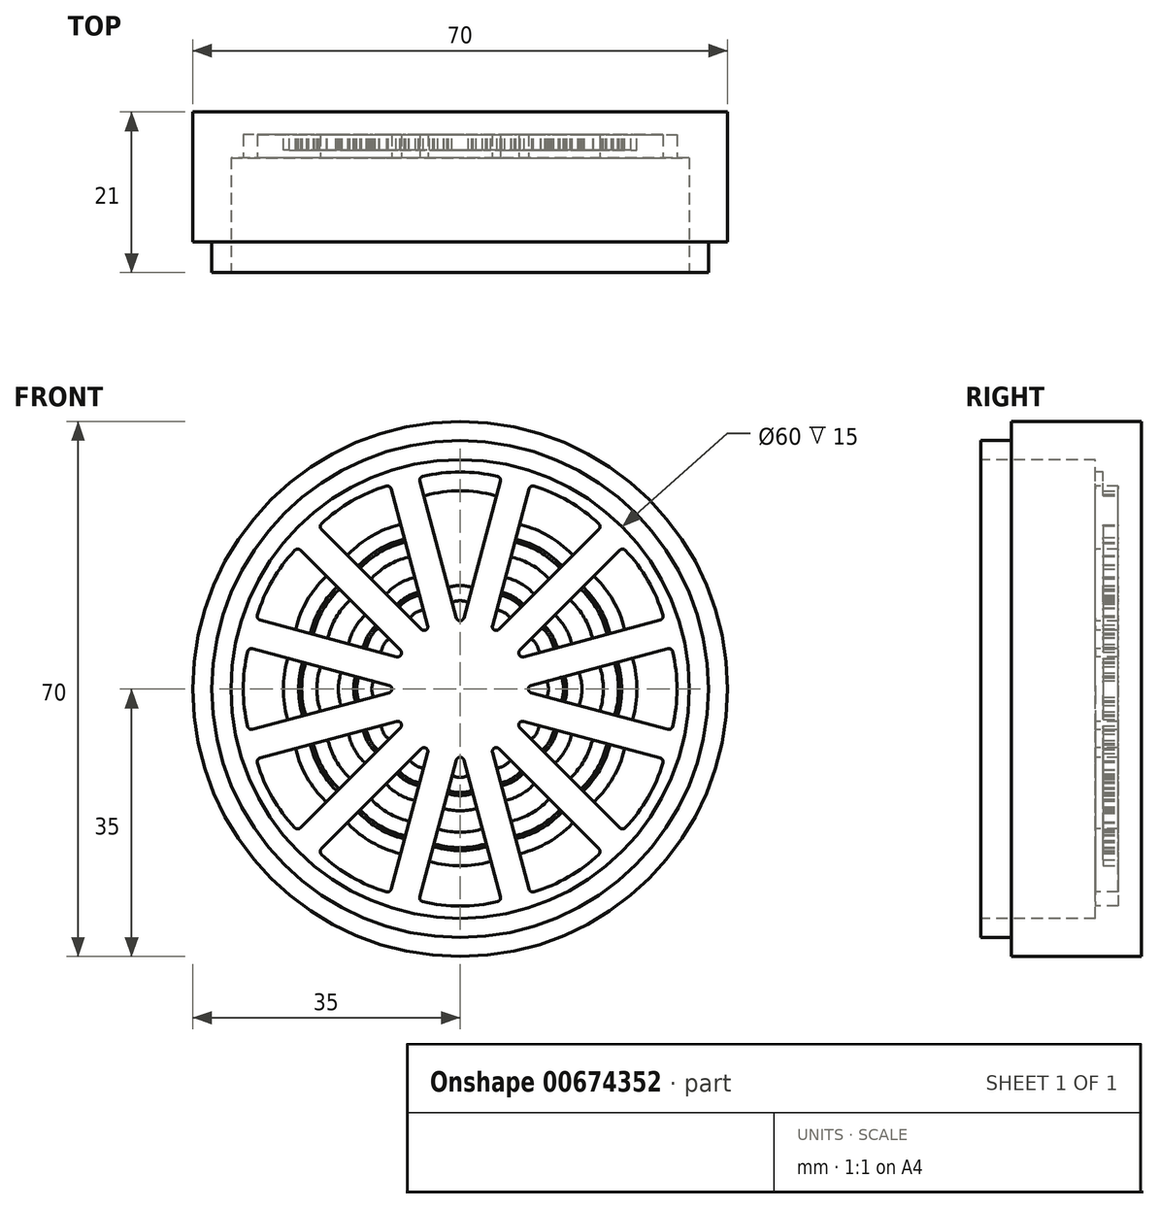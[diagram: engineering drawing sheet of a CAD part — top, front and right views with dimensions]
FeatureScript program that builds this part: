
annotation { "Feature Type Name" : "Feature", "Feature Type Description" : "" }
export const myFeature = defineFeature(function(context is Context, id is Id, definition is map)
    precondition{}
    {
        {
            var Q0;
            Q0=qCreatedBy(makeId("Front.planeOp"),FACE);
            var sketch = newSketch(context, id + "F0", { "sketchPlane" : qUnion([Q0])});
            skCircle(sketch, "E0", {"center": v(0, 0) * mm, "radius": 35 * mm});
            skSolve(sketch);
        }
        {
            var Q0;
            Q0=makeQuery(id+"F0.imprint","IMPRINT",FACE,{"disambiguationData":[TD([[makeQuery(id+"F0.imprint","IMPRINT",EDGE,{"derivedFrom":sQuery(id+"F0.wireOp",EDGE,"E0")}),1.0]])]});
            extrude(context, id + "F1", {"entities" : qUnion([Q0]), "depth" : 21 * mm, "offsetDistance" : 25 * mm});
        }
        {
            var Q0;
            Q0=makeQuery(id+"F1.opExtrude","CAP_FACE",FACE,{"disambiguationData":[OSD([sQuery(id+"F0.wireOp",EDGE,"E0")])],"isStart":false});
            var sketch = newSketch(context, id + "F2", { "sketchPlane" : qUnion([Q0])});
            skCircle(sketch, "E1", {"center": v(0, 0) * mm, "radius": 30 * mm});
            skSolve(sketch);
        }
        {
            var Q0;
            Q0=makeQuery(id+"F2.imprint","IMPRINT",FACE,{"disambiguationData":[TD([[makeQuery(id+"F2.imprint","IMPRINT",EDGE,{"derivedFrom":sQuery(id+"F2.wireOp",EDGE,"E1")}),1.0]])]});
            extrude(context, id + "F3", {"entities" : qUnion([Q0]), "operationType" : NewBodyOperationType.REMOVE, "oppositeDirection" : true, "depth" : 15 * mm, "offsetDistance" : 25 * mm});
        }
        {
            var Q0;
            Q0=makeQuery(id+"F1.opExtrude","CAP_FACE",FACE,{"disambiguationData":[OSD([sQuery(id+"F0.wireOp",EDGE,"E0")])],"isStart":false});
            var sketch = newSketch(context, id + "F4", { "sketchPlane" : qUnion([Q0])});
            skCircle(sketch, "E2", {"center": v(0, 0) * mm, "radius": 32.5 * mm});
            skSolve(sketch);
        }
        {
            var Q0;
            Q0=makeQuery(id+"F4.imprint","IMPRINT",FACE,{"disambiguationData":[TD([[makeQuery(id+"F4.imprint","IMPRINT",EDGE,{"derivedFrom":sQuery(id+"F4.wireOp",EDGE,"E2")}),-1.0]])]});
            extrude(context, id + "F5", {"entities" : qUnion([Q0]), "operationType" : NewBodyOperationType.REMOVE, "oppositeDirection" : true, "depth" : 4 * mm, "offsetDistance" : 25 * mm});
        }
        {
            var Q0;
            Q0=makeQuery(id+"F3.boolean.opBoolean","COPY",FACE,{"derivedFrom":makeQuery(id+"F3.opExtrude","CAP_FACE",FACE,{"disambiguationData":[OSD([sQuery(id+"F2.wireOp",EDGE,"E1")])],"isStart":false})});
            var sketch = newSketch(context, id + "F6", { "sketchPlane" : qUnion([Q0])});
            skLineSegment(sketch, "E3", {"start": v(0, 0) * mm, "end": v(-7.76, 28.98) * mm, "construction": true});
            skLineSegment(sketch, "E4", {"start": v(0, 0) * mm, "end": v(7.76, 28.98) * mm, "construction": true});
            skLineSegment(sketch, "E5", {"start": v(0, 0) * mm, "end": v(0, 30) * mm, "construction": true});
            skCircle(sketch, "E6", {"center": v(0, 0) * mm, "radius": 7.5 * mm, "construction": true});
            skLineSegment(sketch, "E7", {"start": v(-0.48, 9.3) * mm, "end": v(-5.27, 27.18) * mm});
            skLineSegment(sketch, "E8.MirrorCS", {"start": v(0.48, 9.3) * mm, "end": v(5.27, 27.18) * mm});
            skArc(sketch, "E9", {"start": v(-4.9, 27.8) * mm, "mid": v(0, 28.38) * mm, "end": v(4.9, 27.8) * mm});
            skPoint(sketch, "E10.visualSharp", {"position": v(-5.4, 27.67) * mm});
            skArc(sketch, "E10.filletArc", {"start": v(-4.9, 27.8) * mm, "mid": v(-5.22, 27.57) * mm, "end": v(-5.27, 27.18) * mm});
            skPoint(sketch, "E11.visualSharp", {"position": v(5.4, 27.67) * mm});
            skArc(sketch, "E11.filletArc", {"start": v(5.27, 27.18) * mm, "mid": v(5.22, 27.57) * mm, "end": v(4.9, 27.8) * mm});
            skArc(sketch, "E12.filletArc", {"start": v(-0.48, 9.3) * mm, "mid": v(0, 8.93) * mm, "end": v(0.48, 9.3) * mm});
            skPoint(sketch, "E13.1.0", {"position": v(-18.52, 21.26) * mm});
            skLineSegment(sketch, "E13.1.1", {"start": v(-5.07, 7.81) * mm, "end": v(-18.16, 20.9) * mm});
            skLineSegment(sketch, "E13.1.2", {"start": v(-4.23, 8.3) * mm, "end": v(-9.02, 26.18) * mm});
            skPoint(sketch, "E13.1.3", {"position": v(-9.15, 26.67) * mm});
            skArc(sketch, "E13.1.4", {"start": v(-18.15, 21.62) * mm, "mid": v(-14.2, 24.58) * mm, "end": v(-9.65, 26.53) * mm});
            skPoint(sketch, "E13.1.5", {"position": v(-3.75, 6.5) * mm});
            skArc(sketch, "E13.1.6", {"start": v(-5.07, 7.81) * mm, "mid": v(-4.47, 7.74) * mm, "end": v(-4.23, 8.3) * mm});
            skArc(sketch, "E13.1.7", {"start": v(-9.02, 26.18) * mm, "mid": v(-9.26, 26.48) * mm, "end": v(-9.65, 26.53) * mm});
            skArc(sketch, "E13.1.8", {"start": v(-18.15, 21.62) * mm, "mid": v(-18.3, 21.26) * mm, "end": v(-18.16, 20.9) * mm});
            skPoint(sketch, "E13.2.0", {"position": v(-26.67, 9.15) * mm});
            skLineSegment(sketch, "E13.2.1", {"start": v(-8.3, 4.23) * mm, "end": v(-26.18, 9.02) * mm});
            skLineSegment(sketch, "E13.2.2", {"start": v(-7.81, 5.07) * mm, "end": v(-20.9, 18.16) * mm});
            skPoint(sketch, "E13.2.3", {"position": v(-21.26, 18.52) * mm});
            skArc(sketch, "E13.2.4", {"start": v(-26.53, 9.65) * mm, "mid": v(-24.58, 14.2) * mm, "end": v(-21.62, 18.15) * mm});
            skPoint(sketch, "E13.2.5", {"position": v(-6.5, 3.75) * mm});
            skArc(sketch, "E13.2.6", {"start": v(-8.3, 4.23) * mm, "mid": v(-7.74, 4.47) * mm, "end": v(-7.81, 5.07) * mm});
            skArc(sketch, "E13.2.7", {"start": v(-20.9, 18.16) * mm, "mid": v(-21.26, 18.3) * mm, "end": v(-21.62, 18.15) * mm});
            skArc(sketch, "E13.2.8", {"start": v(-26.53, 9.65) * mm, "mid": v(-26.48, 9.26) * mm, "end": v(-26.18, 9.02) * mm});
            skPoint(sketch, "E13.3.0", {"position": v(-27.67, -5.4) * mm});
            skLineSegment(sketch, "E13.3.1", {"start": v(-9.3, -0.48) * mm, "end": v(-27.18, -5.27) * mm});
            skLineSegment(sketch, "E13.3.2", {"start": v(-9.3, 0.48) * mm, "end": v(-27.18, 5.27) * mm});
            skPoint(sketch, "E13.3.3", {"position": v(-27.67, 5.4) * mm});
            skArc(sketch, "E13.3.4", {"start": v(-27.8, -4.9) * mm, "mid": v(-28.38, 0) * mm, "end": v(-27.8, 4.9) * mm});
            skPoint(sketch, "E13.3.5", {"position": v(-7.5, 0) * mm});
            skArc(sketch, "E13.3.6", {"start": v(-9.3, -0.48) * mm, "mid": v(-8.93, 0) * mm, "end": v(-9.3, 0.48) * mm});
            skArc(sketch, "E13.3.7", {"start": v(-27.18, 5.27) * mm, "mid": v(-27.57, 5.22) * mm, "end": v(-27.8, 4.9) * mm});
            skArc(sketch, "E13.3.8", {"start": v(-27.8, -4.9) * mm, "mid": v(-27.57, -5.22) * mm, "end": v(-27.18, -5.27) * mm});
            skPoint(sketch, "E13.4.0", {"position": v(-21.26, -18.52) * mm});
            skLineSegment(sketch, "E13.4.1", {"start": v(-7.81, -5.07) * mm, "end": v(-20.9, -18.16) * mm});
            skLineSegment(sketch, "E13.4.2", {"start": v(-8.3, -4.23) * mm, "end": v(-26.18, -9.02) * mm});
            skPoint(sketch, "E13.4.3", {"position": v(-26.67, -9.15) * mm});
            skArc(sketch, "E13.4.4", {"start": v(-21.62, -18.15) * mm, "mid": v(-24.58, -14.2) * mm, "end": v(-26.53, -9.65) * mm});
            skPoint(sketch, "E13.4.5", {"position": v(-6.5, -3.75) * mm});
            skArc(sketch, "E13.4.6", {"start": v(-7.81, -5.07) * mm, "mid": v(-7.74, -4.47) * mm, "end": v(-8.3, -4.23) * mm});
            skArc(sketch, "E13.4.7", {"start": v(-26.18, -9.02) * mm, "mid": v(-26.48, -9.26) * mm, "end": v(-26.53, -9.65) * mm});
            skArc(sketch, "E13.4.8", {"start": v(-21.62, -18.15) * mm, "mid": v(-21.26, -18.3) * mm, "end": v(-20.9, -18.16) * mm});
            skPoint(sketch, "E13.5.0", {"position": v(-9.15, -26.67) * mm});
            skLineSegment(sketch, "E13.5.1", {"start": v(-4.23, -8.3) * mm, "end": v(-9.02, -26.18) * mm});
            skLineSegment(sketch, "E13.5.2", {"start": v(-5.07, -7.81) * mm, "end": v(-18.16, -20.9) * mm});
            skPoint(sketch, "E13.5.3", {"position": v(-18.52, -21.26) * mm});
            skArc(sketch, "E13.5.4", {"start": v(-9.65, -26.53) * mm, "mid": v(-14.2, -24.58) * mm, "end": v(-18.15, -21.62) * mm});
            skPoint(sketch, "E13.5.5", {"position": v(-3.75, -6.5) * mm});
            skArc(sketch, "E13.5.6", {"start": v(-4.23, -8.3) * mm, "mid": v(-4.47, -7.74) * mm, "end": v(-5.07, -7.81) * mm});
            skArc(sketch, "E13.5.7", {"start": v(-18.16, -20.9) * mm, "mid": v(-18.3, -21.26) * mm, "end": v(-18.15, -21.62) * mm});
            skArc(sketch, "E13.5.8", {"start": v(-9.65, -26.53) * mm, "mid": v(-9.26, -26.48) * mm, "end": v(-9.02, -26.18) * mm});
            skPoint(sketch, "E13.6.0", {"position": v(5.4, -27.67) * mm});
            skLineSegment(sketch, "E13.6.1", {"start": v(0.48, -9.3) * mm, "end": v(5.27, -27.18) * mm});
            skLineSegment(sketch, "E13.6.2", {"start": v(-0.48, -9.3) * mm, "end": v(-5.27, -27.18) * mm});
            skPoint(sketch, "E13.6.3", {"position": v(-5.4, -27.67) * mm});
            skArc(sketch, "E13.6.4", {"start": v(4.9, -27.8) * mm, "mid": v(0, -28.38) * mm, "end": v(-4.9, -27.8) * mm});
            skPoint(sketch, "E13.6.5", {"position": v(0, -7.5) * mm});
            skArc(sketch, "E13.6.6", {"start": v(0.48, -9.3) * mm, "mid": v(0, -8.93) * mm, "end": v(-0.48, -9.3) * mm});
            skArc(sketch, "E13.6.7", {"start": v(-5.27, -27.18) * mm, "mid": v(-5.22, -27.57) * mm, "end": v(-4.9, -27.8) * mm});
            skArc(sketch, "E13.6.8", {"start": v(4.9, -27.8) * mm, "mid": v(5.22, -27.57) * mm, "end": v(5.27, -27.18) * mm});
            skPoint(sketch, "E13.7.0", {"position": v(18.52, -21.26) * mm});
            skLineSegment(sketch, "E13.7.1", {"start": v(5.07, -7.81) * mm, "end": v(18.16, -20.9) * mm});
            skLineSegment(sketch, "E13.7.2", {"start": v(4.23, -8.3) * mm, "end": v(9.02, -26.18) * mm});
            skPoint(sketch, "E13.7.3", {"position": v(9.15, -26.67) * mm});
            skArc(sketch, "E13.7.4", {"start": v(18.15, -21.62) * mm, "mid": v(14.2, -24.58) * mm, "end": v(9.65, -26.53) * mm});
            skPoint(sketch, "E13.7.5", {"position": v(3.75, -6.5) * mm});
            skArc(sketch, "E13.7.6", {"start": v(5.07, -7.81) * mm, "mid": v(4.47, -7.74) * mm, "end": v(4.23, -8.3) * mm});
            skArc(sketch, "E13.7.7", {"start": v(9.02, -26.18) * mm, "mid": v(9.26, -26.48) * mm, "end": v(9.65, -26.53) * mm});
            skArc(sketch, "E13.7.8", {"start": v(18.15, -21.62) * mm, "mid": v(18.3, -21.26) * mm, "end": v(18.16, -20.9) * mm});
            skPoint(sketch, "E13.8.0", {"position": v(26.67, -9.15) * mm});
            skLineSegment(sketch, "E13.8.1", {"start": v(8.3, -4.23) * mm, "end": v(26.18, -9.02) * mm});
            skLineSegment(sketch, "E13.8.2", {"start": v(7.81, -5.07) * mm, "end": v(20.9, -18.16) * mm});
            skPoint(sketch, "E13.8.3", {"position": v(21.26, -18.52) * mm});
            skArc(sketch, "E13.8.4", {"start": v(26.53, -9.65) * mm, "mid": v(24.58, -14.2) * mm, "end": v(21.62, -18.15) * mm});
            skPoint(sketch, "E13.8.5", {"position": v(6.5, -3.75) * mm});
            skArc(sketch, "E13.8.6", {"start": v(8.3, -4.23) * mm, "mid": v(7.74, -4.47) * mm, "end": v(7.81, -5.07) * mm});
            skArc(sketch, "E13.8.7", {"start": v(20.9, -18.16) * mm, "mid": v(21.26, -18.3) * mm, "end": v(21.62, -18.15) * mm});
            skArc(sketch, "E13.8.8", {"start": v(26.53, -9.65) * mm, "mid": v(26.48, -9.26) * mm, "end": v(26.18, -9.02) * mm});
            skPoint(sketch, "E13.9.0", {"position": v(27.67, 5.4) * mm});
            skLineSegment(sketch, "E13.9.1", {"start": v(9.3, 0.48) * mm, "end": v(27.18, 5.27) * mm});
            skLineSegment(sketch, "E13.9.2", {"start": v(9.3, -0.48) * mm, "end": v(27.18, -5.27) * mm});
            skPoint(sketch, "E13.9.3", {"position": v(27.67, -5.4) * mm});
            skArc(sketch, "E13.9.4", {"start": v(27.8, 4.9) * mm, "mid": v(28.38, 0) * mm, "end": v(27.8, -4.9) * mm});
            skPoint(sketch, "E13.9.5", {"position": v(7.5, 0) * mm});
            skArc(sketch, "E13.9.6", {"start": v(9.3, 0.48) * mm, "mid": v(8.93, 0) * mm, "end": v(9.3, -0.48) * mm});
            skArc(sketch, "E13.9.7", {"start": v(27.18, -5.27) * mm, "mid": v(27.57, -5.22) * mm, "end": v(27.8, -4.9) * mm});
            skArc(sketch, "E13.9.8", {"start": v(27.8, 4.9) * mm, "mid": v(27.57, 5.22) * mm, "end": v(27.18, 5.27) * mm});
            skPoint(sketch, "E13.10.0", {"position": v(21.26, 18.52) * mm});
            skLineSegment(sketch, "E13.10.1", {"start": v(7.81, 5.07) * mm, "end": v(20.9, 18.16) * mm});
            skLineSegment(sketch, "E13.10.2", {"start": v(8.3, 4.23) * mm, "end": v(26.18, 9.02) * mm});
            skPoint(sketch, "E13.10.3", {"position": v(26.67, 9.15) * mm});
            skArc(sketch, "E13.10.4", {"start": v(21.62, 18.15) * mm, "mid": v(24.58, 14.2) * mm, "end": v(26.53, 9.65) * mm});
            skPoint(sketch, "E13.10.5", {"position": v(6.5, 3.75) * mm});
            skArc(sketch, "E13.10.6", {"start": v(7.81, 5.07) * mm, "mid": v(7.74, 4.47) * mm, "end": v(8.3, 4.23) * mm});
            skArc(sketch, "E13.10.7", {"start": v(26.18, 9.02) * mm, "mid": v(26.48, 9.26) * mm, "end": v(26.53, 9.65) * mm});
            skArc(sketch, "E13.10.8", {"start": v(21.62, 18.15) * mm, "mid": v(21.26, 18.3) * mm, "end": v(20.9, 18.16) * mm});
            skPoint(sketch, "E13.11.0", {"position": v(9.15, 26.67) * mm});
            skLineSegment(sketch, "E13.11.1", {"start": v(4.23, 8.3) * mm, "end": v(9.02, 26.18) * mm});
            skLineSegment(sketch, "E13.11.2", {"start": v(5.07, 7.81) * mm, "end": v(18.16, 20.9) * mm});
            skPoint(sketch, "E13.11.3", {"position": v(18.52, 21.26) * mm});
            skArc(sketch, "E13.11.4", {"start": v(9.65, 26.53) * mm, "mid": v(14.2, 24.58) * mm, "end": v(18.15, 21.62) * mm});
            skPoint(sketch, "E13.11.5", {"position": v(3.75, 6.5) * mm});
            skArc(sketch, "E13.11.6", {"start": v(4.23, 8.3) * mm, "mid": v(4.47, 7.74) * mm, "end": v(5.07, 7.81) * mm});
            skArc(sketch, "E13.11.7", {"start": v(18.16, 20.9) * mm, "mid": v(18.3, 21.26) * mm, "end": v(18.15, 21.62) * mm});
            skArc(sketch, "E13.11.8", {"start": v(9.65, 26.53) * mm, "mid": v(9.26, 26.48) * mm, "end": v(9.02, 26.18) * mm});
            skSolve(sketch);
        }
        {
            var Q0;
            Q0=makeQuery(id+"F6.imprint","IMPRINT",FACE,{"disambiguationData":[TD([[makeQuery(id+"F6.imprint","IMPRINT",EDGE,{"derivedFrom":sQuery(id+"F6.wireOp",EDGE,"E13.1.1")}),-1.0]])]});
            var Q1;
            Q1=makeQuery(id+"F6.imprint","IMPRINT",FACE,{"disambiguationData":[TD([[makeQuery(id+"F6.imprint","IMPRINT",EDGE,{"derivedFrom":sQuery(id+"F6.wireOp",EDGE,"E7")}),-1.0]])]});
            var Q2;
            Q2=makeQuery(id+"F6.imprint","IMPRINT",FACE,{"disambiguationData":[TD([[makeQuery(id+"F6.imprint","IMPRINT",EDGE,{"derivedFrom":sQuery(id+"F6.wireOp",EDGE,"E13.11.1")}),-1.0]])]});
            var Q3;
            Q3=makeQuery(id+"F6.imprint","IMPRINT",FACE,{"disambiguationData":[TD([[makeQuery(id+"F6.imprint","IMPRINT",EDGE,{"derivedFrom":sQuery(id+"F6.wireOp",EDGE,"E13.10.1")}),-1.0]])]});
            var Q4;
            Q4=makeQuery(id+"F6.imprint","IMPRINT",FACE,{"disambiguationData":[TD([[makeQuery(id+"F6.imprint","IMPRINT",EDGE,{"derivedFrom":sQuery(id+"F6.wireOp",EDGE,"E13.9.1")}),-1.0]])]});
            var Q5;
            Q5=makeQuery(id+"F6.imprint","IMPRINT",FACE,{"disambiguationData":[TD([[makeQuery(id+"F6.imprint","IMPRINT",EDGE,{"derivedFrom":sQuery(id+"F6.wireOp",EDGE,"E13.8.1")}),-1.0]])]});
            var Q6;
            Q6=makeQuery(id+"F6.imprint","IMPRINT",FACE,{"disambiguationData":[TD([[makeQuery(id+"F6.imprint","IMPRINT",EDGE,{"derivedFrom":sQuery(id+"F6.wireOp",EDGE,"E13.7.1")}),-1.0]])]});
            var Q7;
            Q7=makeQuery(id+"F6.imprint","IMPRINT",FACE,{"disambiguationData":[TD([[makeQuery(id+"F6.imprint","IMPRINT",EDGE,{"derivedFrom":sQuery(id+"F6.wireOp",EDGE,"E13.6.1")}),-1.0]])]});
            var Q8;
            Q8=makeQuery(id+"F6.imprint","IMPRINT",FACE,{"disambiguationData":[TD([[makeQuery(id+"F6.imprint","IMPRINT",EDGE,{"derivedFrom":sQuery(id+"F6.wireOp",EDGE,"E13.5.1")}),-1.0]])]});
            var Q9;
            Q9=makeQuery(id+"F6.imprint","IMPRINT",FACE,{"disambiguationData":[TD([[makeQuery(id+"F6.imprint","IMPRINT",EDGE,{"derivedFrom":sQuery(id+"F6.wireOp",EDGE,"E13.4.1")}),-1.0]])]});
            var Q10;
            Q10=makeQuery(id+"F6.imprint","IMPRINT",FACE,{"disambiguationData":[TD([[makeQuery(id+"F6.imprint","IMPRINT",EDGE,{"derivedFrom":sQuery(id+"F6.wireOp",EDGE,"E13.3.1")}),-1.0]])]});
            var Q11;
            Q11=makeQuery(id+"F6.imprint","IMPRINT",FACE,{"disambiguationData":[TD([[makeQuery(id+"F6.imprint","IMPRINT",EDGE,{"derivedFrom":sQuery(id+"F6.wireOp",EDGE,"E13.2.1")}),-1.0]])]});
            extrude(context, id + "F7", {"entities" : qUnion([Q0, Q1, Q2, Q3, Q4, Q5, Q6, Q7, Q8, Q9, Q10, Q11]), "operationType" : NewBodyOperationType.REMOVE, "oppositeDirection" : true, "depth" : 3 * mm, "offsetDistance" : 25 * mm});
        }
        {
            var Q0;
            Q0=makeQuery(id+"F7.boolean.opBoolean","COPY",FACE,{"derivedFrom":makeQuery(id+"F7.opExtrude","CAP_FACE",FACE,{"disambiguationData":[OSD([sQuery(id+"F6.wireOp",EDGE,"E7"),sQuery(id+"F6.wireOp",EDGE,"E8.MirrorCS"),sQuery(id+"F6.wireOp",EDGE,"E9"),sQuery(id+"F6.wireOp",EDGE,"E10.filletArc"),sQuery(id+"F6.wireOp",EDGE,"E11.filletArc"),sQuery(id+"F6.wireOp",EDGE,"E12.filletArc")])],"isStart":false})});
            var sketch = newSketch(context, id + "F8", { "sketchPlane" : qUnion([Q0])});
            skLineSegment(sketch, "E14", {"start": v(-5.27, 27.18) * mm, "end": v(-0.48, 9.3) * mm});
            skLineSegment(sketch, "E15", {"start": v(5.27, 27.18) * mm, "end": v(0.48, 9.3) * mm});
            skLineSegment(sketch, "E16", {"start": v(-5.27, 27.18) * mm, "end": v(-4.8, 25.45) * mm, "construction": true});
            skLineSegment(sketch, "E17", {"start": v(-4.76, 25.25) * mm, "end": v(-4.65, 24.86) * mm, "construction": true});
            skLineSegment(sketch, "E18", {"start": v(-4.6, 24.67) * mm, "end": v(-4.19, 23.13) * mm});
            skLineSegment(sketch, "E19", {"start": v(-4.14, 22.93) * mm, "end": v(-4.03, 22.55) * mm});
            skLineSegment(sketch, "E20", {"start": v(-3.98, 22.36) * mm, "end": v(-3.57, 20.81) * mm});
            skLineSegment(sketch, "E21", {"start": v(-3.51, 20.61) * mm, "end": v(-3.41, 20.23) * mm});
            skLineSegment(sketch, "E22", {"start": v(-3.36, 20.04) * mm, "end": v(-2.95, 18.5) * mm});
            skLineSegment(sketch, "E23", {"start": v(-2.9, 18.3) * mm, "end": v(-2.79, 17.9) * mm});
            skLineSegment(sketch, "E24", {"start": v(-2.74, 17.72) * mm, "end": v(-2.33, 16.18) * mm});
            skLineSegment(sketch, "E25", {"start": v(-2.27, 15.98) * mm, "end": v(-2.17, 15.6) * mm});
            skLineSegment(sketch, "E26", {"start": v(-2.12, 15.4) * mm, "end": v(-1.7, 13.86) * mm});
            skLineSegment(sketch, "E27", {"start": v(-1.65, 13.66) * mm, "end": v(-1.55, 13.27) * mm});
            skLineSegment(sketch, "E28", {"start": v(-1.55, 13.27) * mm, "end": v(-1.03, 11.34) * mm});
            skLineSegment(sketch, "E29", {"start": v(-1.03, 11.34) * mm, "end": v(-0.93, 10.96) * mm});
            skLineSegment(sketch, "E30", {"start": v(0, 28.38) * mm, "end": v(0, 8.93) * mm, "construction": true});
            skLineSegment(sketch, "E31.MirrorCS", {"start": v(2.27, 15.98) * mm, "end": v(2.17, 15.6) * mm});
            skLineSegment(sketch, "E32.MirrorCS", {"start": v(1.03, 11.34) * mm, "end": v(0.93, 10.96) * mm});
            skLineSegment(sketch, "E33.MirrorCS", {"start": v(4.76, 25.25) * mm, "end": v(4.65, 24.86) * mm, "construction": true});
            skLineSegment(sketch, "E34.MirrorCS", {"start": v(3.51, 20.61) * mm, "end": v(3.41, 20.23) * mm});
            skLineSegment(sketch, "E35.MirrorCS", {"start": v(4.14, 22.93) * mm, "end": v(4.03, 22.55) * mm});
            skLineSegment(sketch, "E36.MirrorCS", {"start": v(2.9, 18.3) * mm, "end": v(2.79, 17.9) * mm});
            skLineSegment(sketch, "E37.MirrorCS", {"start": v(1.65, 13.66) * mm, "end": v(1.55, 13.27) * mm});
            skLineSegment(sketch, "E38.MirrorCS", {"start": v(1.5, 13.1) * mm, "end": v(1.09, 11.56) * mm});
            skLineSegment(sketch, "E39.MirrorCS", {"start": v(5.27, 27.18) * mm, "end": v(4.8, 25.45) * mm, "construction": true});
            skLineSegment(sketch, "E40.MirrorCS", {"start": v(3.98, 22.36) * mm, "end": v(3.57, 20.81) * mm});
            skLineSegment(sketch, "E41.MirrorCS", {"start": v(3.36, 20.04) * mm, "end": v(2.95, 18.5) * mm});
            skLineSegment(sketch, "E42.MirrorCS", {"start": v(4.6, 24.67) * mm, "end": v(4.19, 23.13) * mm});
            skLineSegment(sketch, "E43.MirrorCS", {"start": v(2.12, 15.4) * mm, "end": v(1.7, 13.86) * mm});
            skLineSegment(sketch, "E44.MirrorCS", {"start": v(2.74, 17.72) * mm, "end": v(2.33, 16.18) * mm});
            skArc(sketch, "E45", {"start": v(-4.56, 25.3) * mm, "mid": v(0, 25.93) * mm, "end": v(4.56, 25.3) * mm});
            skArc(sketch, "E46", {"start": v(-4.46, 24.92) * mm, "mid": v(0, 25.53) * mm, "end": v(4.46, 24.92) * mm});
            skArc(sketch, "E47", {"start": v(-3.94, 22.99) * mm, "mid": v(0, 23.53) * mm, "end": v(3.94, 22.99) * mm});
            skArc(sketch, "E48", {"start": v(-3.84, 22.6) * mm, "mid": v(0, 23.13) * mm, "end": v(3.84, 22.6) * mm});
            skArc(sketch, "E49", {"start": v(-3.32, 20.67) * mm, "mid": v(0, 21.13) * mm, "end": v(3.32, 20.67) * mm});
            skArc(sketch, "E50", {"start": v(-3.22, 20.28) * mm, "mid": v(0, 20.73) * mm, "end": v(3.22, 20.28) * mm});
            skArc(sketch, "E51", {"start": v(-2.7, 18.35) * mm, "mid": v(0, 18.73) * mm, "end": v(2.7, 18.35) * mm});
            skArc(sketch, "E52", {"start": v(-2.6, 17.97) * mm, "mid": v(0, 18.33) * mm, "end": v(2.6, 17.97) * mm});
            skArc(sketch, "E53", {"start": v(-2.08, 16.04) * mm, "mid": v(0, 16.34) * mm, "end": v(2.08, 16.04) * mm});
            skArc(sketch, "E54", {"start": v(-1.98, 15.65) * mm, "mid": v(0, 15.94) * mm, "end": v(1.98, 15.65) * mm});
            skArc(sketch, "E55", {"start": v(-1.45, 13.72) * mm, "mid": v(0, 13.94) * mm, "end": v(1.45, 13.72) * mm});
            skArc(sketch, "E56", {"start": v(-1.36, 13.33) * mm, "mid": v(0, 13.54) * mm, "end": v(1.36, 13.33) * mm});
            skArc(sketch, "E57", {"start": v(-0.83, 11.42) * mm, "mid": v(0, 11.55) * mm, "end": v(0.83, 11.42) * mm});
            skArc(sketch, "E58", {"start": v(-0.75, 11.03) * mm, "mid": v(0, 11.16) * mm, "end": v(0.75, 11.03) * mm});
            skPoint(sketch, "E59.visualSharp", {"position": v(-4.76, 25.25) * mm});
            skArc(sketch, "E59.filletArc", {"start": v(-4.8, 25.45) * mm, "mid": v(-4.71, 25.33) * mm, "end": v(-4.56, 25.3) * mm});
            skPoint(sketch, "E60.visualSharp", {"position": v(-4.65, 24.86) * mm});
            skArc(sketch, "E60.filletArc", {"start": v(-4.46, 24.92) * mm, "mid": v(-4.58, 24.83) * mm, "end": v(-4.6, 24.67) * mm});
            skPoint(sketch, "E61.visualSharp", {"position": v(-4.14, 22.93) * mm});
            skArc(sketch, "E61.filletArc", {"start": v(-4.19, 23.13) * mm, "mid": v(-4.1, 23) * mm, "end": v(-3.94, 22.99) * mm});
            skPoint(sketch, "E62.visualSharp", {"position": v(-4.03, 22.55) * mm});
            skArc(sketch, "E62.filletArc", {"start": v(-3.84, 22.6) * mm, "mid": v(-3.96, 22.5) * mm, "end": v(-3.98, 22.36) * mm});
            skPoint(sketch, "E63.visualSharp", {"position": v(-3.51, 20.61) * mm});
            skArc(sketch, "E63.filletArc", {"start": v(-3.57, 20.81) * mm, "mid": v(-3.47, 20.69) * mm, "end": v(-3.32, 20.67) * mm});
            skPoint(sketch, "E64.visualSharp", {"position": v(-3.41, 20.23) * mm});
            skArc(sketch, "E64.filletArc", {"start": v(-3.22, 20.28) * mm, "mid": v(-3.34, 20.19) * mm, "end": v(-3.36, 20.04) * mm});
            skPoint(sketch, "E65.visualSharp", {"position": v(-2.9, 18.3) * mm});
            skArc(sketch, "E65.filletArc", {"start": v(-2.95, 18.5) * mm, "mid": v(-2.85, 18.37) * mm, "end": v(-2.7, 18.35) * mm});
            skPoint(sketch, "E66.visualSharp", {"position": v(-2.79, 17.9) * mm});
            skArc(sketch, "E66.filletArc", {"start": v(-2.6, 17.97) * mm, "mid": v(-2.72, 17.87) * mm, "end": v(-2.74, 17.72) * mm});
            skPoint(sketch, "E67.visualSharp", {"position": v(-2.27, 15.98) * mm});
            skArc(sketch, "E67.filletArc", {"start": v(-2.33, 16.18) * mm, "mid": v(-2.23, 16.06) * mm, "end": v(-2.08, 16.04) * mm});
            skPoint(sketch, "E68.visualSharp", {"position": v(-2.17, 15.6) * mm});
            skArc(sketch, "E68.filletArc", {"start": v(-1.98, 15.65) * mm, "mid": v(-2.1, 15.56) * mm, "end": v(-2.12, 15.4) * mm});
            skPoint(sketch, "E69.visualSharp", {"position": v(-1.65, 13.66) * mm});
            skArc(sketch, "E69.filletArc", {"start": v(-1.7, 13.86) * mm, "mid": v(-1.6, 13.74) * mm, "end": v(-1.45, 13.72) * mm});
            skLineSegment(sketch, "E70", {"start": v(-1.5, 13.1) * mm, "end": v(-1.09, 11.56) * mm});
            skLineSegment(sketch, "E71", {"start": v(-0.88, 10.79) * mm, "end": v(-0.48, 9.3) * mm});
            skLineSegment(sketch, "E72.MirrorCS", {"start": v(1.55, 13.27) * mm, "end": v(1.03, 11.34) * mm});
            skLineSegment(sketch, "E73.MirrorCS", {"start": v(0.88, 10.79) * mm, "end": v(0.48, 9.3) * mm});
            skPoint(sketch, "E74.visualSharp", {"position": v(-1.55, 13.27) * mm});
            skArc(sketch, "E74.filletArc", {"start": v(-1.36, 13.33) * mm, "mid": v(-1.48, 13.24) * mm, "end": v(-1.5, 13.1) * mm});
            skPoint(sketch, "E75.visualSharp", {"position": v(-1.03, 11.34) * mm});
            skArc(sketch, "E75.filletArc", {"start": v(-1.09, 11.56) * mm, "mid": v(-0.99, 11.43) * mm, "end": v(-0.83, 11.42) * mm});
            skPoint(sketch, "E76.visualSharp", {"position": v(-0.93, 10.96) * mm});
            skArc(sketch, "E76.filletArc", {"start": v(-0.75, 11.03) * mm, "mid": v(-0.86, 10.93) * mm, "end": v(-0.88, 10.79) * mm});
            skPoint(sketch, "E77.visualSharp", {"position": v(0.93, 10.96) * mm});
            skArc(sketch, "E77.filletArc", {"start": v(0.88, 10.79) * mm, "mid": v(0.86, 10.93) * mm, "end": v(0.75, 11.03) * mm});
            skPoint(sketch, "E78.visualSharp", {"position": v(1.03, 11.34) * mm});
            skArc(sketch, "E78.filletArc", {"start": v(0.83, 11.42) * mm, "mid": v(0.99, 11.43) * mm, "end": v(1.09, 11.56) * mm});
            skPoint(sketch, "E79.visualSharp", {"position": v(1.55, 13.27) * mm});
            skArc(sketch, "E79.filletArc", {"start": v(1.5, 13.1) * mm, "mid": v(1.48, 13.24) * mm, "end": v(1.36, 13.33) * mm});
            skPoint(sketch, "E80.visualSharp", {"position": v(1.65, 13.66) * mm});
            skArc(sketch, "E80.filletArc", {"start": v(1.45, 13.72) * mm, "mid": v(1.6, 13.74) * mm, "end": v(1.7, 13.86) * mm});
            skPoint(sketch, "E81.visualSharp", {"position": v(2.17, 15.6) * mm});
            skArc(sketch, "E81.filletArc", {"start": v(2.12, 15.4) * mm, "mid": v(2.1, 15.56) * mm, "end": v(1.98, 15.65) * mm});
            skPoint(sketch, "E82.visualSharp", {"position": v(2.27, 15.98) * mm});
            skArc(sketch, "E82.filletArc", {"start": v(2.08, 16.04) * mm, "mid": v(2.23, 16.06) * mm, "end": v(2.33, 16.18) * mm});
            skPoint(sketch, "E83.visualSharp", {"position": v(2.79, 17.9) * mm});
            skArc(sketch, "E83.filletArc", {"start": v(2.74, 17.72) * mm, "mid": v(2.72, 17.87) * mm, "end": v(2.6, 17.97) * mm});
            skPoint(sketch, "E84.visualSharp", {"position": v(2.9, 18.3) * mm});
            skArc(sketch, "E84.filletArc", {"start": v(2.7, 18.35) * mm, "mid": v(2.85, 18.37) * mm, "end": v(2.95, 18.5) * mm});
            skPoint(sketch, "E85.visualSharp", {"position": v(3.41, 20.23) * mm});
            skArc(sketch, "E85.filletArc", {"start": v(3.36, 20.04) * mm, "mid": v(3.34, 20.19) * mm, "end": v(3.22, 20.28) * mm});
            skPoint(sketch, "E86.visualSharp", {"position": v(3.51, 20.61) * mm});
            skArc(sketch, "E86.filletArc", {"start": v(3.32, 20.67) * mm, "mid": v(3.47, 20.69) * mm, "end": v(3.57, 20.81) * mm});
            skPoint(sketch, "E87.visualSharp", {"position": v(4.03, 22.55) * mm});
            skArc(sketch, "E87.filletArc", {"start": v(3.98, 22.36) * mm, "mid": v(3.96, 22.5) * mm, "end": v(3.84, 22.6) * mm});
            skPoint(sketch, "E88.visualSharp", {"position": v(4.14, 22.93) * mm});
            skArc(sketch, "E88.filletArc", {"start": v(3.94, 22.99) * mm, "mid": v(4.1, 23) * mm, "end": v(4.19, 23.13) * mm});
            skPoint(sketch, "E89.visualSharp", {"position": v(4.65, 24.86) * mm});
            skArc(sketch, "E89.filletArc", {"start": v(4.6, 24.67) * mm, "mid": v(4.58, 24.83) * mm, "end": v(4.46, 24.92) * mm});
            skPoint(sketch, "E90.visualSharp", {"position": v(4.76, 25.25) * mm});
            skArc(sketch, "E90.filletArc", {"start": v(4.56, 25.3) * mm, "mid": v(4.71, 25.33) * mm, "end": v(4.8, 25.45) * mm});
            skLineSegment(sketch, "E91.1.0", {"start": v(-6.15, 8.9) * mm, "end": v(-5.07, 7.81) * mm});
            skArc(sketch, "E91.1.1", {"start": v(-7.85, 10.87) * mm, "mid": v(-6.77, 11.73) * mm, "end": v(-5.49, 12.23) * mm});
            skLineSegment(sketch, "E91.1.2", {"start": v(-7.73, 21.35) * mm, "end": v(-7.32, 19.8) * mm});
            skLineSegment(sketch, "E91.1.3", {"start": v(-8.35, 23.67) * mm, "end": v(-7.94, 22.12) * mm});
            skArc(sketch, "E91.1.4", {"start": v(-13.21, 16.24) * mm, "mid": v(-10.57, 18.3) * mm, "end": v(-7.46, 19.56) * mm});
            skLineSegment(sketch, "E91.1.5", {"start": v(-4.63, 9.78) * mm, "end": v(-4.23, 8.3) * mm});
            skArc(sketch, "E91.1.6", {"start": v(-14.63, 17.65) * mm, "mid": v(-11.57, 20.03) * mm, "end": v(-7.97, 21.5) * mm});
            skArc(sketch, "E91.1.7", {"start": v(-8.12, 11.16) * mm, "mid": v(-6.97, 12.07) * mm, "end": v(-5.6, 12.61) * mm});
            skLineSegment(sketch, "E91.1.8", {"start": v(-9.02, 26.18) * mm, "end": v(-8.56, 24.44) * mm, "construction": true});
            skLineSegment(sketch, "E91.1.9", {"start": v(-9.54, 12.28) * mm, "end": v(-8.4, 11.15) * mm});
            skLineSegment(sketch, "E91.1.10", {"start": v(-11.23, 13.98) * mm, "end": v(-10.1, 12.85) * mm});
            skLineSegment(sketch, "E91.1.11", {"start": v(-6.49, 16.72) * mm, "end": v(-6.08, 15.17) * mm});
            skArc(sketch, "E91.1.12", {"start": v(-11.51, 14.55) * mm, "mid": v(-9.37, 16.22) * mm, "end": v(-6.84, 17.24) * mm});
            skLineSegment(sketch, "E91.1.13", {"start": v(-7.1, 19.03) * mm, "end": v(-6.7, 17.5) * mm});
            skArc(sketch, "E91.1.14", {"start": v(-12.93, 15.96) * mm, "mid": v(-10.37, 17.95) * mm, "end": v(-7.35, 19.18) * mm});
            skLineSegment(sketch, "E91.1.15", {"start": v(-5.87, 14.4) * mm, "end": v(-5.46, 12.86) * mm});
            skLineSegment(sketch, "E91.1.16", {"start": v(-12.93, 15.67) * mm, "end": v(-11.8, 14.54) * mm});
            skLineSegment(sketch, "E91.1.17", {"start": v(-14.63, 17.37) * mm, "end": v(-13.5, 16.24) * mm});
            skLineSegment(sketch, "E91.1.18", {"start": v(-16.32, 19.07) * mm, "end": v(-15.2, 17.94) * mm});
            skArc(sketch, "E91.1.19", {"start": v(-16.6, 19.63) * mm, "mid": v(-12.97, 22.46) * mm, "end": v(-8.7, 24.2) * mm});
            skLineSegment(sketch, "E91.1.20", {"start": v(-14.2, 24.58) * mm, "end": v(-4.47, 7.74) * mm, "construction": true});
            skArc(sketch, "E91.1.21", {"start": v(-9.54, 12.56) * mm, "mid": v(-7.97, 13.8) * mm, "end": v(-6.1, 14.54) * mm});
            skLineSegment(sketch, "E91.1.22", {"start": v(-7.84, 10.59) * mm, "end": v(-6.72, 9.46) * mm});
            skLineSegment(sketch, "E91.1.23", {"start": v(-18.16, 20.9) * mm, "end": v(-16.89, 19.63) * mm, "construction": true});
            skArc(sketch, "E91.1.24", {"start": v(-11.24, 14.26) * mm, "mid": v(-9.17, 15.88) * mm, "end": v(-6.73, 16.86) * mm});
            skArc(sketch, "E91.1.25", {"start": v(-16.32, 19.35) * mm, "mid": v(-12.77, 22.1) * mm, "end": v(-8.6, 23.81) * mm});
            skArc(sketch, "E91.1.26", {"start": v(-14.9, 17.94) * mm, "mid": v(-11.77, 20.38) * mm, "end": v(-8.08, 21.88) * mm});
            skArc(sketch, "E91.1.27", {"start": v(-9.82, 12.85) * mm, "mid": v(-8.17, 14.15) * mm, "end": v(-6.22, 14.93) * mm});
            skLineSegment(sketch, "E91.1.28", {"start": v(-5.25, 12.09) * mm, "end": v(-4.84, 10.55) * mm});
            skArc(sketch, "E91.1.29", {"start": v(-6.17, 9.17) * mm, "mid": v(-5.58, 9.66) * mm, "end": v(-4.86, 9.93) * mm});
            skPoint(sketch, "E91.1.30", {"position": v(-8.5, 24.25) * mm});
            skPoint(sketch, "E91.1.31", {"position": v(-11.37, 14.12) * mm});
            skPoint(sketch, "E91.1.32", {"position": v(-14.76, 17.5) * mm});
            skPoint(sketch, "E91.1.33", {"position": v(-7.98, 10.72) * mm});
            skPoint(sketch, "E91.1.34", {"position": v(-6.02, 14.97) * mm});
            skPoint(sketch, "E91.1.35", {"position": v(-4.68, 9.95) * mm});
            skPoint(sketch, "E91.1.36", {"position": v(-6.54, 16.9) * mm});
            skPoint(sketch, "E91.1.37", {"position": v(-6.56, 9.3) * mm});
            skPoint(sketch, "E91.1.38", {"position": v(-13.35, 16.1) * mm});
            skPoint(sketch, "E91.1.39", {"position": v(-7.16, 19.22) * mm});
            skPoint(sketch, "E91.1.40", {"position": v(-4.78, 10.34) * mm});
            skPoint(sketch, "E91.1.41", {"position": v(-11.65, 14.4) * mm});
            skArc(sketch, "E91.1.42", {"start": v(-6.43, 9.47) * mm, "mid": v(-5.78, 10) * mm, "end": v(-4.99, 10.3) * mm});
            skPoint(sketch, "E91.1.43", {"position": v(-7.26, 19.6) * mm});
            skLineSegment(sketch, "E91.1.44", {"start": v(-5.3, 12.27) * mm, "end": v(-4.78, 10.34) * mm});
            skPoint(sketch, "E91.1.45", {"position": v(-5.3, 12.27) * mm});
            skPoint(sketch, "E91.1.46", {"position": v(-9.96, 12.7) * mm});
            skPoint(sketch, "E91.1.47", {"position": v(-16.74, 19.49) * mm});
            skPoint(sketch, "E91.1.48", {"position": v(-7.78, 21.54) * mm});
            skLineSegment(sketch, "E91.1.49", {"start": v(-9.02, 26.18) * mm, "end": v(-4.23, 8.3) * mm});
            skPoint(sketch, "E91.1.50", {"position": v(-5.4, 12.66) * mm});
            skPoint(sketch, "E91.1.51", {"position": v(-16.46, 19.2) * mm});
            skPoint(sketch, "E91.1.52", {"position": v(-9.67, 12.42) * mm});
            skLineSegment(sketch, "E91.1.53", {"start": v(-18.16, 20.9) * mm, "end": v(-5.07, 7.81) * mm});
            skPoint(sketch, "E91.1.54", {"position": v(-7.89, 21.93) * mm});
            skPoint(sketch, "E91.1.55", {"position": v(-8.4, 23.86) * mm});
            skPoint(sketch, "E91.1.56", {"position": v(-15.05, 17.8) * mm});
            skPoint(sketch, "E91.1.57", {"position": v(-8.26, 11) * mm});
            skPoint(sketch, "E91.1.58", {"position": v(-5.92, 14.59) * mm});
            skPoint(sketch, "E91.1.59", {"position": v(-13.07, 15.81) * mm});
            skPoint(sketch, "E91.1.60", {"position": v(-6.64, 17.3) * mm});
            skPoint(sketch, "E91.1.61", {"position": v(-6.28, 9.02) * mm});
            skLineSegment(sketch, "E91.1.62", {"start": v(-9.02, 26.18) * mm, "end": v(-4.23, 8.3) * mm});
            skLineSegment(sketch, "E91.1.63", {"start": v(-7.98, 10.72) * mm, "end": v(-6.56, 9.3) * mm});
            skArc(sketch, "E91.1.64", {"start": v(-7.46, 19.56) * mm, "mid": v(-7.34, 19.65) * mm, "end": v(-7.32, 19.8) * mm});
            skArc(sketch, "E91.1.65", {"start": v(-11.8, 14.54) * mm, "mid": v(-11.66, 14.49) * mm, "end": v(-11.51, 14.55) * mm});
            skArc(sketch, "E91.1.66", {"start": v(-16.89, 19.63) * mm, "mid": v(-16.75, 19.57) * mm, "end": v(-16.6, 19.63) * mm});
            skArc(sketch, "E91.1.67", {"start": v(-11.24, 14.26) * mm, "mid": v(-11.3, 14.12) * mm, "end": v(-11.23, 13.98) * mm});
            skLineSegment(sketch, "E91.1.68", {"start": v(-8.5, 24.25) * mm, "end": v(-8.4, 23.86) * mm, "construction": true});
            skLineSegment(sketch, "E91.1.69", {"start": v(-9.96, 12.7) * mm, "end": v(-9.67, 12.42) * mm});
            skArc(sketch, "E91.1.70", {"start": v(-8.35, 23.67) * mm, "mid": v(-8.44, 23.8) * mm, "end": v(-8.6, 23.81) * mm});
            skArc(sketch, "E91.1.71", {"start": v(-8.7, 24.2) * mm, "mid": v(-8.58, 24.29) * mm, "end": v(-8.56, 24.44) * mm});
            skLineSegment(sketch, "E91.1.72", {"start": v(-11.65, 14.4) * mm, "end": v(-11.37, 14.12) * mm});
            skLineSegment(sketch, "E91.1.73", {"start": v(-6.64, 17.3) * mm, "end": v(-6.54, 16.9) * mm});
            skArc(sketch, "E91.1.74", {"start": v(-10.1, 12.85) * mm, "mid": v(-9.96, 12.79) * mm, "end": v(-9.82, 12.85) * mm});
            skArc(sketch, "E91.1.75", {"start": v(-15.2, 17.94) * mm, "mid": v(-15.05, 17.88) * mm, "end": v(-14.9, 17.94) * mm});
            skArc(sketch, "E91.1.76", {"start": v(-6.84, 17.24) * mm, "mid": v(-6.72, 17.34) * mm, "end": v(-6.7, 17.5) * mm});
            skArc(sketch, "E91.1.77", {"start": v(-9.54, 12.56) * mm, "mid": v(-9.6, 12.42) * mm, "end": v(-9.54, 12.28) * mm});
            skArc(sketch, "E91.1.78", {"start": v(-13.5, 16.24) * mm, "mid": v(-13.35, 16.18) * mm, "end": v(-13.21, 16.24) * mm});
            skArc(sketch, "E91.1.79", {"start": v(-6.49, 16.72) * mm, "mid": v(-6.58, 16.84) * mm, "end": v(-6.73, 16.86) * mm});
            skArc(sketch, "E91.1.80", {"start": v(-8.4, 11.15) * mm, "mid": v(-8.26, 11.1) * mm, "end": v(-8.12, 11.16) * mm});
            skLineSegment(sketch, "E91.1.81", {"start": v(-4.78, 10.34) * mm, "end": v(-4.68, 9.95) * mm});
            skArc(sketch, "E91.1.82", {"start": v(-8.08, 21.88) * mm, "mid": v(-7.96, 21.97) * mm, "end": v(-7.94, 22.12) * mm});
            skArc(sketch, "E91.1.83", {"start": v(-5.25, 12.09) * mm, "mid": v(-5.34, 12.2) * mm, "end": v(-5.49, 12.23) * mm});
            skLineSegment(sketch, "E91.1.84", {"start": v(-7.26, 19.6) * mm, "end": v(-7.16, 19.22) * mm});
            skArc(sketch, "E91.1.85", {"start": v(-7.1, 19.03) * mm, "mid": v(-7.2, 19.16) * mm, "end": v(-7.35, 19.18) * mm});
            skArc(sketch, "E91.1.86", {"start": v(-5.6, 12.61) * mm, "mid": v(-5.48, 12.7) * mm, "end": v(-5.46, 12.86) * mm});
            skArc(sketch, "E91.1.87", {"start": v(-7.73, 21.35) * mm, "mid": v(-7.82, 21.47) * mm, "end": v(-7.97, 21.5) * mm});
            skArc(sketch, "E91.1.88", {"start": v(-12.93, 15.96) * mm, "mid": v(-12.99, 15.81) * mm, "end": v(-12.93, 15.67) * mm});
            skArc(sketch, "E91.1.89", {"start": v(-4.99, 10.3) * mm, "mid": v(-4.86, 10.4) * mm, "end": v(-4.84, 10.55) * mm});
            skLineSegment(sketch, "E91.1.90", {"start": v(-7.89, 21.93) * mm, "end": v(-7.78, 21.54) * mm});
            skLineSegment(sketch, "E91.1.91", {"start": v(-13.35, 16.1) * mm, "end": v(-13.07, 15.81) * mm});
            skArc(sketch, "E91.1.92", {"start": v(-5.87, 14.4) * mm, "mid": v(-5.96, 14.52) * mm, "end": v(-6.1, 14.54) * mm});
            skArc(sketch, "E91.1.93", {"start": v(-7.85, 10.87) * mm, "mid": v(-7.9, 10.73) * mm, "end": v(-7.84, 10.59) * mm});
            skArc(sketch, "E91.1.94", {"start": v(-16.32, 19.35) * mm, "mid": v(-16.38, 19.2) * mm, "end": v(-16.32, 19.07) * mm});
            skLineSegment(sketch, "E91.1.95", {"start": v(-15.05, 17.8) * mm, "end": v(-14.76, 17.5) * mm});
            skLineSegment(sketch, "E91.1.96", {"start": v(-16.74, 19.49) * mm, "end": v(-16.46, 19.2) * mm, "construction": true});
            skArc(sketch, "E91.1.97", {"start": v(-6.22, 14.93) * mm, "mid": v(-6.1, 15.02) * mm, "end": v(-6.08, 15.17) * mm});
            skLineSegment(sketch, "E91.1.98", {"start": v(-5.4, 12.66) * mm, "end": v(-5.3, 12.27) * mm});
            skLineSegment(sketch, "E91.1.99", {"start": v(-8.26, 11) * mm, "end": v(-7.98, 10.72) * mm});
            skLineSegment(sketch, "E91.1.100", {"start": v(-6.02, 14.97) * mm, "end": v(-5.92, 14.59) * mm});
            skArc(sketch, "E91.1.101", {"start": v(-14.63, 17.65) * mm, "mid": v(-14.68, 17.51) * mm, "end": v(-14.63, 17.37) * mm});
            skArc(sketch, "E91.1.102", {"start": v(-4.63, 9.78) * mm, "mid": v(-4.72, 9.9) * mm, "end": v(-4.86, 9.93) * mm});
            skLineSegment(sketch, "E91.1.103", {"start": v(-6.56, 9.3) * mm, "end": v(-6.28, 9.02) * mm});
            skArc(sketch, "E91.1.104", {"start": v(-6.72, 9.46) * mm, "mid": v(-6.57, 9.4) * mm, "end": v(-6.43, 9.47) * mm});
            skArc(sketch, "E91.1.105", {"start": v(-6.17, 9.17) * mm, "mid": v(-6.21, 9.03) * mm, "end": v(-6.15, 8.9) * mm});
            skLineSegment(sketch, "E91.1.106", {"start": v(-4.78, 10.34) * mm, "end": v(-4.68, 9.95) * mm});
            skLineSegment(sketch, "E91.1.107", {"start": v(-6.56, 9.3) * mm, "end": v(-6.28, 9.02) * mm});
            skLineSegment(sketch, "E91.2.0", {"start": v(-9.78, 4.63) * mm, "end": v(-8.3, 4.23) * mm});
            skArc(sketch, "E91.2.1", {"start": v(-12.23, 5.49) * mm, "mid": v(-11.73, 6.77) * mm, "end": v(-10.87, 7.85) * mm});
            skLineSegment(sketch, "E91.2.2", {"start": v(-17.37, 14.63) * mm, "end": v(-16.24, 13.5) * mm});
            skLineSegment(sketch, "E91.2.3", {"start": v(-19.07, 16.32) * mm, "end": v(-17.94, 15.2) * mm});
            skArc(sketch, "E91.2.4", {"start": v(-19.56, 7.46) * mm, "mid": v(-18.3, 10.57) * mm, "end": v(-16.24, 13.21) * mm});
            skLineSegment(sketch, "E91.2.5", {"start": v(-8.9, 6.15) * mm, "end": v(-7.81, 5.07) * mm});
            skArc(sketch, "E91.2.6", {"start": v(-21.5, 7.97) * mm, "mid": v(-20.03, 11.57) * mm, "end": v(-17.65, 14.63) * mm});
            skArc(sketch, "E91.2.7", {"start": v(-12.61, 5.6) * mm, "mid": v(-12.07, 6.97) * mm, "end": v(-11.16, 8.12) * mm});
            skLineSegment(sketch, "E91.2.8", {"start": v(-20.9, 18.16) * mm, "end": v(-19.63, 16.89) * mm, "construction": true});
            skLineSegment(sketch, "E91.2.9", {"start": v(-14.4, 5.87) * mm, "end": v(-12.86, 5.46) * mm});
            skLineSegment(sketch, "E91.2.10", {"start": v(-16.72, 6.49) * mm, "end": v(-15.17, 6.08) * mm});
            skLineSegment(sketch, "E91.2.11", {"start": v(-13.98, 11.23) * mm, "end": v(-12.85, 10.1) * mm});
            skArc(sketch, "E91.2.12", {"start": v(-17.24, 6.84) * mm, "mid": v(-16.22, 9.37) * mm, "end": v(-14.55, 11.51) * mm});
            skLineSegment(sketch, "E91.2.13", {"start": v(-15.67, 12.93) * mm, "end": v(-14.54, 11.8) * mm});
            skArc(sketch, "E91.2.14", {"start": v(-19.18, 7.35) * mm, "mid": v(-17.95, 10.37) * mm, "end": v(-15.96, 12.93) * mm});
            skLineSegment(sketch, "E91.2.15", {"start": v(-12.28, 9.54) * mm, "end": v(-11.15, 8.4) * mm});
            skLineSegment(sketch, "E91.2.16", {"start": v(-19.03, 7.1) * mm, "end": v(-17.5, 6.7) * mm});
            skLineSegment(sketch, "E91.2.17", {"start": v(-21.35, 7.73) * mm, "end": v(-19.8, 7.32) * mm});
            skLineSegment(sketch, "E91.2.18", {"start": v(-23.67, 8.35) * mm, "end": v(-22.12, 7.94) * mm});
            skArc(sketch, "E91.2.19", {"start": v(-24.2, 8.7) * mm, "mid": v(-22.46, 12.97) * mm, "end": v(-19.63, 16.6) * mm});
            skLineSegment(sketch, "E91.2.20", {"start": v(-24.58, 14.2) * mm, "end": v(-7.74, 4.47) * mm, "construction": true});
            skArc(sketch, "E91.2.21", {"start": v(-14.54, 6.1) * mm, "mid": v(-13.8, 7.97) * mm, "end": v(-12.56, 9.54) * mm});
            skLineSegment(sketch, "E91.2.22", {"start": v(-12.09, 5.25) * mm, "end": v(-10.55, 4.84) * mm});
            skLineSegment(sketch, "E91.2.23", {"start": v(-26.18, 9.02) * mm, "end": v(-24.44, 8.56) * mm, "construction": true});
            skArc(sketch, "E91.2.24", {"start": v(-16.86, 6.73) * mm, "mid": v(-15.88, 9.17) * mm, "end": v(-14.26, 11.24) * mm});
            skArc(sketch, "E91.2.25", {"start": v(-23.81, 8.6) * mm, "mid": v(-22.1, 12.77) * mm, "end": v(-19.35, 16.32) * mm});
            skArc(sketch, "E91.2.26", {"start": v(-21.88, 8.08) * mm, "mid": v(-20.38, 11.77) * mm, "end": v(-17.94, 14.9) * mm});
            skArc(sketch, "E91.2.27", {"start": v(-14.93, 6.22) * mm, "mid": v(-14.15, 8.17) * mm, "end": v(-12.85, 9.82) * mm});
            skLineSegment(sketch, "E91.2.28", {"start": v(-10.59, 7.84) * mm, "end": v(-9.46, 6.72) * mm});
            skArc(sketch, "E91.2.29", {"start": v(-9.93, 4.86) * mm, "mid": v(-9.66, 5.58) * mm, "end": v(-9.17, 6.17) * mm});
            skPoint(sketch, "E91.2.30", {"position": v(-19.49, 16.74) * mm});
            skPoint(sketch, "E91.2.31", {"position": v(-16.9, 6.54) * mm});
            skPoint(sketch, "E91.2.32", {"position": v(-21.54, 7.78) * mm});
            skPoint(sketch, "E91.2.33", {"position": v(-12.27, 5.3) * mm});
            skPoint(sketch, "E91.2.34", {"position": v(-12.7, 9.96) * mm});
            skPoint(sketch, "E91.2.35", {"position": v(-9.02, 6.28) * mm});
            skPoint(sketch, "E91.2.36", {"position": v(-14.12, 11.37) * mm});
            skPoint(sketch, "E91.2.37", {"position": v(-10.34, 4.78) * mm});
            skPoint(sketch, "E91.2.38", {"position": v(-19.6, 7.26) * mm});
            skPoint(sketch, "E91.2.39", {"position": v(-15.81, 13.07) * mm});
            skPoint(sketch, "E91.2.40", {"position": v(-9.3, 6.56) * mm});
            skPoint(sketch, "E91.2.41", {"position": v(-17.3, 6.64) * mm});
            skArc(sketch, "E91.2.42", {"start": v(-10.3, 4.99) * mm, "mid": v(-10, 5.78) * mm, "end": v(-9.47, 6.43) * mm});
            skPoint(sketch, "E91.2.43", {"position": v(-16.1, 13.35) * mm});
            skLineSegment(sketch, "E91.2.44", {"start": v(-10.72, 7.98) * mm, "end": v(-9.3, 6.56) * mm});
            skPoint(sketch, "E91.2.45", {"position": v(-10.72, 7.98) * mm});
            skPoint(sketch, "E91.2.46", {"position": v(-14.97, 6.02) * mm});
            skPoint(sketch, "E91.2.47", {"position": v(-24.25, 8.5) * mm});
            skPoint(sketch, "E91.2.48", {"position": v(-17.5, 14.76) * mm});
            skLineSegment(sketch, "E91.2.49", {"start": v(-20.9, 18.16) * mm, "end": v(-7.81, 5.07) * mm});
            skPoint(sketch, "E91.2.50", {"position": v(-11, 8.26) * mm});
            skPoint(sketch, "E91.2.51", {"position": v(-23.86, 8.4) * mm});
            skPoint(sketch, "E91.2.52", {"position": v(-14.59, 5.92) * mm});
            skLineSegment(sketch, "E91.2.53", {"start": v(-26.18, 9.02) * mm, "end": v(-8.3, 4.23) * mm});
            skPoint(sketch, "E91.2.54", {"position": v(-17.8, 15.05) * mm});
            skPoint(sketch, "E91.2.55", {"position": v(-19.2, 16.46) * mm});
            skPoint(sketch, "E91.2.56", {"position": v(-21.93, 7.89) * mm});
            skPoint(sketch, "E91.2.57", {"position": v(-12.66, 5.4) * mm});
            skPoint(sketch, "E91.2.58", {"position": v(-12.42, 9.67) * mm});
            skPoint(sketch, "E91.2.59", {"position": v(-19.22, 7.16) * mm});
            skPoint(sketch, "E91.2.60", {"position": v(-14.4, 11.65) * mm});
            skPoint(sketch, "E91.2.61", {"position": v(-9.95, 4.68) * mm});
            skLineSegment(sketch, "E91.2.62", {"start": v(-20.9, 18.16) * mm, "end": v(-7.81, 5.07) * mm});
            skLineSegment(sketch, "E91.2.63", {"start": v(-12.27, 5.3) * mm, "end": v(-10.34, 4.78) * mm});
            skArc(sketch, "E91.2.64", {"start": v(-16.24, 13.21) * mm, "mid": v(-16.18, 13.35) * mm, "end": v(-16.24, 13.5) * mm});
            skArc(sketch, "E91.2.65", {"start": v(-17.5, 6.7) * mm, "mid": v(-17.34, 6.72) * mm, "end": v(-17.24, 6.84) * mm});
            skArc(sketch, "E91.2.66", {"start": v(-24.44, 8.56) * mm, "mid": v(-24.29, 8.58) * mm, "end": v(-24.2, 8.7) * mm});
            skArc(sketch, "E91.2.67", {"start": v(-16.86, 6.73) * mm, "mid": v(-16.84, 6.58) * mm, "end": v(-16.72, 6.49) * mm});
            skLineSegment(sketch, "E91.2.68", {"start": v(-19.49, 16.74) * mm, "end": v(-19.2, 16.46) * mm, "construction": true});
            skLineSegment(sketch, "E91.2.69", {"start": v(-14.97, 6.02) * mm, "end": v(-14.59, 5.92) * mm});
            skArc(sketch, "E91.2.70", {"start": v(-19.07, 16.32) * mm, "mid": v(-19.2, 16.38) * mm, "end": v(-19.35, 16.32) * mm});
            skArc(sketch, "E91.2.71", {"start": v(-19.63, 16.6) * mm, "mid": v(-19.57, 16.75) * mm, "end": v(-19.63, 16.89) * mm});
            skLineSegment(sketch, "E91.2.72", {"start": v(-17.3, 6.64) * mm, "end": v(-16.9, 6.54) * mm});
            skLineSegment(sketch, "E91.2.73", {"start": v(-14.4, 11.65) * mm, "end": v(-14.12, 11.37) * mm});
            skArc(sketch, "E91.2.74", {"start": v(-15.17, 6.08) * mm, "mid": v(-15.02, 6.1) * mm, "end": v(-14.93, 6.22) * mm});
            skArc(sketch, "E91.2.75", {"start": v(-22.12, 7.94) * mm, "mid": v(-21.97, 7.96) * mm, "end": v(-21.88, 8.08) * mm});
            skArc(sketch, "E91.2.76", {"start": v(-14.55, 11.51) * mm, "mid": v(-14.49, 11.66) * mm, "end": v(-14.54, 11.8) * mm});
            skArc(sketch, "E91.2.77", {"start": v(-14.54, 6.1) * mm, "mid": v(-14.52, 5.96) * mm, "end": v(-14.4, 5.87) * mm});
            skArc(sketch, "E91.2.78", {"start": v(-19.8, 7.32) * mm, "mid": v(-19.65, 7.34) * mm, "end": v(-19.56, 7.46) * mm});
            skArc(sketch, "E91.2.79", {"start": v(-13.98, 11.23) * mm, "mid": v(-14.12, 11.3) * mm, "end": v(-14.26, 11.24) * mm});
            skArc(sketch, "E91.2.80", {"start": v(-12.86, 5.46) * mm, "mid": v(-12.7, 5.48) * mm, "end": v(-12.61, 5.6) * mm});
            skLineSegment(sketch, "E91.2.81", {"start": v(-9.3, 6.56) * mm, "end": v(-9.02, 6.28) * mm});
            skArc(sketch, "E91.2.82", {"start": v(-17.94, 14.9) * mm, "mid": v(-17.88, 15.05) * mm, "end": v(-17.94, 15.2) * mm});
            skArc(sketch, "E91.2.83", {"start": v(-10.59, 7.84) * mm, "mid": v(-10.73, 7.9) * mm, "end": v(-10.87, 7.85) * mm});
            skLineSegment(sketch, "E91.2.84", {"start": v(-16.1, 13.35) * mm, "end": v(-15.81, 13.07) * mm});
            skArc(sketch, "E91.2.85", {"start": v(-15.67, 12.93) * mm, "mid": v(-15.81, 12.99) * mm, "end": v(-15.96, 12.93) * mm});
            skArc(sketch, "E91.2.86", {"start": v(-11.16, 8.12) * mm, "mid": v(-11.1, 8.26) * mm, "end": v(-11.15, 8.4) * mm});
            skArc(sketch, "E91.2.87", {"start": v(-17.37, 14.63) * mm, "mid": v(-17.51, 14.68) * mm, "end": v(-17.65, 14.63) * mm});
            skArc(sketch, "E91.2.88", {"start": v(-19.18, 7.35) * mm, "mid": v(-19.16, 7.2) * mm, "end": v(-19.03, 7.1) * mm});
            skArc(sketch, "E91.2.89", {"start": v(-9.47, 6.43) * mm, "mid": v(-9.4, 6.57) * mm, "end": v(-9.46, 6.72) * mm});
            skLineSegment(sketch, "E91.2.90", {"start": v(-17.8, 15.05) * mm, "end": v(-17.5, 14.76) * mm});
            skLineSegment(sketch, "E91.2.91", {"start": v(-19.6, 7.26) * mm, "end": v(-19.22, 7.16) * mm});
            skArc(sketch, "E91.2.92", {"start": v(-12.28, 9.54) * mm, "mid": v(-12.42, 9.6) * mm, "end": v(-12.56, 9.54) * mm});
            skArc(sketch, "E91.2.93", {"start": v(-12.23, 5.49) * mm, "mid": v(-12.2, 5.34) * mm, "end": v(-12.09, 5.25) * mm});
            skArc(sketch, "E91.2.94", {"start": v(-23.81, 8.6) * mm, "mid": v(-23.8, 8.44) * mm, "end": v(-23.67, 8.35) * mm});
            skLineSegment(sketch, "E91.2.95", {"start": v(-21.93, 7.89) * mm, "end": v(-21.54, 7.78) * mm});
            skLineSegment(sketch, "E91.2.96", {"start": v(-24.25, 8.5) * mm, "end": v(-23.86, 8.4) * mm, "construction": true});
            skArc(sketch, "E91.2.97", {"start": v(-12.85, 9.82) * mm, "mid": v(-12.79, 9.96) * mm, "end": v(-12.85, 10.1) * mm});
            skLineSegment(sketch, "E91.2.98", {"start": v(-11, 8.26) * mm, "end": v(-10.72, 7.98) * mm});
            skLineSegment(sketch, "E91.2.99", {"start": v(-12.66, 5.4) * mm, "end": v(-12.27, 5.3) * mm});
            skLineSegment(sketch, "E91.2.100", {"start": v(-12.7, 9.96) * mm, "end": v(-12.42, 9.67) * mm});
            skArc(sketch, "E91.2.101", {"start": v(-21.5, 7.97) * mm, "mid": v(-21.47, 7.82) * mm, "end": v(-21.35, 7.73) * mm});
            skArc(sketch, "E91.2.102", {"start": v(-8.9, 6.15) * mm, "mid": v(-9.03, 6.21) * mm, "end": v(-9.17, 6.17) * mm});
            skLineSegment(sketch, "E91.2.103", {"start": v(-10.34, 4.78) * mm, "end": v(-9.95, 4.68) * mm});
            skArc(sketch, "E91.2.104", {"start": v(-10.55, 4.84) * mm, "mid": v(-10.4, 4.86) * mm, "end": v(-10.3, 4.99) * mm});
            skArc(sketch, "E91.2.105", {"start": v(-9.93, 4.86) * mm, "mid": v(-9.9, 4.72) * mm, "end": v(-9.78, 4.63) * mm});
            skLineSegment(sketch, "E91.2.106", {"start": v(-9.3, 6.56) * mm, "end": v(-9.02, 6.28) * mm});
            skLineSegment(sketch, "E91.2.107", {"start": v(-10.34, 4.78) * mm, "end": v(-9.95, 4.68) * mm});
            skLineSegment(sketch, "E91.3.0", {"start": v(-10.79, -0.88) * mm, "end": v(-9.3, -0.48) * mm});
            skArc(sketch, "E91.3.1", {"start": v(-13.33, -1.36) * mm, "mid": v(-13.54, 0) * mm, "end": v(-13.33, 1.36) * mm});
            skLineSegment(sketch, "E91.3.2", {"start": v(-22.36, 3.98) * mm, "end": v(-20.81, 3.57) * mm});
            skLineSegment(sketch, "E91.3.3", {"start": v(-24.67, 4.6) * mm, "end": v(-23.13, 4.19) * mm});
            skArc(sketch, "E91.3.4", {"start": v(-20.67, -3.32) * mm, "mid": v(-21.13, 0) * mm, "end": v(-20.67, 3.32) * mm});
            skLineSegment(sketch, "E91.3.5", {"start": v(-10.79, 0.88) * mm, "end": v(-9.3, 0.48) * mm});
            skArc(sketch, "E91.3.6", {"start": v(-22.6, -3.84) * mm, "mid": v(-23.13, 0) * mm, "end": v(-22.6, 3.84) * mm});
            skArc(sketch, "E91.3.7", {"start": v(-13.72, -1.45) * mm, "mid": v(-13.94, 0) * mm, "end": v(-13.72, 1.45) * mm});
            skLineSegment(sketch, "E91.3.8", {"start": v(-27.18, 5.27) * mm, "end": v(-25.45, 4.8) * mm, "construction": true});
            skLineSegment(sketch, "E91.3.9", {"start": v(-15.4, -2.12) * mm, "end": v(-13.86, -1.7) * mm});
            skLineSegment(sketch, "E91.3.10", {"start": v(-17.72, -2.74) * mm, "end": v(-16.18, -2.33) * mm});
            skLineSegment(sketch, "E91.3.11", {"start": v(-17.72, 2.74) * mm, "end": v(-16.18, 2.33) * mm});
            skArc(sketch, "E91.3.12", {"start": v(-18.35, -2.7) * mm, "mid": v(-18.73, 0) * mm, "end": v(-18.35, 2.7) * mm});
            skLineSegment(sketch, "E91.3.13", {"start": v(-20.04, 3.36) * mm, "end": v(-18.5, 2.95) * mm});
            skArc(sketch, "E91.3.14", {"start": v(-20.28, -3.22) * mm, "mid": v(-20.73, 0) * mm, "end": v(-20.28, 3.22) * mm});
            skLineSegment(sketch, "E91.3.15", {"start": v(-15.4, 2.12) * mm, "end": v(-13.86, 1.7) * mm});
            skLineSegment(sketch, "E91.3.16", {"start": v(-20.04, -3.36) * mm, "end": v(-18.5, -2.95) * mm});
            skLineSegment(sketch, "E91.3.17", {"start": v(-22.36, -3.98) * mm, "end": v(-20.81, -3.57) * mm});
            skLineSegment(sketch, "E91.3.18", {"start": v(-24.67, -4.6) * mm, "end": v(-23.13, -4.19) * mm});
            skArc(sketch, "E91.3.19", {"start": v(-25.3, -4.56) * mm, "mid": v(-25.93, 0) * mm, "end": v(-25.3, 4.56) * mm});
            skLineSegment(sketch, "E91.3.20", {"start": v(-28.38, 0) * mm, "end": v(-8.93, 0) * mm, "construction": true});
            skArc(sketch, "E91.3.21", {"start": v(-15.65, -1.98) * mm, "mid": v(-15.94, 0) * mm, "end": v(-15.65, 1.98) * mm});
            skLineSegment(sketch, "E91.3.22", {"start": v(-13.1, -1.5) * mm, "end": v(-11.56, -1.09) * mm});
            skLineSegment(sketch, "E91.3.23", {"start": v(-27.18, -5.27) * mm, "end": v(-25.45, -4.8) * mm, "construction": true});
            skArc(sketch, "E91.3.24", {"start": v(-17.97, -2.6) * mm, "mid": v(-18.33, 0) * mm, "end": v(-17.97, 2.6) * mm});
            skArc(sketch, "E91.3.25", {"start": v(-24.92, -4.46) * mm, "mid": v(-25.53, 0) * mm, "end": v(-24.92, 4.46) * mm});
            skArc(sketch, "E91.3.26", {"start": v(-22.99, -3.94) * mm, "mid": v(-23.53, 0) * mm, "end": v(-22.99, 3.94) * mm});
            skArc(sketch, "E91.3.27", {"start": v(-16.04, -2.08) * mm, "mid": v(-16.34, 0) * mm, "end": v(-16.04, 2.08) * mm});
            skLineSegment(sketch, "E91.3.28", {"start": v(-13.1, 1.5) * mm, "end": v(-11.56, 1.09) * mm});
            skArc(sketch, "E91.3.29", {"start": v(-11.03, -0.75) * mm, "mid": v(-11.16, 0) * mm, "end": v(-11.03, 0.75) * mm});
            skPoint(sketch, "E91.3.30", {"position": v(-25.25, 4.76) * mm});
            skPoint(sketch, "E91.3.31", {"position": v(-17.9, -2.79) * mm});
            skPoint(sketch, "E91.3.32", {"position": v(-22.55, -4.03) * mm});
            skPoint(sketch, "E91.3.33", {"position": v(-13.27, -1.55) * mm});
            skPoint(sketch, "E91.3.34", {"position": v(-15.98, 2.27) * mm});
            skPoint(sketch, "E91.3.35", {"position": v(-10.96, 0.93) * mm});
            skPoint(sketch, "E91.3.36", {"position": v(-17.9, 2.79) * mm});
            skPoint(sketch, "E91.3.37", {"position": v(-11.34, -1.03) * mm});
            skPoint(sketch, "E91.3.38", {"position": v(-20.61, -3.51) * mm});
            skPoint(sketch, "E91.3.39", {"position": v(-20.23, 3.41) * mm});
            skPoint(sketch, "E91.3.40", {"position": v(-11.34, 1.03) * mm});
            skPoint(sketch, "E91.3.41", {"position": v(-18.3, -2.9) * mm});
            skArc(sketch, "E91.3.42", {"start": v(-11.42, -0.83) * mm, "mid": v(-11.55, 0) * mm, "end": v(-11.42, 0.83) * mm});
            skPoint(sketch, "E91.3.43", {"position": v(-20.61, 3.51) * mm});
            skLineSegment(sketch, "E91.3.44", {"start": v(-13.27, 1.55) * mm, "end": v(-11.34, 1.03) * mm});
            skPoint(sketch, "E91.3.45", {"position": v(-13.27, 1.55) * mm});
            skPoint(sketch, "E91.3.46", {"position": v(-15.98, -2.27) * mm});
            skPoint(sketch, "E91.3.47", {"position": v(-25.25, -4.76) * mm});
            skPoint(sketch, "E91.3.48", {"position": v(-22.55, 4.03) * mm});
            skLineSegment(sketch, "E91.3.49", {"start": v(-27.18, 5.27) * mm, "end": v(-9.3, 0.48) * mm});
            skPoint(sketch, "E91.3.50", {"position": v(-13.66, 1.65) * mm});
            skPoint(sketch, "E91.3.51", {"position": v(-24.86, -4.65) * mm});
            skPoint(sketch, "E91.3.52", {"position": v(-15.6, -2.17) * mm});
            skLineSegment(sketch, "E91.3.53", {"start": v(-27.18, -5.27) * mm, "end": v(-9.3, -0.48) * mm});
            skPoint(sketch, "E91.3.54", {"position": v(-22.93, 4.14) * mm});
            skPoint(sketch, "E91.3.55", {"position": v(-24.86, 4.65) * mm});
            skPoint(sketch, "E91.3.56", {"position": v(-22.93, -4.14) * mm});
            skPoint(sketch, "E91.3.57", {"position": v(-13.66, -1.65) * mm});
            skPoint(sketch, "E91.3.58", {"position": v(-15.6, 2.17) * mm});
            skPoint(sketch, "E91.3.59", {"position": v(-20.23, -3.41) * mm});
            skPoint(sketch, "E91.3.60", {"position": v(-18.3, 2.9) * mm});
            skPoint(sketch, "E91.3.61", {"position": v(-10.96, -0.93) * mm});
            skLineSegment(sketch, "E91.3.62", {"start": v(-27.18, 5.27) * mm, "end": v(-9.3, 0.48) * mm});
            skLineSegment(sketch, "E91.3.63", {"start": v(-13.27, -1.55) * mm, "end": v(-11.34, -1.03) * mm});
            skArc(sketch, "E91.3.64", {"start": v(-20.67, 3.32) * mm, "mid": v(-20.69, 3.47) * mm, "end": v(-20.81, 3.57) * mm});
            skArc(sketch, "E91.3.65", {"start": v(-18.5, -2.95) * mm, "mid": v(-18.37, -2.85) * mm, "end": v(-18.35, -2.7) * mm});
            skArc(sketch, "E91.3.66", {"start": v(-25.45, -4.8) * mm, "mid": v(-25.33, -4.71) * mm, "end": v(-25.3, -4.56) * mm});
            skArc(sketch, "E91.3.67", {"start": v(-17.97, -2.6) * mm, "mid": v(-17.87, -2.72) * mm, "end": v(-17.72, -2.74) * mm});
            skLineSegment(sketch, "E91.3.68", {"start": v(-25.25, 4.76) * mm, "end": v(-24.86, 4.65) * mm, "construction": true});
            skLineSegment(sketch, "E91.3.69", {"start": v(-15.98, -2.27) * mm, "end": v(-15.6, -2.17) * mm});
            skArc(sketch, "E91.3.70", {"start": v(-24.67, 4.6) * mm, "mid": v(-24.83, 4.58) * mm, "end": v(-24.92, 4.46) * mm});
            skArc(sketch, "E91.3.71", {"start": v(-25.3, 4.56) * mm, "mid": v(-25.33, 4.71) * mm, "end": v(-25.45, 4.8) * mm});
            skLineSegment(sketch, "E91.3.72", {"start": v(-18.3, -2.9) * mm, "end": v(-17.9, -2.79) * mm});
            skLineSegment(sketch, "E91.3.73", {"start": v(-18.3, 2.9) * mm, "end": v(-17.9, 2.79) * mm});
            skArc(sketch, "E91.3.74", {"start": v(-16.18, -2.33) * mm, "mid": v(-16.06, -2.23) * mm, "end": v(-16.04, -2.08) * mm});
            skArc(sketch, "E91.3.75", {"start": v(-23.13, -4.19) * mm, "mid": v(-23, -4.1) * mm, "end": v(-22.99, -3.94) * mm});
            skArc(sketch, "E91.3.76", {"start": v(-18.35, 2.7) * mm, "mid": v(-18.37, 2.85) * mm, "end": v(-18.5, 2.95) * mm});
            skArc(sketch, "E91.3.77", {"start": v(-15.65, -1.98) * mm, "mid": v(-15.56, -2.1) * mm, "end": v(-15.4, -2.12) * mm});
            skArc(sketch, "E91.3.78", {"start": v(-20.81, -3.57) * mm, "mid": v(-20.69, -3.47) * mm, "end": v(-20.67, -3.32) * mm});
            skArc(sketch, "E91.3.79", {"start": v(-17.72, 2.74) * mm, "mid": v(-17.87, 2.72) * mm, "end": v(-17.97, 2.6) * mm});
            skArc(sketch, "E91.3.80", {"start": v(-13.86, -1.7) * mm, "mid": v(-13.74, -1.6) * mm, "end": v(-13.72, -1.45) * mm});
            skLineSegment(sketch, "E91.3.81", {"start": v(-11.34, 1.03) * mm, "end": v(-10.96, 0.93) * mm});
            skArc(sketch, "E91.3.82", {"start": v(-22.99, 3.94) * mm, "mid": v(-23, 4.1) * mm, "end": v(-23.13, 4.19) * mm});
            skArc(sketch, "E91.3.83", {"start": v(-13.1, 1.5) * mm, "mid": v(-13.24, 1.48) * mm, "end": v(-13.33, 1.36) * mm});
            skLineSegment(sketch, "E91.3.84", {"start": v(-20.61, 3.51) * mm, "end": v(-20.23, 3.41) * mm});
            skArc(sketch, "E91.3.85", {"start": v(-20.04, 3.36) * mm, "mid": v(-20.19, 3.34) * mm, "end": v(-20.28, 3.22) * mm});
            skArc(sketch, "E91.3.86", {"start": v(-13.72, 1.45) * mm, "mid": v(-13.74, 1.6) * mm, "end": v(-13.86, 1.7) * mm});
            skArc(sketch, "E91.3.87", {"start": v(-22.36, 3.98) * mm, "mid": v(-22.5, 3.96) * mm, "end": v(-22.6, 3.84) * mm});
            skArc(sketch, "E91.3.88", {"start": v(-20.28, -3.22) * mm, "mid": v(-20.19, -3.34) * mm, "end": v(-20.04, -3.36) * mm});
            skArc(sketch, "E91.3.89", {"start": v(-11.42, 0.83) * mm, "mid": v(-11.43, 0.99) * mm, "end": v(-11.56, 1.09) * mm});
            skLineSegment(sketch, "E91.3.90", {"start": v(-22.93, 4.14) * mm, "end": v(-22.55, 4.03) * mm});
            skLineSegment(sketch, "E91.3.91", {"start": v(-20.61, -3.51) * mm, "end": v(-20.23, -3.41) * mm});
            skArc(sketch, "E91.3.92", {"start": v(-15.4, 2.12) * mm, "mid": v(-15.56, 2.1) * mm, "end": v(-15.65, 1.98) * mm});
            skArc(sketch, "E91.3.93", {"start": v(-13.33, -1.36) * mm, "mid": v(-13.24, -1.48) * mm, "end": v(-13.1, -1.5) * mm});
            skArc(sketch, "E91.3.94", {"start": v(-24.92, -4.46) * mm, "mid": v(-24.83, -4.58) * mm, "end": v(-24.67, -4.6) * mm});
            skLineSegment(sketch, "E91.3.95", {"start": v(-22.93, -4.14) * mm, "end": v(-22.55, -4.03) * mm});
            skLineSegment(sketch, "E91.3.96", {"start": v(-25.25, -4.76) * mm, "end": v(-24.86, -4.65) * mm, "construction": true});
            skArc(sketch, "E91.3.97", {"start": v(-16.04, 2.08) * mm, "mid": v(-16.06, 2.23) * mm, "end": v(-16.18, 2.33) * mm});
            skLineSegment(sketch, "E91.3.98", {"start": v(-13.66, 1.65) * mm, "end": v(-13.27, 1.55) * mm});
            skLineSegment(sketch, "E91.3.99", {"start": v(-13.66, -1.65) * mm, "end": v(-13.27, -1.55) * mm});
            skLineSegment(sketch, "E91.3.100", {"start": v(-15.98, 2.27) * mm, "end": v(-15.6, 2.17) * mm});
            skArc(sketch, "E91.3.101", {"start": v(-22.6, -3.84) * mm, "mid": v(-22.5, -3.96) * mm, "end": v(-22.36, -3.98) * mm});
            skArc(sketch, "E91.3.102", {"start": v(-10.79, 0.88) * mm, "mid": v(-10.93, 0.86) * mm, "end": v(-11.03, 0.75) * mm});
            skLineSegment(sketch, "E91.3.103", {"start": v(-11.34, -1.03) * mm, "end": v(-10.96, -0.93) * mm});
            skArc(sketch, "E91.3.104", {"start": v(-11.56, -1.09) * mm, "mid": v(-11.43, -0.99) * mm, "end": v(-11.42, -0.83) * mm});
            skArc(sketch, "E91.3.105", {"start": v(-11.03, -0.75) * mm, "mid": v(-10.93, -0.86) * mm, "end": v(-10.79, -0.88) * mm});
            skLineSegment(sketch, "E91.3.106", {"start": v(-11.34, 1.03) * mm, "end": v(-10.96, 0.93) * mm});
            skLineSegment(sketch, "E91.3.107", {"start": v(-11.34, -1.03) * mm, "end": v(-10.96, -0.93) * mm});
            skLineSegment(sketch, "E91.4.0", {"start": v(-8.9, -6.15) * mm, "end": v(-7.81, -5.07) * mm});
            skArc(sketch, "E91.4.1", {"start": v(-10.87, -7.85) * mm, "mid": v(-11.73, -6.77) * mm, "end": v(-12.23, -5.49) * mm});
            skLineSegment(sketch, "E91.4.2", {"start": v(-21.35, -7.73) * mm, "end": v(-19.8, -7.32) * mm});
            skLineSegment(sketch, "E91.4.3", {"start": v(-23.67, -8.35) * mm, "end": v(-22.12, -7.94) * mm});
            skArc(sketch, "E91.4.4", {"start": v(-16.24, -13.21) * mm, "mid": v(-18.3, -10.57) * mm, "end": v(-19.56, -7.46) * mm});
            skLineSegment(sketch, "E91.4.5", {"start": v(-9.78, -4.63) * mm, "end": v(-8.3, -4.23) * mm});
            skArc(sketch, "E91.4.6", {"start": v(-17.65, -14.63) * mm, "mid": v(-20.03, -11.57) * mm, "end": v(-21.5, -7.97) * mm});
            skArc(sketch, "E91.4.7", {"start": v(-11.16, -8.12) * mm, "mid": v(-12.07, -6.97) * mm, "end": v(-12.61, -5.6) * mm});
            skLineSegment(sketch, "E91.4.8", {"start": v(-26.18, -9.02) * mm, "end": v(-24.44, -8.56) * mm, "construction": true});
            skLineSegment(sketch, "E91.4.9", {"start": v(-12.28, -9.54) * mm, "end": v(-11.15, -8.4) * mm});
            skLineSegment(sketch, "E91.4.10", {"start": v(-13.98, -11.23) * mm, "end": v(-12.85, -10.1) * mm});
            skLineSegment(sketch, "E91.4.11", {"start": v(-16.72, -6.49) * mm, "end": v(-15.17, -6.08) * mm});
            skArc(sketch, "E91.4.12", {"start": v(-14.55, -11.51) * mm, "mid": v(-16.22, -9.37) * mm, "end": v(-17.24, -6.84) * mm});
            skLineSegment(sketch, "E91.4.13", {"start": v(-19.03, -7.1) * mm, "end": v(-17.5, -6.7) * mm});
            skArc(sketch, "E91.4.14", {"start": v(-15.96, -12.93) * mm, "mid": v(-17.95, -10.37) * mm, "end": v(-19.18, -7.35) * mm});
            skLineSegment(sketch, "E91.4.15", {"start": v(-14.4, -5.87) * mm, "end": v(-12.86, -5.46) * mm});
            skLineSegment(sketch, "E91.4.16", {"start": v(-15.67, -12.93) * mm, "end": v(-14.54, -11.8) * mm});
            skLineSegment(sketch, "E91.4.17", {"start": v(-17.37, -14.63) * mm, "end": v(-16.24, -13.5) * mm});
            skLineSegment(sketch, "E91.4.18", {"start": v(-19.07, -16.32) * mm, "end": v(-17.94, -15.2) * mm});
            skArc(sketch, "E91.4.19", {"start": v(-19.63, -16.6) * mm, "mid": v(-22.46, -12.97) * mm, "end": v(-24.2, -8.7) * mm});
            skLineSegment(sketch, "E91.4.20", {"start": v(-24.58, -14.2) * mm, "end": v(-7.74, -4.47) * mm, "construction": true});
            skArc(sketch, "E91.4.21", {"start": v(-12.56, -9.54) * mm, "mid": v(-13.8, -7.97) * mm, "end": v(-14.54, -6.1) * mm});
            skLineSegment(sketch, "E91.4.22", {"start": v(-10.59, -7.84) * mm, "end": v(-9.46, -6.72) * mm});
            skLineSegment(sketch, "E91.4.23", {"start": v(-20.9, -18.16) * mm, "end": v(-19.63, -16.89) * mm, "construction": true});
            skArc(sketch, "E91.4.24", {"start": v(-14.26, -11.24) * mm, "mid": v(-15.88, -9.17) * mm, "end": v(-16.86, -6.73) * mm});
            skArc(sketch, "E91.4.25", {"start": v(-19.35, -16.32) * mm, "mid": v(-22.1, -12.77) * mm, "end": v(-23.81, -8.6) * mm});
            skArc(sketch, "E91.4.26", {"start": v(-17.94, -14.9) * mm, "mid": v(-20.38, -11.77) * mm, "end": v(-21.88, -8.08) * mm});
            skArc(sketch, "E91.4.27", {"start": v(-12.85, -9.82) * mm, "mid": v(-14.15, -8.17) * mm, "end": v(-14.93, -6.22) * mm});
            skLineSegment(sketch, "E91.4.28", {"start": v(-12.09, -5.25) * mm, "end": v(-10.55, -4.84) * mm});
            skArc(sketch, "E91.4.29", {"start": v(-9.17, -6.17) * mm, "mid": v(-9.66, -5.58) * mm, "end": v(-9.93, -4.86) * mm});
            skPoint(sketch, "E91.4.30", {"position": v(-24.25, -8.5) * mm});
            skPoint(sketch, "E91.4.31", {"position": v(-14.12, -11.37) * mm});
            skPoint(sketch, "E91.4.32", {"position": v(-17.5, -14.76) * mm});
            skPoint(sketch, "E91.4.33", {"position": v(-10.72, -7.98) * mm});
            skPoint(sketch, "E91.4.34", {"position": v(-14.97, -6.02) * mm});
            skPoint(sketch, "E91.4.35", {"position": v(-9.95, -4.68) * mm});
            skPoint(sketch, "E91.4.36", {"position": v(-16.9, -6.54) * mm});
            skPoint(sketch, "E91.4.37", {"position": v(-9.3, -6.56) * mm});
            skPoint(sketch, "E91.4.38", {"position": v(-16.1, -13.35) * mm});
            skPoint(sketch, "E91.4.39", {"position": v(-19.22, -7.16) * mm});
            skPoint(sketch, "E91.4.40", {"position": v(-10.34, -4.78) * mm});
            skPoint(sketch, "E91.4.41", {"position": v(-14.4, -11.65) * mm});
            skArc(sketch, "E91.4.42", {"start": v(-9.47, -6.43) * mm, "mid": v(-10, -5.78) * mm, "end": v(-10.3, -4.99) * mm});
            skPoint(sketch, "E91.4.43", {"position": v(-19.6, -7.26) * mm});
            skLineSegment(sketch, "E91.4.44", {"start": v(-12.27, -5.3) * mm, "end": v(-10.34, -4.78) * mm});
            skPoint(sketch, "E91.4.45", {"position": v(-12.27, -5.3) * mm});
            skPoint(sketch, "E91.4.46", {"position": v(-12.7, -9.96) * mm});
            skPoint(sketch, "E91.4.47", {"position": v(-19.49, -16.74) * mm});
            skPoint(sketch, "E91.4.48", {"position": v(-21.54, -7.78) * mm});
            skLineSegment(sketch, "E91.4.49", {"start": v(-26.18, -9.02) * mm, "end": v(-8.3, -4.23) * mm});
            skPoint(sketch, "E91.4.50", {"position": v(-12.66, -5.4) * mm});
            skPoint(sketch, "E91.4.51", {"position": v(-19.2, -16.46) * mm});
            skPoint(sketch, "E91.4.52", {"position": v(-12.42, -9.67) * mm});
            skLineSegment(sketch, "E91.4.53", {"start": v(-20.9, -18.16) * mm, "end": v(-7.81, -5.07) * mm});
            skPoint(sketch, "E91.4.54", {"position": v(-21.93, -7.89) * mm});
            skPoint(sketch, "E91.4.55", {"position": v(-23.86, -8.4) * mm});
            skPoint(sketch, "E91.4.56", {"position": v(-17.8, -15.05) * mm});
            skPoint(sketch, "E91.4.57", {"position": v(-11, -8.26) * mm});
            skPoint(sketch, "E91.4.58", {"position": v(-14.59, -5.92) * mm});
            skPoint(sketch, "E91.4.59", {"position": v(-15.81, -13.07) * mm});
            skPoint(sketch, "E91.4.60", {"position": v(-17.3, -6.64) * mm});
            skPoint(sketch, "E91.4.61", {"position": v(-9.02, -6.28) * mm});
            skLineSegment(sketch, "E91.4.62", {"start": v(-26.18, -9.02) * mm, "end": v(-8.3, -4.23) * mm});
            skLineSegment(sketch, "E91.4.63", {"start": v(-10.72, -7.98) * mm, "end": v(-9.3, -6.56) * mm});
            skArc(sketch, "E91.4.64", {"start": v(-19.56, -7.46) * mm, "mid": v(-19.65, -7.34) * mm, "end": v(-19.8, -7.32) * mm});
            skArc(sketch, "E91.4.65", {"start": v(-14.54, -11.8) * mm, "mid": v(-14.49, -11.66) * mm, "end": v(-14.55, -11.51) * mm});
            skArc(sketch, "E91.4.66", {"start": v(-19.63, -16.89) * mm, "mid": v(-19.57, -16.75) * mm, "end": v(-19.63, -16.6) * mm});
            skArc(sketch, "E91.4.67", {"start": v(-14.26, -11.24) * mm, "mid": v(-14.12, -11.3) * mm, "end": v(-13.98, -11.23) * mm});
            skLineSegment(sketch, "E91.4.68", {"start": v(-24.25, -8.5) * mm, "end": v(-23.86, -8.4) * mm, "construction": true});
            skLineSegment(sketch, "E91.4.69", {"start": v(-12.7, -9.96) * mm, "end": v(-12.42, -9.67) * mm});
            skArc(sketch, "E91.4.70", {"start": v(-23.67, -8.35) * mm, "mid": v(-23.8, -8.44) * mm, "end": v(-23.81, -8.6) * mm});
            skArc(sketch, "E91.4.71", {"start": v(-24.2, -8.7) * mm, "mid": v(-24.29, -8.58) * mm, "end": v(-24.44, -8.56) * mm});
            skLineSegment(sketch, "E91.4.72", {"start": v(-14.4, -11.65) * mm, "end": v(-14.12, -11.37) * mm});
            skLineSegment(sketch, "E91.4.73", {"start": v(-17.3, -6.64) * mm, "end": v(-16.9, -6.54) * mm});
            skArc(sketch, "E91.4.74", {"start": v(-12.85, -10.1) * mm, "mid": v(-12.79, -9.96) * mm, "end": v(-12.85, -9.82) * mm});
            skArc(sketch, "E91.4.75", {"start": v(-17.94, -15.2) * mm, "mid": v(-17.88, -15.05) * mm, "end": v(-17.94, -14.9) * mm});
            skArc(sketch, "E91.4.76", {"start": v(-17.24, -6.84) * mm, "mid": v(-17.34, -6.72) * mm, "end": v(-17.5, -6.7) * mm});
            skArc(sketch, "E91.4.77", {"start": v(-12.56, -9.54) * mm, "mid": v(-12.42, -9.6) * mm, "end": v(-12.28, -9.54) * mm});
            skArc(sketch, "E91.4.78", {"start": v(-16.24, -13.5) * mm, "mid": v(-16.18, -13.35) * mm, "end": v(-16.24, -13.21) * mm});
            skArc(sketch, "E91.4.79", {"start": v(-16.72, -6.49) * mm, "mid": v(-16.84, -6.58) * mm, "end": v(-16.86, -6.73) * mm});
            skArc(sketch, "E91.4.80", {"start": v(-11.15, -8.4) * mm, "mid": v(-11.1, -8.26) * mm, "end": v(-11.16, -8.12) * mm});
            skLineSegment(sketch, "E91.4.81", {"start": v(-10.34, -4.78) * mm, "end": v(-9.95, -4.68) * mm});
            skArc(sketch, "E91.4.82", {"start": v(-21.88, -8.08) * mm, "mid": v(-21.97, -7.96) * mm, "end": v(-22.12, -7.94) * mm});
            skArc(sketch, "E91.4.83", {"start": v(-12.09, -5.25) * mm, "mid": v(-12.2, -5.34) * mm, "end": v(-12.23, -5.49) * mm});
            skLineSegment(sketch, "E91.4.84", {"start": v(-19.6, -7.26) * mm, "end": v(-19.22, -7.16) * mm});
            skArc(sketch, "E91.4.85", {"start": v(-19.03, -7.1) * mm, "mid": v(-19.16, -7.2) * mm, "end": v(-19.18, -7.35) * mm});
            skArc(sketch, "E91.4.86", {"start": v(-12.61, -5.6) * mm, "mid": v(-12.7, -5.48) * mm, "end": v(-12.86, -5.46) * mm});
            skArc(sketch, "E91.4.87", {"start": v(-21.35, -7.73) * mm, "mid": v(-21.47, -7.82) * mm, "end": v(-21.5, -7.97) * mm});
            skArc(sketch, "E91.4.88", {"start": v(-15.96, -12.93) * mm, "mid": v(-15.81, -12.99) * mm, "end": v(-15.67, -12.93) * mm});
            skArc(sketch, "E91.4.89", {"start": v(-10.3, -4.99) * mm, "mid": v(-10.4, -4.86) * mm, "end": v(-10.55, -4.84) * mm});
            skLineSegment(sketch, "E91.4.90", {"start": v(-21.93, -7.89) * mm, "end": v(-21.54, -7.78) * mm});
            skLineSegment(sketch, "E91.4.91", {"start": v(-16.1, -13.35) * mm, "end": v(-15.81, -13.07) * mm});
            skArc(sketch, "E91.4.92", {"start": v(-14.4, -5.87) * mm, "mid": v(-14.52, -5.96) * mm, "end": v(-14.54, -6.1) * mm});
            skArc(sketch, "E91.4.93", {"start": v(-10.87, -7.85) * mm, "mid": v(-10.73, -7.9) * mm, "end": v(-10.59, -7.84) * mm});
            skArc(sketch, "E91.4.94", {"start": v(-19.35, -16.32) * mm, "mid": v(-19.2, -16.38) * mm, "end": v(-19.07, -16.32) * mm});
            skLineSegment(sketch, "E91.4.95", {"start": v(-17.8, -15.05) * mm, "end": v(-17.5, -14.76) * mm});
            skLineSegment(sketch, "E91.4.96", {"start": v(-19.49, -16.74) * mm, "end": v(-19.2, -16.46) * mm, "construction": true});
            skArc(sketch, "E91.4.97", {"start": v(-14.93, -6.22) * mm, "mid": v(-15.02, -6.1) * mm, "end": v(-15.17, -6.08) * mm});
            skLineSegment(sketch, "E91.4.98", {"start": v(-12.66, -5.4) * mm, "end": v(-12.27, -5.3) * mm});
            skLineSegment(sketch, "E91.4.99", {"start": v(-11, -8.26) * mm, "end": v(-10.72, -7.98) * mm});
            skLineSegment(sketch, "E91.4.100", {"start": v(-14.97, -6.02) * mm, "end": v(-14.59, -5.92) * mm});
            skArc(sketch, "E91.4.101", {"start": v(-17.65, -14.63) * mm, "mid": v(-17.51, -14.68) * mm, "end": v(-17.37, -14.63) * mm});
            skArc(sketch, "E91.4.102", {"start": v(-9.78, -4.63) * mm, "mid": v(-9.9, -4.72) * mm, "end": v(-9.93, -4.86) * mm});
            skLineSegment(sketch, "E91.4.103", {"start": v(-9.3, -6.56) * mm, "end": v(-9.02, -6.28) * mm});
            skArc(sketch, "E91.4.104", {"start": v(-9.46, -6.72) * mm, "mid": v(-9.4, -6.57) * mm, "end": v(-9.47, -6.43) * mm});
            skArc(sketch, "E91.4.105", {"start": v(-9.17, -6.17) * mm, "mid": v(-9.03, -6.21) * mm, "end": v(-8.9, -6.15) * mm});
            skLineSegment(sketch, "E91.4.106", {"start": v(-10.34, -4.78) * mm, "end": v(-9.95, -4.68) * mm});
            skLineSegment(sketch, "E91.4.107", {"start": v(-9.3, -6.56) * mm, "end": v(-9.02, -6.28) * mm});
            skLineSegment(sketch, "E91.5.0", {"start": v(-4.63, -9.78) * mm, "end": v(-4.23, -8.3) * mm});
            skArc(sketch, "E91.5.1", {"start": v(-5.49, -12.23) * mm, "mid": v(-6.77, -11.73) * mm, "end": v(-7.85, -10.87) * mm});
            skLineSegment(sketch, "E91.5.2", {"start": v(-14.63, -17.37) * mm, "end": v(-13.5, -16.24) * mm});
            skLineSegment(sketch, "E91.5.3", {"start": v(-16.32, -19.07) * mm, "end": v(-15.2, -17.94) * mm});
            skArc(sketch, "E91.5.4", {"start": v(-7.46, -19.56) * mm, "mid": v(-10.57, -18.3) * mm, "end": v(-13.21, -16.24) * mm});
            skLineSegment(sketch, "E91.5.5", {"start": v(-6.15, -8.9) * mm, "end": v(-5.07, -7.81) * mm});
            skArc(sketch, "E91.5.6", {"start": v(-7.97, -21.5) * mm, "mid": v(-11.57, -20.03) * mm, "end": v(-14.63, -17.65) * mm});
            skArc(sketch, "E91.5.7", {"start": v(-5.6, -12.61) * mm, "mid": v(-6.97, -12.07) * mm, "end": v(-8.12, -11.16) * mm});
            skLineSegment(sketch, "E91.5.8", {"start": v(-18.16, -20.9) * mm, "end": v(-16.89, -19.63) * mm, "construction": true});
            skLineSegment(sketch, "E91.5.9", {"start": v(-5.87, -14.4) * mm, "end": v(-5.46, -12.86) * mm});
            skLineSegment(sketch, "E91.5.10", {"start": v(-6.49, -16.72) * mm, "end": v(-6.08, -15.17) * mm});
            skLineSegment(sketch, "E91.5.11", {"start": v(-11.23, -13.98) * mm, "end": v(-10.1, -12.85) * mm});
            skArc(sketch, "E91.5.12", {"start": v(-6.84, -17.24) * mm, "mid": v(-9.37, -16.22) * mm, "end": v(-11.51, -14.55) * mm});
            skLineSegment(sketch, "E91.5.13", {"start": v(-12.93, -15.67) * mm, "end": v(-11.8, -14.54) * mm});
            skArc(sketch, "E91.5.14", {"start": v(-7.35, -19.18) * mm, "mid": v(-10.37, -17.95) * mm, "end": v(-12.93, -15.96) * mm});
            skLineSegment(sketch, "E91.5.15", {"start": v(-9.54, -12.28) * mm, "end": v(-8.4, -11.15) * mm});
            skLineSegment(sketch, "E91.5.16", {"start": v(-7.1, -19.03) * mm, "end": v(-6.7, -17.5) * mm});
            skLineSegment(sketch, "E91.5.17", {"start": v(-7.73, -21.35) * mm, "end": v(-7.32, -19.8) * mm});
            skLineSegment(sketch, "E91.5.18", {"start": v(-8.35, -23.67) * mm, "end": v(-7.94, -22.12) * mm});
            skArc(sketch, "E91.5.19", {"start": v(-8.7, -24.2) * mm, "mid": v(-12.97, -22.46) * mm, "end": v(-16.6, -19.63) * mm});
            skLineSegment(sketch, "E91.5.20", {"start": v(-14.2, -24.58) * mm, "end": v(-4.47, -7.74) * mm, "construction": true});
            skArc(sketch, "E91.5.21", {"start": v(-6.1, -14.54) * mm, "mid": v(-7.97, -13.8) * mm, "end": v(-9.54, -12.56) * mm});
            skLineSegment(sketch, "E91.5.22", {"start": v(-5.25, -12.09) * mm, "end": v(-4.84, -10.55) * mm});
            skLineSegment(sketch, "E91.5.23", {"start": v(-9.02, -26.18) * mm, "end": v(-8.56, -24.44) * mm, "construction": true});
            skArc(sketch, "E91.5.24", {"start": v(-6.73, -16.86) * mm, "mid": v(-9.17, -15.88) * mm, "end": v(-11.24, -14.26) * mm});
            skArc(sketch, "E91.5.25", {"start": v(-8.6, -23.81) * mm, "mid": v(-12.77, -22.1) * mm, "end": v(-16.32, -19.35) * mm});
            skArc(sketch, "E91.5.26", {"start": v(-8.08, -21.88) * mm, "mid": v(-11.77, -20.38) * mm, "end": v(-14.9, -17.94) * mm});
            skArc(sketch, "E91.5.27", {"start": v(-6.22, -14.93) * mm, "mid": v(-8.17, -14.15) * mm, "end": v(-9.82, -12.85) * mm});
            skLineSegment(sketch, "E91.5.28", {"start": v(-7.84, -10.59) * mm, "end": v(-6.72, -9.46) * mm});
            skArc(sketch, "E91.5.29", {"start": v(-4.86, -9.93) * mm, "mid": v(-5.58, -9.66) * mm, "end": v(-6.17, -9.17) * mm});
            skPoint(sketch, "E91.5.30", {"position": v(-16.74, -19.49) * mm});
            skPoint(sketch, "E91.5.31", {"position": v(-6.54, -16.9) * mm});
            skPoint(sketch, "E91.5.32", {"position": v(-7.78, -21.54) * mm});
            skPoint(sketch, "E91.5.33", {"position": v(-5.3, -12.27) * mm});
            skPoint(sketch, "E91.5.34", {"position": v(-9.96, -12.7) * mm});
            skPoint(sketch, "E91.5.35", {"position": v(-6.28, -9.02) * mm});
            skPoint(sketch, "E91.5.36", {"position": v(-11.37, -14.12) * mm});
            skPoint(sketch, "E91.5.37", {"position": v(-4.78, -10.34) * mm});
            skPoint(sketch, "E91.5.38", {"position": v(-7.26, -19.6) * mm});
            skPoint(sketch, "E91.5.39", {"position": v(-13.07, -15.81) * mm});
            skPoint(sketch, "E91.5.40", {"position": v(-6.56, -9.3) * mm});
            skPoint(sketch, "E91.5.41", {"position": v(-6.64, -17.3) * mm});
            skArc(sketch, "E91.5.42", {"start": v(-4.99, -10.3) * mm, "mid": v(-5.78, -10) * mm, "end": v(-6.43, -9.47) * mm});
            skPoint(sketch, "E91.5.43", {"position": v(-13.35, -16.1) * mm});
            skLineSegment(sketch, "E91.5.44", {"start": v(-7.98, -10.72) * mm, "end": v(-6.56, -9.3) * mm});
            skPoint(sketch, "E91.5.45", {"position": v(-7.98, -10.72) * mm});
            skPoint(sketch, "E91.5.46", {"position": v(-6.02, -14.97) * mm});
            skPoint(sketch, "E91.5.47", {"position": v(-8.5, -24.25) * mm});
            skPoint(sketch, "E91.5.48", {"position": v(-14.76, -17.5) * mm});
            skLineSegment(sketch, "E91.5.49", {"start": v(-18.16, -20.9) * mm, "end": v(-5.07, -7.81) * mm});
            skPoint(sketch, "E91.5.50", {"position": v(-8.26, -11) * mm});
            skPoint(sketch, "E91.5.51", {"position": v(-8.4, -23.86) * mm});
            skPoint(sketch, "E91.5.52", {"position": v(-5.92, -14.59) * mm});
            skLineSegment(sketch, "E91.5.53", {"start": v(-9.02, -26.18) * mm, "end": v(-4.23, -8.3) * mm});
            skPoint(sketch, "E91.5.54", {"position": v(-15.05, -17.8) * mm});
            skPoint(sketch, "E91.5.55", {"position": v(-16.46, -19.2) * mm});
            skPoint(sketch, "E91.5.56", {"position": v(-7.89, -21.93) * mm});
            skPoint(sketch, "E91.5.57", {"position": v(-5.4, -12.66) * mm});
            skPoint(sketch, "E91.5.58", {"position": v(-9.67, -12.42) * mm});
            skPoint(sketch, "E91.5.59", {"position": v(-7.16, -19.22) * mm});
            skPoint(sketch, "E91.5.60", {"position": v(-11.65, -14.4) * mm});
            skPoint(sketch, "E91.5.61", {"position": v(-4.68, -9.95) * mm});
            skLineSegment(sketch, "E91.5.62", {"start": v(-18.16, -20.9) * mm, "end": v(-5.07, -7.81) * mm});
            skLineSegment(sketch, "E91.5.63", {"start": v(-5.3, -12.27) * mm, "end": v(-4.78, -10.34) * mm});
            skArc(sketch, "E91.5.64", {"start": v(-13.21, -16.24) * mm, "mid": v(-13.35, -16.18) * mm, "end": v(-13.5, -16.24) * mm});
            skArc(sketch, "E91.5.65", {"start": v(-6.7, -17.5) * mm, "mid": v(-6.72, -17.34) * mm, "end": v(-6.84, -17.24) * mm});
            skArc(sketch, "E91.5.66", {"start": v(-8.56, -24.44) * mm, "mid": v(-8.58, -24.29) * mm, "end": v(-8.7, -24.2) * mm});
            skArc(sketch, "E91.5.67", {"start": v(-6.73, -16.86) * mm, "mid": v(-6.58, -16.84) * mm, "end": v(-6.49, -16.72) * mm});
            skLineSegment(sketch, "E91.5.68", {"start": v(-16.74, -19.49) * mm, "end": v(-16.46, -19.2) * mm, "construction": true});
            skLineSegment(sketch, "E91.5.69", {"start": v(-6.02, -14.97) * mm, "end": v(-5.92, -14.59) * mm});
            skArc(sketch, "E91.5.70", {"start": v(-16.32, -19.07) * mm, "mid": v(-16.38, -19.2) * mm, "end": v(-16.32, -19.35) * mm});
            skArc(sketch, "E91.5.71", {"start": v(-16.6, -19.63) * mm, "mid": v(-16.75, -19.57) * mm, "end": v(-16.89, -19.63) * mm});
            skLineSegment(sketch, "E91.5.72", {"start": v(-6.64, -17.3) * mm, "end": v(-6.54, -16.9) * mm});
            skLineSegment(sketch, "E91.5.73", {"start": v(-11.65, -14.4) * mm, "end": v(-11.37, -14.12) * mm});
            skArc(sketch, "E91.5.74", {"start": v(-6.08, -15.17) * mm, "mid": v(-6.1, -15.02) * mm, "end": v(-6.22, -14.93) * mm});
            skArc(sketch, "E91.5.75", {"start": v(-7.94, -22.12) * mm, "mid": v(-7.96, -21.97) * mm, "end": v(-8.08, -21.88) * mm});
            skArc(sketch, "E91.5.76", {"start": v(-11.51, -14.55) * mm, "mid": v(-11.66, -14.49) * mm, "end": v(-11.8, -14.54) * mm});
            skArc(sketch, "E91.5.77", {"start": v(-6.1, -14.54) * mm, "mid": v(-5.96, -14.52) * mm, "end": v(-5.87, -14.4) * mm});
            skArc(sketch, "E91.5.78", {"start": v(-7.32, -19.8) * mm, "mid": v(-7.34, -19.65) * mm, "end": v(-7.46, -19.56) * mm});
            skArc(sketch, "E91.5.79", {"start": v(-11.23, -13.98) * mm, "mid": v(-11.3, -14.12) * mm, "end": v(-11.24, -14.26) * mm});
            skArc(sketch, "E91.5.80", {"start": v(-5.46, -12.86) * mm, "mid": v(-5.48, -12.7) * mm, "end": v(-5.6, -12.61) * mm});
            skLineSegment(sketch, "E91.5.81", {"start": v(-6.56, -9.3) * mm, "end": v(-6.28, -9.02) * mm});
            skArc(sketch, "E91.5.82", {"start": v(-14.9, -17.94) * mm, "mid": v(-15.05, -17.88) * mm, "end": v(-15.2, -17.94) * mm});
            skArc(sketch, "E91.5.83", {"start": v(-7.84, -10.59) * mm, "mid": v(-7.9, -10.73) * mm, "end": v(-7.85, -10.87) * mm});
            skLineSegment(sketch, "E91.5.84", {"start": v(-13.35, -16.1) * mm, "end": v(-13.07, -15.81) * mm});
            skArc(sketch, "E91.5.85", {"start": v(-12.93, -15.67) * mm, "mid": v(-12.99, -15.81) * mm, "end": v(-12.93, -15.96) * mm});
            skArc(sketch, "E91.5.86", {"start": v(-8.12, -11.16) * mm, "mid": v(-8.26, -11.1) * mm, "end": v(-8.4, -11.15) * mm});
            skArc(sketch, "E91.5.87", {"start": v(-14.63, -17.37) * mm, "mid": v(-14.68, -17.51) * mm, "end": v(-14.63, -17.65) * mm});
            skArc(sketch, "E91.5.88", {"start": v(-7.35, -19.18) * mm, "mid": v(-7.2, -19.16) * mm, "end": v(-7.1, -19.03) * mm});
            skArc(sketch, "E91.5.89", {"start": v(-6.43, -9.47) * mm, "mid": v(-6.57, -9.4) * mm, "end": v(-6.72, -9.46) * mm});
            skLineSegment(sketch, "E91.5.90", {"start": v(-15.05, -17.8) * mm, "end": v(-14.76, -17.5) * mm});
            skLineSegment(sketch, "E91.5.91", {"start": v(-7.26, -19.6) * mm, "end": v(-7.16, -19.22) * mm});
            skArc(sketch, "E91.5.92", {"start": v(-9.54, -12.28) * mm, "mid": v(-9.6, -12.42) * mm, "end": v(-9.54, -12.56) * mm});
            skArc(sketch, "E91.5.93", {"start": v(-5.49, -12.23) * mm, "mid": v(-5.34, -12.2) * mm, "end": v(-5.25, -12.09) * mm});
            skArc(sketch, "E91.5.94", {"start": v(-8.6, -23.81) * mm, "mid": v(-8.44, -23.8) * mm, "end": v(-8.35, -23.67) * mm});
            skLineSegment(sketch, "E91.5.95", {"start": v(-7.89, -21.93) * mm, "end": v(-7.78, -21.54) * mm});
            skLineSegment(sketch, "E91.5.96", {"start": v(-8.5, -24.25) * mm, "end": v(-8.4, -23.86) * mm, "construction": true});
            skArc(sketch, "E91.5.97", {"start": v(-9.82, -12.85) * mm, "mid": v(-9.96, -12.79) * mm, "end": v(-10.1, -12.85) * mm});
            skLineSegment(sketch, "E91.5.98", {"start": v(-8.26, -11) * mm, "end": v(-7.98, -10.72) * mm});
            skLineSegment(sketch, "E91.5.99", {"start": v(-5.4, -12.66) * mm, "end": v(-5.3, -12.27) * mm});
            skLineSegment(sketch, "E91.5.100", {"start": v(-9.96, -12.7) * mm, "end": v(-9.67, -12.42) * mm});
            skArc(sketch, "E91.5.101", {"start": v(-7.97, -21.5) * mm, "mid": v(-7.82, -21.47) * mm, "end": v(-7.73, -21.35) * mm});
            skArc(sketch, "E91.5.102", {"start": v(-6.15, -8.9) * mm, "mid": v(-6.21, -9.03) * mm, "end": v(-6.17, -9.17) * mm});
            skLineSegment(sketch, "E91.5.103", {"start": v(-4.78, -10.34) * mm, "end": v(-4.68, -9.95) * mm});
            skArc(sketch, "E91.5.104", {"start": v(-4.84, -10.55) * mm, "mid": v(-4.86, -10.4) * mm, "end": v(-4.99, -10.3) * mm});
            skArc(sketch, "E91.5.105", {"start": v(-4.86, -9.93) * mm, "mid": v(-4.72, -9.9) * mm, "end": v(-4.63, -9.78) * mm});
            skLineSegment(sketch, "E91.5.106", {"start": v(-6.56, -9.3) * mm, "end": v(-6.28, -9.02) * mm});
            skLineSegment(sketch, "E91.5.107", {"start": v(-4.78, -10.34) * mm, "end": v(-4.68, -9.95) * mm});
            skLineSegment(sketch, "E91.6.0", {"start": v(0.88, -10.79) * mm, "end": v(0.48, -9.3) * mm});
            skArc(sketch, "E91.6.1", {"start": v(1.36, -13.33) * mm, "mid": v(0, -13.54) * mm, "end": v(-1.36, -13.33) * mm});
            skLineSegment(sketch, "E91.6.2", {"start": v(-3.98, -22.36) * mm, "end": v(-3.57, -20.81) * mm});
            skLineSegment(sketch, "E91.6.3", {"start": v(-4.6, -24.67) * mm, "end": v(-4.19, -23.13) * mm});
            skArc(sketch, "E91.6.4", {"start": v(3.32, -20.67) * mm, "mid": v(0, -21.13) * mm, "end": v(-3.32, -20.67) * mm});
            skLineSegment(sketch, "E91.6.5", {"start": v(-0.88, -10.79) * mm, "end": v(-0.48, -9.3) * mm});
            skArc(sketch, "E91.6.6", {"start": v(3.84, -22.6) * mm, "mid": v(0, -23.13) * mm, "end": v(-3.84, -22.6) * mm});
            skArc(sketch, "E91.6.7", {"start": v(1.45, -13.72) * mm, "mid": v(0, -13.94) * mm, "end": v(-1.45, -13.72) * mm});
            skLineSegment(sketch, "E91.6.8", {"start": v(-5.27, -27.18) * mm, "end": v(-4.8, -25.45) * mm, "construction": true});
            skLineSegment(sketch, "E91.6.9", {"start": v(2.12, -15.4) * mm, "end": v(1.7, -13.86) * mm});
            skLineSegment(sketch, "E91.6.10", {"start": v(2.74, -17.72) * mm, "end": v(2.33, -16.18) * mm});
            skLineSegment(sketch, "E91.6.11", {"start": v(-2.74, -17.72) * mm, "end": v(-2.33, -16.18) * mm});
            skArc(sketch, "E91.6.12", {"start": v(2.7, -18.35) * mm, "mid": v(0, -18.73) * mm, "end": v(-2.7, -18.35) * mm});
            skLineSegment(sketch, "E91.6.13", {"start": v(-3.36, -20.04) * mm, "end": v(-2.95, -18.5) * mm});
            skArc(sketch, "E91.6.14", {"start": v(3.22, -20.28) * mm, "mid": v(0, -20.73) * mm, "end": v(-3.22, -20.28) * mm});
            skLineSegment(sketch, "E91.6.15", {"start": v(-2.12, -15.4) * mm, "end": v(-1.7, -13.86) * mm});
            skLineSegment(sketch, "E91.6.16", {"start": v(3.36, -20.04) * mm, "end": v(2.95, -18.5) * mm});
            skLineSegment(sketch, "E91.6.17", {"start": v(3.98, -22.36) * mm, "end": v(3.57, -20.81) * mm});
            skLineSegment(sketch, "E91.6.18", {"start": v(4.6, -24.67) * mm, "end": v(4.19, -23.13) * mm});
            skArc(sketch, "E91.6.19", {"start": v(4.56, -25.3) * mm, "mid": v(0, -25.93) * mm, "end": v(-4.56, -25.3) * mm});
            skLineSegment(sketch, "E91.6.20", {"start": v(0, -28.38) * mm, "end": v(0, -8.93) * mm, "construction": true});
            skArc(sketch, "E91.6.21", {"start": v(1.98, -15.65) * mm, "mid": v(0, -15.94) * mm, "end": v(-1.98, -15.65) * mm});
            skLineSegment(sketch, "E91.6.22", {"start": v(1.5, -13.1) * mm, "end": v(1.09, -11.56) * mm});
            skLineSegment(sketch, "E91.6.23", {"start": v(5.27, -27.18) * mm, "end": v(4.8, -25.45) * mm, "construction": true});
            skArc(sketch, "E91.6.24", {"start": v(2.6, -17.97) * mm, "mid": v(0, -18.33) * mm, "end": v(-2.6, -17.97) * mm});
            skArc(sketch, "E91.6.25", {"start": v(4.46, -24.92) * mm, "mid": v(0, -25.53) * mm, "end": v(-4.46, -24.92) * mm});
            skArc(sketch, "E91.6.26", {"start": v(3.94, -22.99) * mm, "mid": v(0, -23.53) * mm, "end": v(-3.94, -22.99) * mm});
            skArc(sketch, "E91.6.27", {"start": v(2.08, -16.04) * mm, "mid": v(0, -16.34) * mm, "end": v(-2.08, -16.04) * mm});
            skLineSegment(sketch, "E91.6.28", {"start": v(-1.5, -13.1) * mm, "end": v(-1.09, -11.56) * mm});
            skArc(sketch, "E91.6.29", {"start": v(0.75, -11.03) * mm, "mid": v(0, -11.16) * mm, "end": v(-0.75, -11.03) * mm});
            skPoint(sketch, "E91.6.30", {"position": v(-4.76, -25.25) * mm});
            skPoint(sketch, "E91.6.31", {"position": v(2.79, -17.9) * mm});
            skPoint(sketch, "E91.6.32", {"position": v(4.03, -22.55) * mm});
            skPoint(sketch, "E91.6.33", {"position": v(1.55, -13.27) * mm});
            skPoint(sketch, "E91.6.34", {"position": v(-2.27, -15.98) * mm});
            skPoint(sketch, "E91.6.35", {"position": v(-0.93, -10.96) * mm});
            skPoint(sketch, "E91.6.36", {"position": v(-2.79, -17.9) * mm});
            skPoint(sketch, "E91.6.37", {"position": v(1.03, -11.34) * mm});
            skPoint(sketch, "E91.6.38", {"position": v(3.51, -20.61) * mm});
            skPoint(sketch, "E91.6.39", {"position": v(-3.41, -20.23) * mm});
            skPoint(sketch, "E91.6.40", {"position": v(-1.03, -11.34) * mm});
            skPoint(sketch, "E91.6.41", {"position": v(2.9, -18.3) * mm});
            skArc(sketch, "E91.6.42", {"start": v(0.83, -11.42) * mm, "mid": v(0, -11.55) * mm, "end": v(-0.83, -11.42) * mm});
            skPoint(sketch, "E91.6.43", {"position": v(-3.51, -20.61) * mm});
            skLineSegment(sketch, "E91.6.44", {"start": v(-1.55, -13.27) * mm, "end": v(-1.03, -11.34) * mm});
            skPoint(sketch, "E91.6.45", {"position": v(-1.55, -13.27) * mm});
            skPoint(sketch, "E91.6.46", {"position": v(2.27, -15.98) * mm});
            skPoint(sketch, "E91.6.47", {"position": v(4.76, -25.25) * mm});
            skPoint(sketch, "E91.6.48", {"position": v(-4.03, -22.55) * mm});
            skLineSegment(sketch, "E91.6.49", {"start": v(-5.27, -27.18) * mm, "end": v(-0.48, -9.3) * mm});
            skPoint(sketch, "E91.6.50", {"position": v(-1.65, -13.66) * mm});
            skPoint(sketch, "E91.6.51", {"position": v(4.65, -24.86) * mm});
            skPoint(sketch, "E91.6.52", {"position": v(2.17, -15.6) * mm});
            skLineSegment(sketch, "E91.6.53", {"start": v(5.27, -27.18) * mm, "end": v(0.48, -9.3) * mm});
            skPoint(sketch, "E91.6.54", {"position": v(-4.14, -22.93) * mm});
            skPoint(sketch, "E91.6.55", {"position": v(-4.65, -24.86) * mm});
            skPoint(sketch, "E91.6.56", {"position": v(4.14, -22.93) * mm});
            skPoint(sketch, "E91.6.57", {"position": v(1.65, -13.66) * mm});
            skPoint(sketch, "E91.6.58", {"position": v(-2.17, -15.6) * mm});
            skPoint(sketch, "E91.6.59", {"position": v(3.41, -20.23) * mm});
            skPoint(sketch, "E91.6.60", {"position": v(-2.9, -18.3) * mm});
            skPoint(sketch, "E91.6.61", {"position": v(0.93, -10.96) * mm});
            skLineSegment(sketch, "E91.6.62", {"start": v(-5.27, -27.18) * mm, "end": v(-0.48, -9.3) * mm});
            skLineSegment(sketch, "E91.6.63", {"start": v(1.55, -13.27) * mm, "end": v(1.03, -11.34) * mm});
            skArc(sketch, "E91.6.64", {"start": v(-3.32, -20.67) * mm, "mid": v(-3.47, -20.69) * mm, "end": v(-3.57, -20.81) * mm});
            skArc(sketch, "E91.6.65", {"start": v(2.95, -18.5) * mm, "mid": v(2.85, -18.37) * mm, "end": v(2.7, -18.35) * mm});
            skArc(sketch, "E91.6.66", {"start": v(4.8, -25.45) * mm, "mid": v(4.71, -25.33) * mm, "end": v(4.56, -25.3) * mm});
            skArc(sketch, "E91.6.67", {"start": v(2.6, -17.97) * mm, "mid": v(2.72, -17.87) * mm, "end": v(2.74, -17.72) * mm});
            skLineSegment(sketch, "E91.6.68", {"start": v(-4.76, -25.25) * mm, "end": v(-4.65, -24.86) * mm, "construction": true});
            skLineSegment(sketch, "E91.6.69", {"start": v(2.27, -15.98) * mm, "end": v(2.17, -15.6) * mm});
            skArc(sketch, "E91.6.70", {"start": v(-4.6, -24.67) * mm, "mid": v(-4.58, -24.83) * mm, "end": v(-4.46, -24.92) * mm});
            skArc(sketch, "E91.6.71", {"start": v(-4.56, -25.3) * mm, "mid": v(-4.71, -25.33) * mm, "end": v(-4.8, -25.45) * mm});
            skLineSegment(sketch, "E91.6.72", {"start": v(2.9, -18.3) * mm, "end": v(2.79, -17.9) * mm});
            skLineSegment(sketch, "E91.6.73", {"start": v(-2.9, -18.3) * mm, "end": v(-2.79, -17.9) * mm});
            skArc(sketch, "E91.6.74", {"start": v(2.33, -16.18) * mm, "mid": v(2.23, -16.06) * mm, "end": v(2.08, -16.04) * mm});
            skArc(sketch, "E91.6.75", {"start": v(4.19, -23.13) * mm, "mid": v(4.1, -23) * mm, "end": v(3.94, -22.99) * mm});
            skArc(sketch, "E91.6.76", {"start": v(-2.7, -18.35) * mm, "mid": v(-2.85, -18.37) * mm, "end": v(-2.95, -18.5) * mm});
            skArc(sketch, "E91.6.77", {"start": v(1.98, -15.65) * mm, "mid": v(2.1, -15.56) * mm, "end": v(2.12, -15.4) * mm});
            skArc(sketch, "E91.6.78", {"start": v(3.57, -20.81) * mm, "mid": v(3.47, -20.69) * mm, "end": v(3.32, -20.67) * mm});
            skArc(sketch, "E91.6.79", {"start": v(-2.74, -17.72) * mm, "mid": v(-2.72, -17.87) * mm, "end": v(-2.6, -17.97) * mm});
            skArc(sketch, "E91.6.80", {"start": v(1.7, -13.86) * mm, "mid": v(1.6, -13.74) * mm, "end": v(1.45, -13.72) * mm});
            skLineSegment(sketch, "E91.6.81", {"start": v(-1.03, -11.34) * mm, "end": v(-0.93, -10.96) * mm});
            skArc(sketch, "E91.6.82", {"start": v(-3.94, -22.99) * mm, "mid": v(-4.1, -23) * mm, "end": v(-4.19, -23.13) * mm});
            skArc(sketch, "E91.6.83", {"start": v(-1.5, -13.1) * mm, "mid": v(-1.48, -13.24) * mm, "end": v(-1.36, -13.33) * mm});
            skLineSegment(sketch, "E91.6.84", {"start": v(-3.51, -20.61) * mm, "end": v(-3.41, -20.23) * mm});
            skArc(sketch, "E91.6.85", {"start": v(-3.36, -20.04) * mm, "mid": v(-3.34, -20.19) * mm, "end": v(-3.22, -20.28) * mm});
            skArc(sketch, "E91.6.86", {"start": v(-1.45, -13.72) * mm, "mid": v(-1.6, -13.74) * mm, "end": v(-1.7, -13.86) * mm});
            skArc(sketch, "E91.6.87", {"start": v(-3.98, -22.36) * mm, "mid": v(-3.96, -22.5) * mm, "end": v(-3.84, -22.6) * mm});
            skArc(sketch, "E91.6.88", {"start": v(3.22, -20.28) * mm, "mid": v(3.34, -20.19) * mm, "end": v(3.36, -20.04) * mm});
            skArc(sketch, "E91.6.89", {"start": v(-0.83, -11.42) * mm, "mid": v(-0.99, -11.43) * mm, "end": v(-1.09, -11.56) * mm});
            skLineSegment(sketch, "E91.6.90", {"start": v(-4.14, -22.93) * mm, "end": v(-4.03, -22.55) * mm});
            skLineSegment(sketch, "E91.6.91", {"start": v(3.51, -20.61) * mm, "end": v(3.41, -20.23) * mm});
            skArc(sketch, "E91.6.92", {"start": v(-2.12, -15.4) * mm, "mid": v(-2.1, -15.56) * mm, "end": v(-1.98, -15.65) * mm});
            skArc(sketch, "E91.6.93", {"start": v(1.36, -13.33) * mm, "mid": v(1.48, -13.24) * mm, "end": v(1.5, -13.1) * mm});
            skArc(sketch, "E91.6.94", {"start": v(4.46, -24.92) * mm, "mid": v(4.58, -24.83) * mm, "end": v(4.6, -24.67) * mm});
            skLineSegment(sketch, "E91.6.95", {"start": v(4.14, -22.93) * mm, "end": v(4.03, -22.55) * mm});
            skLineSegment(sketch, "E91.6.96", {"start": v(4.76, -25.25) * mm, "end": v(4.65, -24.86) * mm, "construction": true});
            skArc(sketch, "E91.6.97", {"start": v(-2.08, -16.04) * mm, "mid": v(-2.23, -16.06) * mm, "end": v(-2.33, -16.18) * mm});
            skLineSegment(sketch, "E91.6.98", {"start": v(-1.65, -13.66) * mm, "end": v(-1.55, -13.27) * mm});
            skLineSegment(sketch, "E91.6.99", {"start": v(1.65, -13.66) * mm, "end": v(1.55, -13.27) * mm});
            skLineSegment(sketch, "E91.6.100", {"start": v(-2.27, -15.98) * mm, "end": v(-2.17, -15.6) * mm});
            skArc(sketch, "E91.6.101", {"start": v(3.84, -22.6) * mm, "mid": v(3.96, -22.5) * mm, "end": v(3.98, -22.36) * mm});
            skArc(sketch, "E91.6.102", {"start": v(-0.88, -10.79) * mm, "mid": v(-0.86, -10.93) * mm, "end": v(-0.75, -11.03) * mm});
            skLineSegment(sketch, "E91.6.103", {"start": v(1.03, -11.34) * mm, "end": v(0.93, -10.96) * mm});
            skArc(sketch, "E91.6.104", {"start": v(1.09, -11.56) * mm, "mid": v(0.99, -11.43) * mm, "end": v(0.83, -11.42) * mm});
            skArc(sketch, "E91.6.105", {"start": v(0.75, -11.03) * mm, "mid": v(0.86, -10.93) * mm, "end": v(0.88, -10.79) * mm});
            skLineSegment(sketch, "E91.6.106", {"start": v(-1.03, -11.34) * mm, "end": v(-0.93, -10.96) * mm});
            skLineSegment(sketch, "E91.6.107", {"start": v(1.03, -11.34) * mm, "end": v(0.93, -10.96) * mm});
            skLineSegment(sketch, "E91.7.0", {"start": v(6.15, -8.9) * mm, "end": v(5.07, -7.81) * mm});
            skArc(sketch, "E91.7.1", {"start": v(7.85, -10.87) * mm, "mid": v(6.77, -11.73) * mm, "end": v(5.49, -12.23) * mm});
            skLineSegment(sketch, "E91.7.2", {"start": v(7.73, -21.35) * mm, "end": v(7.32, -19.8) * mm});
            skLineSegment(sketch, "E91.7.3", {"start": v(8.35, -23.67) * mm, "end": v(7.94, -22.12) * mm});
            skArc(sketch, "E91.7.4", {"start": v(13.21, -16.24) * mm, "mid": v(10.57, -18.3) * mm, "end": v(7.46, -19.56) * mm});
            skLineSegment(sketch, "E91.7.5", {"start": v(4.63, -9.78) * mm, "end": v(4.23, -8.3) * mm});
            skArc(sketch, "E91.7.6", {"start": v(14.63, -17.65) * mm, "mid": v(11.57, -20.03) * mm, "end": v(7.97, -21.5) * mm});
            skArc(sketch, "E91.7.7", {"start": v(8.12, -11.16) * mm, "mid": v(6.97, -12.07) * mm, "end": v(5.6, -12.61) * mm});
            skLineSegment(sketch, "E91.7.8", {"start": v(9.02, -26.18) * mm, "end": v(8.56, -24.44) * mm, "construction": true});
            skLineSegment(sketch, "E91.7.9", {"start": v(9.54, -12.28) * mm, "end": v(8.4, -11.15) * mm});
            skLineSegment(sketch, "E91.7.10", {"start": v(11.23, -13.98) * mm, "end": v(10.1, -12.85) * mm});
            skLineSegment(sketch, "E91.7.11", {"start": v(6.49, -16.72) * mm, "end": v(6.08, -15.17) * mm});
            skArc(sketch, "E91.7.12", {"start": v(11.51, -14.55) * mm, "mid": v(9.37, -16.22) * mm, "end": v(6.84, -17.24) * mm});
            skLineSegment(sketch, "E91.7.13", {"start": v(7.1, -19.03) * mm, "end": v(6.7, -17.5) * mm});
            skArc(sketch, "E91.7.14", {"start": v(12.93, -15.96) * mm, "mid": v(10.37, -17.95) * mm, "end": v(7.35, -19.18) * mm});
            skLineSegment(sketch, "E91.7.15", {"start": v(5.87, -14.4) * mm, "end": v(5.46, -12.86) * mm});
            skLineSegment(sketch, "E91.7.16", {"start": v(12.93, -15.67) * mm, "end": v(11.8, -14.54) * mm});
            skLineSegment(sketch, "E91.7.17", {"start": v(14.63, -17.37) * mm, "end": v(13.5, -16.24) * mm});
            skLineSegment(sketch, "E91.7.18", {"start": v(16.32, -19.07) * mm, "end": v(15.2, -17.94) * mm});
            skArc(sketch, "E91.7.19", {"start": v(16.6, -19.63) * mm, "mid": v(12.97, -22.46) * mm, "end": v(8.7, -24.2) * mm});
            skLineSegment(sketch, "E91.7.20", {"start": v(14.2, -24.58) * mm, "end": v(4.47, -7.74) * mm, "construction": true});
            skArc(sketch, "E91.7.21", {"start": v(9.54, -12.56) * mm, "mid": v(7.97, -13.8) * mm, "end": v(6.1, -14.54) * mm});
            skLineSegment(sketch, "E91.7.22", {"start": v(7.84, -10.59) * mm, "end": v(6.72, -9.46) * mm});
            skLineSegment(sketch, "E91.7.23", {"start": v(18.16, -20.9) * mm, "end": v(16.89, -19.63) * mm, "construction": true});
            skArc(sketch, "E91.7.24", {"start": v(11.24, -14.26) * mm, "mid": v(9.17, -15.88) * mm, "end": v(6.73, -16.86) * mm});
            skArc(sketch, "E91.7.25", {"start": v(16.32, -19.35) * mm, "mid": v(12.77, -22.1) * mm, "end": v(8.6, -23.81) * mm});
            skArc(sketch, "E91.7.26", {"start": v(14.9, -17.94) * mm, "mid": v(11.77, -20.38) * mm, "end": v(8.08, -21.88) * mm});
            skArc(sketch, "E91.7.27", {"start": v(9.82, -12.85) * mm, "mid": v(8.17, -14.15) * mm, "end": v(6.22, -14.93) * mm});
            skLineSegment(sketch, "E91.7.28", {"start": v(5.25, -12.09) * mm, "end": v(4.84, -10.55) * mm});
            skArc(sketch, "E91.7.29", {"start": v(6.17, -9.17) * mm, "mid": v(5.58, -9.66) * mm, "end": v(4.86, -9.93) * mm});
            skPoint(sketch, "E91.7.30", {"position": v(8.5, -24.25) * mm});
            skPoint(sketch, "E91.7.31", {"position": v(11.37, -14.12) * mm});
            skPoint(sketch, "E91.7.32", {"position": v(14.76, -17.5) * mm});
            skPoint(sketch, "E91.7.33", {"position": v(7.98, -10.72) * mm});
            skPoint(sketch, "E91.7.34", {"position": v(6.02, -14.97) * mm});
            skPoint(sketch, "E91.7.35", {"position": v(4.68, -9.95) * mm});
            skPoint(sketch, "E91.7.36", {"position": v(6.54, -16.9) * mm});
            skPoint(sketch, "E91.7.37", {"position": v(6.56, -9.3) * mm});
            skPoint(sketch, "E91.7.38", {"position": v(13.35, -16.1) * mm});
            skPoint(sketch, "E91.7.39", {"position": v(7.16, -19.22) * mm});
            skPoint(sketch, "E91.7.40", {"position": v(4.78, -10.34) * mm});
            skPoint(sketch, "E91.7.41", {"position": v(11.65, -14.4) * mm});
            skArc(sketch, "E91.7.42", {"start": v(6.43, -9.47) * mm, "mid": v(5.78, -10) * mm, "end": v(4.99, -10.3) * mm});
            skPoint(sketch, "E91.7.43", {"position": v(7.26, -19.6) * mm});
            skLineSegment(sketch, "E91.7.44", {"start": v(5.3, -12.27) * mm, "end": v(4.78, -10.34) * mm});
            skPoint(sketch, "E91.7.45", {"position": v(5.3, -12.27) * mm});
            skPoint(sketch, "E91.7.46", {"position": v(9.96, -12.7) * mm});
            skPoint(sketch, "E91.7.47", {"position": v(16.74, -19.49) * mm});
            skPoint(sketch, "E91.7.48", {"position": v(7.78, -21.54) * mm});
            skLineSegment(sketch, "E91.7.49", {"start": v(9.02, -26.18) * mm, "end": v(4.23, -8.3) * mm});
            skPoint(sketch, "E91.7.50", {"position": v(5.4, -12.66) * mm});
            skPoint(sketch, "E91.7.51", {"position": v(16.46, -19.2) * mm});
            skPoint(sketch, "E91.7.52", {"position": v(9.67, -12.42) * mm});
            skLineSegment(sketch, "E91.7.53", {"start": v(18.16, -20.9) * mm, "end": v(5.07, -7.81) * mm});
            skPoint(sketch, "E91.7.54", {"position": v(7.89, -21.93) * mm});
            skPoint(sketch, "E91.7.55", {"position": v(8.4, -23.86) * mm});
            skPoint(sketch, "E91.7.56", {"position": v(15.05, -17.8) * mm});
            skPoint(sketch, "E91.7.57", {"position": v(8.26, -11) * mm});
            skPoint(sketch, "E91.7.58", {"position": v(5.92, -14.59) * mm});
            skPoint(sketch, "E91.7.59", {"position": v(13.07, -15.81) * mm});
            skPoint(sketch, "E91.7.60", {"position": v(6.64, -17.3) * mm});
            skPoint(sketch, "E91.7.61", {"position": v(6.28, -9.02) * mm});
            skLineSegment(sketch, "E91.7.62", {"start": v(9.02, -26.18) * mm, "end": v(4.23, -8.3) * mm});
            skLineSegment(sketch, "E91.7.63", {"start": v(7.98, -10.72) * mm, "end": v(6.56, -9.3) * mm});
            skArc(sketch, "E91.7.64", {"start": v(7.46, -19.56) * mm, "mid": v(7.34, -19.65) * mm, "end": v(7.32, -19.8) * mm});
            skArc(sketch, "E91.7.65", {"start": v(11.8, -14.54) * mm, "mid": v(11.66, -14.49) * mm, "end": v(11.51, -14.55) * mm});
            skArc(sketch, "E91.7.66", {"start": v(16.89, -19.63) * mm, "mid": v(16.75, -19.57) * mm, "end": v(16.6, -19.63) * mm});
            skArc(sketch, "E91.7.67", {"start": v(11.24, -14.26) * mm, "mid": v(11.3, -14.12) * mm, "end": v(11.23, -13.98) * mm});
            skLineSegment(sketch, "E91.7.68", {"start": v(8.5, -24.25) * mm, "end": v(8.4, -23.86) * mm, "construction": true});
            skLineSegment(sketch, "E91.7.69", {"start": v(9.96, -12.7) * mm, "end": v(9.67, -12.42) * mm});
            skArc(sketch, "E91.7.70", {"start": v(8.35, -23.67) * mm, "mid": v(8.44, -23.8) * mm, "end": v(8.6, -23.81) * mm});
            skArc(sketch, "E91.7.71", {"start": v(8.7, -24.2) * mm, "mid": v(8.58, -24.29) * mm, "end": v(8.56, -24.44) * mm});
            skLineSegment(sketch, "E91.7.72", {"start": v(11.65, -14.4) * mm, "end": v(11.37, -14.12) * mm});
            skLineSegment(sketch, "E91.7.73", {"start": v(6.64, -17.3) * mm, "end": v(6.54, -16.9) * mm});
            skArc(sketch, "E91.7.74", {"start": v(10.1, -12.85) * mm, "mid": v(9.96, -12.79) * mm, "end": v(9.82, -12.85) * mm});
            skArc(sketch, "E91.7.75", {"start": v(15.2, -17.94) * mm, "mid": v(15.05, -17.88) * mm, "end": v(14.9, -17.94) * mm});
            skArc(sketch, "E91.7.76", {"start": v(6.84, -17.24) * mm, "mid": v(6.72, -17.34) * mm, "end": v(6.7, -17.5) * mm});
            skArc(sketch, "E91.7.77", {"start": v(9.54, -12.56) * mm, "mid": v(9.6, -12.42) * mm, "end": v(9.54, -12.28) * mm});
            skArc(sketch, "E91.7.78", {"start": v(13.5, -16.24) * mm, "mid": v(13.35, -16.18) * mm, "end": v(13.21, -16.24) * mm});
            skArc(sketch, "E91.7.79", {"start": v(6.49, -16.72) * mm, "mid": v(6.58, -16.84) * mm, "end": v(6.73, -16.86) * mm});
            skArc(sketch, "E91.7.80", {"start": v(8.4, -11.15) * mm, "mid": v(8.26, -11.1) * mm, "end": v(8.12, -11.16) * mm});
            skLineSegment(sketch, "E91.7.81", {"start": v(4.78, -10.34) * mm, "end": v(4.68, -9.95) * mm});
            skArc(sketch, "E91.7.82", {"start": v(8.08, -21.88) * mm, "mid": v(7.96, -21.97) * mm, "end": v(7.94, -22.12) * mm});
            skArc(sketch, "E91.7.83", {"start": v(5.25, -12.09) * mm, "mid": v(5.34, -12.2) * mm, "end": v(5.49, -12.23) * mm});
            skLineSegment(sketch, "E91.7.84", {"start": v(7.26, -19.6) * mm, "end": v(7.16, -19.22) * mm});
            skArc(sketch, "E91.7.85", {"start": v(7.1, -19.03) * mm, "mid": v(7.2, -19.16) * mm, "end": v(7.35, -19.18) * mm});
            skArc(sketch, "E91.7.86", {"start": v(5.6, -12.61) * mm, "mid": v(5.48, -12.7) * mm, "end": v(5.46, -12.86) * mm});
            skArc(sketch, "E91.7.87", {"start": v(7.73, -21.35) * mm, "mid": v(7.82, -21.47) * mm, "end": v(7.97, -21.5) * mm});
            skArc(sketch, "E91.7.88", {"start": v(12.93, -15.96) * mm, "mid": v(12.99, -15.81) * mm, "end": v(12.93, -15.67) * mm});
            skArc(sketch, "E91.7.89", {"start": v(4.99, -10.3) * mm, "mid": v(4.86, -10.4) * mm, "end": v(4.84, -10.55) * mm});
            skLineSegment(sketch, "E91.7.90", {"start": v(7.89, -21.93) * mm, "end": v(7.78, -21.54) * mm});
            skLineSegment(sketch, "E91.7.91", {"start": v(13.35, -16.1) * mm, "end": v(13.07, -15.81) * mm});
            skArc(sketch, "E91.7.92", {"start": v(5.87, -14.4) * mm, "mid": v(5.96, -14.52) * mm, "end": v(6.1, -14.54) * mm});
            skArc(sketch, "E91.7.93", {"start": v(7.85, -10.87) * mm, "mid": v(7.9, -10.73) * mm, "end": v(7.84, -10.59) * mm});
            skArc(sketch, "E91.7.94", {"start": v(16.32, -19.35) * mm, "mid": v(16.38, -19.2) * mm, "end": v(16.32, -19.07) * mm});
            skLineSegment(sketch, "E91.7.95", {"start": v(15.05, -17.8) * mm, "end": v(14.76, -17.5) * mm});
            skLineSegment(sketch, "E91.7.96", {"start": v(16.74, -19.49) * mm, "end": v(16.46, -19.2) * mm, "construction": true});
            skArc(sketch, "E91.7.97", {"start": v(6.22, -14.93) * mm, "mid": v(6.1, -15.02) * mm, "end": v(6.08, -15.17) * mm});
            skLineSegment(sketch, "E91.7.98", {"start": v(5.4, -12.66) * mm, "end": v(5.3, -12.27) * mm});
            skLineSegment(sketch, "E91.7.99", {"start": v(8.26, -11) * mm, "end": v(7.98, -10.72) * mm});
            skLineSegment(sketch, "E91.7.100", {"start": v(6.02, -14.97) * mm, "end": v(5.92, -14.59) * mm});
            skArc(sketch, "E91.7.101", {"start": v(14.63, -17.65) * mm, "mid": v(14.68, -17.51) * mm, "end": v(14.63, -17.37) * mm});
            skArc(sketch, "E91.7.102", {"start": v(4.63, -9.78) * mm, "mid": v(4.72, -9.9) * mm, "end": v(4.86, -9.93) * mm});
            skLineSegment(sketch, "E91.7.103", {"start": v(6.56, -9.3) * mm, "end": v(6.28, -9.02) * mm});
            skArc(sketch, "E91.7.104", {"start": v(6.72, -9.46) * mm, "mid": v(6.57, -9.4) * mm, "end": v(6.43, -9.47) * mm});
            skArc(sketch, "E91.7.105", {"start": v(6.17, -9.17) * mm, "mid": v(6.21, -9.03) * mm, "end": v(6.15, -8.9) * mm});
            skLineSegment(sketch, "E91.7.106", {"start": v(4.78, -10.34) * mm, "end": v(4.68, -9.95) * mm});
            skLineSegment(sketch, "E91.7.107", {"start": v(6.56, -9.3) * mm, "end": v(6.28, -9.02) * mm});
            skLineSegment(sketch, "E91.8.0", {"start": v(9.78, -4.63) * mm, "end": v(8.3, -4.23) * mm});
            skArc(sketch, "E91.8.1", {"start": v(12.23, -5.49) * mm, "mid": v(11.73, -6.77) * mm, "end": v(10.87, -7.85) * mm});
            skLineSegment(sketch, "E91.8.2", {"start": v(17.37, -14.63) * mm, "end": v(16.24, -13.5) * mm});
            skLineSegment(sketch, "E91.8.3", {"start": v(19.07, -16.32) * mm, "end": v(17.94, -15.2) * mm});
            skArc(sketch, "E91.8.4", {"start": v(19.56, -7.46) * mm, "mid": v(18.3, -10.57) * mm, "end": v(16.24, -13.21) * mm});
            skLineSegment(sketch, "E91.8.5", {"start": v(8.9, -6.15) * mm, "end": v(7.81, -5.07) * mm});
            skArc(sketch, "E91.8.6", {"start": v(21.5, -7.97) * mm, "mid": v(20.03, -11.57) * mm, "end": v(17.65, -14.63) * mm});
            skArc(sketch, "E91.8.7", {"start": v(12.61, -5.6) * mm, "mid": v(12.07, -6.97) * mm, "end": v(11.16, -8.12) * mm});
            skLineSegment(sketch, "E91.8.8", {"start": v(20.9, -18.16) * mm, "end": v(19.63, -16.89) * mm, "construction": true});
            skLineSegment(sketch, "E91.8.9", {"start": v(14.4, -5.87) * mm, "end": v(12.86, -5.46) * mm});
            skLineSegment(sketch, "E91.8.10", {"start": v(16.72, -6.49) * mm, "end": v(15.17, -6.08) * mm});
            skLineSegment(sketch, "E91.8.11", {"start": v(13.98, -11.23) * mm, "end": v(12.85, -10.1) * mm});
            skArc(sketch, "E91.8.12", {"start": v(17.24, -6.84) * mm, "mid": v(16.22, -9.37) * mm, "end": v(14.55, -11.51) * mm});
            skLineSegment(sketch, "E91.8.13", {"start": v(15.67, -12.93) * mm, "end": v(14.54, -11.8) * mm});
            skArc(sketch, "E91.8.14", {"start": v(19.18, -7.35) * mm, "mid": v(17.95, -10.37) * mm, "end": v(15.96, -12.93) * mm});
            skLineSegment(sketch, "E91.8.15", {"start": v(12.28, -9.54) * mm, "end": v(11.15, -8.4) * mm});
            skLineSegment(sketch, "E91.8.16", {"start": v(19.03, -7.1) * mm, "end": v(17.5, -6.7) * mm});
            skLineSegment(sketch, "E91.8.17", {"start": v(21.35, -7.73) * mm, "end": v(19.8, -7.32) * mm});
            skLineSegment(sketch, "E91.8.18", {"start": v(23.67, -8.35) * mm, "end": v(22.12, -7.94) * mm});
            skArc(sketch, "E91.8.19", {"start": v(24.2, -8.7) * mm, "mid": v(22.46, -12.97) * mm, "end": v(19.63, -16.6) * mm});
            skLineSegment(sketch, "E91.8.20", {"start": v(24.58, -14.2) * mm, "end": v(7.74, -4.47) * mm, "construction": true});
            skArc(sketch, "E91.8.21", {"start": v(14.54, -6.1) * mm, "mid": v(13.8, -7.97) * mm, "end": v(12.56, -9.54) * mm});
            skLineSegment(sketch, "E91.8.22", {"start": v(12.09, -5.25) * mm, "end": v(10.55, -4.84) * mm});
            skLineSegment(sketch, "E91.8.23", {"start": v(26.18, -9.02) * mm, "end": v(24.44, -8.56) * mm, "construction": true});
            skArc(sketch, "E91.8.24", {"start": v(16.86, -6.73) * mm, "mid": v(15.88, -9.17) * mm, "end": v(14.26, -11.24) * mm});
            skArc(sketch, "E91.8.25", {"start": v(23.81, -8.6) * mm, "mid": v(22.1, -12.77) * mm, "end": v(19.35, -16.32) * mm});
            skArc(sketch, "E91.8.26", {"start": v(21.88, -8.08) * mm, "mid": v(20.38, -11.77) * mm, "end": v(17.94, -14.9) * mm});
            skArc(sketch, "E91.8.27", {"start": v(14.93, -6.22) * mm, "mid": v(14.15, -8.17) * mm, "end": v(12.85, -9.82) * mm});
            skLineSegment(sketch, "E91.8.28", {"start": v(10.59, -7.84) * mm, "end": v(9.46, -6.72) * mm});
            skArc(sketch, "E91.8.29", {"start": v(9.93, -4.86) * mm, "mid": v(9.66, -5.58) * mm, "end": v(9.17, -6.17) * mm});
            skPoint(sketch, "E91.8.30", {"position": v(19.49, -16.74) * mm});
            skPoint(sketch, "E91.8.31", {"position": v(16.9, -6.54) * mm});
            skPoint(sketch, "E91.8.32", {"position": v(21.54, -7.78) * mm});
            skPoint(sketch, "E91.8.33", {"position": v(12.27, -5.3) * mm});
            skPoint(sketch, "E91.8.34", {"position": v(12.7, -9.96) * mm});
            skPoint(sketch, "E91.8.35", {"position": v(9.02, -6.28) * mm});
            skPoint(sketch, "E91.8.36", {"position": v(14.12, -11.37) * mm});
            skPoint(sketch, "E91.8.37", {"position": v(10.34, -4.78) * mm});
            skPoint(sketch, "E91.8.38", {"position": v(19.6, -7.26) * mm});
            skPoint(sketch, "E91.8.39", {"position": v(15.81, -13.07) * mm});
            skPoint(sketch, "E91.8.40", {"position": v(9.3, -6.56) * mm});
            skPoint(sketch, "E91.8.41", {"position": v(17.3, -6.64) * mm});
            skArc(sketch, "E91.8.42", {"start": v(10.3, -4.99) * mm, "mid": v(10, -5.78) * mm, "end": v(9.47, -6.43) * mm});
            skPoint(sketch, "E91.8.43", {"position": v(16.1, -13.35) * mm});
            skLineSegment(sketch, "E91.8.44", {"start": v(10.72, -7.98) * mm, "end": v(9.3, -6.56) * mm});
            skPoint(sketch, "E91.8.45", {"position": v(10.72, -7.98) * mm});
            skPoint(sketch, "E91.8.46", {"position": v(14.97, -6.02) * mm});
            skPoint(sketch, "E91.8.47", {"position": v(24.25, -8.5) * mm});
            skPoint(sketch, "E91.8.48", {"position": v(17.5, -14.76) * mm});
            skLineSegment(sketch, "E91.8.49", {"start": v(20.9, -18.16) * mm, "end": v(7.81, -5.07) * mm});
            skPoint(sketch, "E91.8.50", {"position": v(11, -8.26) * mm});
            skPoint(sketch, "E91.8.51", {"position": v(23.86, -8.4) * mm});
            skPoint(sketch, "E91.8.52", {"position": v(14.59, -5.92) * mm});
            skLineSegment(sketch, "E91.8.53", {"start": v(26.18, -9.02) * mm, "end": v(8.3, -4.23) * mm});
            skPoint(sketch, "E91.8.54", {"position": v(17.8, -15.05) * mm});
            skPoint(sketch, "E91.8.55", {"position": v(19.2, -16.46) * mm});
            skPoint(sketch, "E91.8.56", {"position": v(21.93, -7.89) * mm});
            skPoint(sketch, "E91.8.57", {"position": v(12.66, -5.4) * mm});
            skPoint(sketch, "E91.8.58", {"position": v(12.42, -9.67) * mm});
            skPoint(sketch, "E91.8.59", {"position": v(19.22, -7.16) * mm});
            skPoint(sketch, "E91.8.60", {"position": v(14.4, -11.65) * mm});
            skPoint(sketch, "E91.8.61", {"position": v(9.95, -4.68) * mm});
            skLineSegment(sketch, "E91.8.62", {"start": v(20.9, -18.16) * mm, "end": v(7.81, -5.07) * mm});
            skLineSegment(sketch, "E91.8.63", {"start": v(12.27, -5.3) * mm, "end": v(10.34, -4.78) * mm});
            skArc(sketch, "E91.8.64", {"start": v(16.24, -13.21) * mm, "mid": v(16.18, -13.35) * mm, "end": v(16.24, -13.5) * mm});
            skArc(sketch, "E91.8.65", {"start": v(17.5, -6.7) * mm, "mid": v(17.34, -6.72) * mm, "end": v(17.24, -6.84) * mm});
            skArc(sketch, "E91.8.66", {"start": v(24.44, -8.56) * mm, "mid": v(24.29, -8.58) * mm, "end": v(24.2, -8.7) * mm});
            skArc(sketch, "E91.8.67", {"start": v(16.86, -6.73) * mm, "mid": v(16.84, -6.58) * mm, "end": v(16.72, -6.49) * mm});
            skLineSegment(sketch, "E91.8.68", {"start": v(19.49, -16.74) * mm, "end": v(19.2, -16.46) * mm, "construction": true});
            skLineSegment(sketch, "E91.8.69", {"start": v(14.97, -6.02) * mm, "end": v(14.59, -5.92) * mm});
            skArc(sketch, "E91.8.70", {"start": v(19.07, -16.32) * mm, "mid": v(19.2, -16.38) * mm, "end": v(19.35, -16.32) * mm});
            skArc(sketch, "E91.8.71", {"start": v(19.63, -16.6) * mm, "mid": v(19.57, -16.75) * mm, "end": v(19.63, -16.89) * mm});
            skLineSegment(sketch, "E91.8.72", {"start": v(17.3, -6.64) * mm, "end": v(16.9, -6.54) * mm});
            skLineSegment(sketch, "E91.8.73", {"start": v(14.4, -11.65) * mm, "end": v(14.12, -11.37) * mm});
            skArc(sketch, "E91.8.74", {"start": v(15.17, -6.08) * mm, "mid": v(15.02, -6.1) * mm, "end": v(14.93, -6.22) * mm});
            skArc(sketch, "E91.8.75", {"start": v(22.12, -7.94) * mm, "mid": v(21.97, -7.96) * mm, "end": v(21.88, -8.08) * mm});
            skArc(sketch, "E91.8.76", {"start": v(14.55, -11.51) * mm, "mid": v(14.49, -11.66) * mm, "end": v(14.54, -11.8) * mm});
            skArc(sketch, "E91.8.77", {"start": v(14.54, -6.1) * mm, "mid": v(14.52, -5.96) * mm, "end": v(14.4, -5.87) * mm});
            skArc(sketch, "E91.8.78", {"start": v(19.8, -7.32) * mm, "mid": v(19.65, -7.34) * mm, "end": v(19.56, -7.46) * mm});
            skArc(sketch, "E91.8.79", {"start": v(13.98, -11.23) * mm, "mid": v(14.12, -11.3) * mm, "end": v(14.26, -11.24) * mm});
            skArc(sketch, "E91.8.80", {"start": v(12.86, -5.46) * mm, "mid": v(12.7, -5.48) * mm, "end": v(12.61, -5.6) * mm});
            skLineSegment(sketch, "E91.8.81", {"start": v(9.3, -6.56) * mm, "end": v(9.02, -6.28) * mm});
            skArc(sketch, "E91.8.82", {"start": v(17.94, -14.9) * mm, "mid": v(17.88, -15.05) * mm, "end": v(17.94, -15.2) * mm});
            skArc(sketch, "E91.8.83", {"start": v(10.59, -7.84) * mm, "mid": v(10.73, -7.9) * mm, "end": v(10.87, -7.85) * mm});
            skLineSegment(sketch, "E91.8.84", {"start": v(16.1, -13.35) * mm, "end": v(15.81, -13.07) * mm});
            skArc(sketch, "E91.8.85", {"start": v(15.67, -12.93) * mm, "mid": v(15.81, -12.99) * mm, "end": v(15.96, -12.93) * mm});
            skArc(sketch, "E91.8.86", {"start": v(11.16, -8.12) * mm, "mid": v(11.1, -8.26) * mm, "end": v(11.15, -8.4) * mm});
            skArc(sketch, "E91.8.87", {"start": v(17.37, -14.63) * mm, "mid": v(17.51, -14.68) * mm, "end": v(17.65, -14.63) * mm});
            skArc(sketch, "E91.8.88", {"start": v(19.18, -7.35) * mm, "mid": v(19.16, -7.2) * mm, "end": v(19.03, -7.1) * mm});
            skArc(sketch, "E91.8.89", {"start": v(9.47, -6.43) * mm, "mid": v(9.4, -6.57) * mm, "end": v(9.46, -6.72) * mm});
            skLineSegment(sketch, "E91.8.90", {"start": v(17.8, -15.05) * mm, "end": v(17.5, -14.76) * mm});
            skLineSegment(sketch, "E91.8.91", {"start": v(19.6, -7.26) * mm, "end": v(19.22, -7.16) * mm});
            skArc(sketch, "E91.8.92", {"start": v(12.28, -9.54) * mm, "mid": v(12.42, -9.6) * mm, "end": v(12.56, -9.54) * mm});
            skArc(sketch, "E91.8.93", {"start": v(12.23, -5.49) * mm, "mid": v(12.2, -5.34) * mm, "end": v(12.09, -5.25) * mm});
            skArc(sketch, "E91.8.94", {"start": v(23.81, -8.6) * mm, "mid": v(23.8, -8.44) * mm, "end": v(23.67, -8.35) * mm});
            skLineSegment(sketch, "E91.8.95", {"start": v(21.93, -7.89) * mm, "end": v(21.54, -7.78) * mm});
            skLineSegment(sketch, "E91.8.96", {"start": v(24.25, -8.5) * mm, "end": v(23.86, -8.4) * mm, "construction": true});
            skArc(sketch, "E91.8.97", {"start": v(12.85, -9.82) * mm, "mid": v(12.79, -9.96) * mm, "end": v(12.85, -10.1) * mm});
            skLineSegment(sketch, "E91.8.98", {"start": v(11, -8.26) * mm, "end": v(10.72, -7.98) * mm});
            skLineSegment(sketch, "E91.8.99", {"start": v(12.66, -5.4) * mm, "end": v(12.27, -5.3) * mm});
            skLineSegment(sketch, "E91.8.100", {"start": v(12.7, -9.96) * mm, "end": v(12.42, -9.67) * mm});
            skArc(sketch, "E91.8.101", {"start": v(21.5, -7.97) * mm, "mid": v(21.47, -7.82) * mm, "end": v(21.35, -7.73) * mm});
            skArc(sketch, "E91.8.102", {"start": v(8.9, -6.15) * mm, "mid": v(9.03, -6.21) * mm, "end": v(9.17, -6.17) * mm});
            skLineSegment(sketch, "E91.8.103", {"start": v(10.34, -4.78) * mm, "end": v(9.95, -4.68) * mm});
            skArc(sketch, "E91.8.104", {"start": v(10.55, -4.84) * mm, "mid": v(10.4, -4.86) * mm, "end": v(10.3, -4.99) * mm});
            skArc(sketch, "E91.8.105", {"start": v(9.93, -4.86) * mm, "mid": v(9.9, -4.72) * mm, "end": v(9.78, -4.63) * mm});
            skLineSegment(sketch, "E91.8.106", {"start": v(9.3, -6.56) * mm, "end": v(9.02, -6.28) * mm});
            skLineSegment(sketch, "E91.8.107", {"start": v(10.34, -4.78) * mm, "end": v(9.95, -4.68) * mm});
            skLineSegment(sketch, "E91.9.0", {"start": v(10.79, 0.88) * mm, "end": v(9.3, 0.48) * mm});
            skArc(sketch, "E91.9.1", {"start": v(13.33, 1.36) * mm, "mid": v(13.54, 0) * mm, "end": v(13.33, -1.36) * mm});
            skLineSegment(sketch, "E91.9.2", {"start": v(22.36, -3.98) * mm, "end": v(20.81, -3.57) * mm});
            skLineSegment(sketch, "E91.9.3", {"start": v(24.67, -4.6) * mm, "end": v(23.13, -4.19) * mm});
            skArc(sketch, "E91.9.4", {"start": v(20.67, 3.32) * mm, "mid": v(21.13, 0) * mm, "end": v(20.67, -3.32) * mm});
            skLineSegment(sketch, "E91.9.5", {"start": v(10.79, -0.88) * mm, "end": v(9.3, -0.48) * mm});
            skArc(sketch, "E91.9.6", {"start": v(22.6, 3.84) * mm, "mid": v(23.13, 0) * mm, "end": v(22.6, -3.84) * mm});
            skArc(sketch, "E91.9.7", {"start": v(13.72, 1.45) * mm, "mid": v(13.94, 0) * mm, "end": v(13.72, -1.45) * mm});
            skLineSegment(sketch, "E91.9.8", {"start": v(27.18, -5.27) * mm, "end": v(25.45, -4.8) * mm, "construction": true});
            skLineSegment(sketch, "E91.9.9", {"start": v(15.4, 2.12) * mm, "end": v(13.86, 1.7) * mm});
            skLineSegment(sketch, "E91.9.10", {"start": v(17.72, 2.74) * mm, "end": v(16.18, 2.33) * mm});
            skLineSegment(sketch, "E91.9.11", {"start": v(17.72, -2.74) * mm, "end": v(16.18, -2.33) * mm});
            skArc(sketch, "E91.9.12", {"start": v(18.35, 2.7) * mm, "mid": v(18.73, 0) * mm, "end": v(18.35, -2.7) * mm});
            skLineSegment(sketch, "E91.9.13", {"start": v(20.04, -3.36) * mm, "end": v(18.5, -2.95) * mm});
            skArc(sketch, "E91.9.14", {"start": v(20.28, 3.22) * mm, "mid": v(20.73, 0) * mm, "end": v(20.28, -3.22) * mm});
            skLineSegment(sketch, "E91.9.15", {"start": v(15.4, -2.12) * mm, "end": v(13.86, -1.7) * mm});
            skLineSegment(sketch, "E91.9.16", {"start": v(20.04, 3.36) * mm, "end": v(18.5, 2.95) * mm});
            skLineSegment(sketch, "E91.9.17", {"start": v(22.36, 3.98) * mm, "end": v(20.81, 3.57) * mm});
            skLineSegment(sketch, "E91.9.18", {"start": v(24.67, 4.6) * mm, "end": v(23.13, 4.19) * mm});
            skArc(sketch, "E91.9.19", {"start": v(25.3, 4.56) * mm, "mid": v(25.93, 0) * mm, "end": v(25.3, -4.56) * mm});
            skLineSegment(sketch, "E91.9.20", {"start": v(28.38, 0) * mm, "end": v(8.93, 0) * mm, "construction": true});
            skArc(sketch, "E91.9.21", {"start": v(15.65, 1.98) * mm, "mid": v(15.94, 0) * mm, "end": v(15.65, -1.98) * mm});
            skLineSegment(sketch, "E91.9.22", {"start": v(13.1, 1.5) * mm, "end": v(11.56, 1.09) * mm});
            skLineSegment(sketch, "E91.9.23", {"start": v(27.18, 5.27) * mm, "end": v(25.45, 4.8) * mm, "construction": true});
            skArc(sketch, "E91.9.24", {"start": v(17.97, 2.6) * mm, "mid": v(18.33, 0) * mm, "end": v(17.97, -2.6) * mm});
            skArc(sketch, "E91.9.25", {"start": v(24.92, 4.46) * mm, "mid": v(25.53, 0) * mm, "end": v(24.92, -4.46) * mm});
            skArc(sketch, "E91.9.26", {"start": v(22.99, 3.94) * mm, "mid": v(23.53, 0) * mm, "end": v(22.99, -3.94) * mm});
            skArc(sketch, "E91.9.27", {"start": v(16.04, 2.08) * mm, "mid": v(16.34, 0) * mm, "end": v(16.04, -2.08) * mm});
            skLineSegment(sketch, "E91.9.28", {"start": v(13.1, -1.5) * mm, "end": v(11.56, -1.09) * mm});
            skArc(sketch, "E91.9.29", {"start": v(11.03, 0.75) * mm, "mid": v(11.16, 0) * mm, "end": v(11.03, -0.75) * mm});
            skPoint(sketch, "E91.9.30", {"position": v(25.25, -4.76) * mm});
            skPoint(sketch, "E91.9.31", {"position": v(17.9, 2.79) * mm});
            skPoint(sketch, "E91.9.32", {"position": v(22.55, 4.03) * mm});
            skPoint(sketch, "E91.9.33", {"position": v(13.27, 1.55) * mm});
            skPoint(sketch, "E91.9.34", {"position": v(15.98, -2.27) * mm});
            skPoint(sketch, "E91.9.35", {"position": v(10.96, -0.93) * mm});
            skPoint(sketch, "E91.9.36", {"position": v(17.9, -2.79) * mm});
            skPoint(sketch, "E91.9.37", {"position": v(11.34, 1.03) * mm});
            skPoint(sketch, "E91.9.38", {"position": v(20.61, 3.51) * mm});
            skPoint(sketch, "E91.9.39", {"position": v(20.23, -3.41) * mm});
            skPoint(sketch, "E91.9.40", {"position": v(11.34, -1.03) * mm});
            skPoint(sketch, "E91.9.41", {"position": v(18.3, 2.9) * mm});
            skArc(sketch, "E91.9.42", {"start": v(11.42, 0.83) * mm, "mid": v(11.55, 0) * mm, "end": v(11.42, -0.83) * mm});
            skPoint(sketch, "E91.9.43", {"position": v(20.61, -3.51) * mm});
            skLineSegment(sketch, "E91.9.44", {"start": v(13.27, -1.55) * mm, "end": v(11.34, -1.03) * mm});
            skPoint(sketch, "E91.9.45", {"position": v(13.27, -1.55) * mm});
            skPoint(sketch, "E91.9.46", {"position": v(15.98, 2.27) * mm});
            skPoint(sketch, "E91.9.47", {"position": v(25.25, 4.76) * mm});
            skPoint(sketch, "E91.9.48", {"position": v(22.55, -4.03) * mm});
            skLineSegment(sketch, "E91.9.49", {"start": v(27.18, -5.27) * mm, "end": v(9.3, -0.48) * mm});
            skPoint(sketch, "E91.9.50", {"position": v(13.66, -1.65) * mm});
            skPoint(sketch, "E91.9.51", {"position": v(24.86, 4.65) * mm});
            skPoint(sketch, "E91.9.52", {"position": v(15.6, 2.17) * mm});
            skLineSegment(sketch, "E91.9.53", {"start": v(27.18, 5.27) * mm, "end": v(9.3, 0.48) * mm});
            skPoint(sketch, "E91.9.54", {"position": v(22.93, -4.14) * mm});
            skPoint(sketch, "E91.9.55", {"position": v(24.86, -4.65) * mm});
            skPoint(sketch, "E91.9.56", {"position": v(22.93, 4.14) * mm});
            skPoint(sketch, "E91.9.57", {"position": v(13.66, 1.65) * mm});
            skPoint(sketch, "E91.9.58", {"position": v(15.6, -2.17) * mm});
            skPoint(sketch, "E91.9.59", {"position": v(20.23, 3.41) * mm});
            skPoint(sketch, "E91.9.60", {"position": v(18.3, -2.9) * mm});
            skPoint(sketch, "E91.9.61", {"position": v(10.96, 0.93) * mm});
            skLineSegment(sketch, "E91.9.62", {"start": v(27.18, -5.27) * mm, "end": v(9.3, -0.48) * mm});
            skLineSegment(sketch, "E91.9.63", {"start": v(13.27, 1.55) * mm, "end": v(11.34, 1.03) * mm});
            skArc(sketch, "E91.9.64", {"start": v(20.67, -3.32) * mm, "mid": v(20.69, -3.47) * mm, "end": v(20.81, -3.57) * mm});
            skArc(sketch, "E91.9.65", {"start": v(18.5, 2.95) * mm, "mid": v(18.37, 2.85) * mm, "end": v(18.35, 2.7) * mm});
            skArc(sketch, "E91.9.66", {"start": v(25.45, 4.8) * mm, "mid": v(25.33, 4.71) * mm, "end": v(25.3, 4.56) * mm});
            skArc(sketch, "E91.9.67", {"start": v(17.97, 2.6) * mm, "mid": v(17.87, 2.72) * mm, "end": v(17.72, 2.74) * mm});
            skLineSegment(sketch, "E91.9.68", {"start": v(25.25, -4.76) * mm, "end": v(24.86, -4.65) * mm, "construction": true});
            skLineSegment(sketch, "E91.9.69", {"start": v(15.98, 2.27) * mm, "end": v(15.6, 2.17) * mm});
            skArc(sketch, "E91.9.70", {"start": v(24.67, -4.6) * mm, "mid": v(24.83, -4.58) * mm, "end": v(24.92, -4.46) * mm});
            skArc(sketch, "E91.9.71", {"start": v(25.3, -4.56) * mm, "mid": v(25.33, -4.71) * mm, "end": v(25.45, -4.8) * mm});
            skLineSegment(sketch, "E91.9.72", {"start": v(18.3, 2.9) * mm, "end": v(17.9, 2.79) * mm});
            skLineSegment(sketch, "E91.9.73", {"start": v(18.3, -2.9) * mm, "end": v(17.9, -2.79) * mm});
            skArc(sketch, "E91.9.74", {"start": v(16.18, 2.33) * mm, "mid": v(16.06, 2.23) * mm, "end": v(16.04, 2.08) * mm});
            skArc(sketch, "E91.9.75", {"start": v(23.13, 4.19) * mm, "mid": v(23, 4.1) * mm, "end": v(22.99, 3.94) * mm});
            skArc(sketch, "E91.9.76", {"start": v(18.35, -2.7) * mm, "mid": v(18.37, -2.85) * mm, "end": v(18.5, -2.95) * mm});
            skArc(sketch, "E91.9.77", {"start": v(15.65, 1.98) * mm, "mid": v(15.56, 2.1) * mm, "end": v(15.4, 2.12) * mm});
            skArc(sketch, "E91.9.78", {"start": v(20.81, 3.57) * mm, "mid": v(20.69, 3.47) * mm, "end": v(20.67, 3.32) * mm});
            skArc(sketch, "E91.9.79", {"start": v(17.72, -2.74) * mm, "mid": v(17.87, -2.72) * mm, "end": v(17.97, -2.6) * mm});
            skArc(sketch, "E91.9.80", {"start": v(13.86, 1.7) * mm, "mid": v(13.74, 1.6) * mm, "end": v(13.72, 1.45) * mm});
            skLineSegment(sketch, "E91.9.81", {"start": v(11.34, -1.03) * mm, "end": v(10.96, -0.93) * mm});
            skArc(sketch, "E91.9.82", {"start": v(22.99, -3.94) * mm, "mid": v(23, -4.1) * mm, "end": v(23.13, -4.19) * mm});
            skArc(sketch, "E91.9.83", {"start": v(13.1, -1.5) * mm, "mid": v(13.24, -1.48) * mm, "end": v(13.33, -1.36) * mm});
            skLineSegment(sketch, "E91.9.84", {"start": v(20.61, -3.51) * mm, "end": v(20.23, -3.41) * mm});
            skArc(sketch, "E91.9.85", {"start": v(20.04, -3.36) * mm, "mid": v(20.19, -3.34) * mm, "end": v(20.28, -3.22) * mm});
            skArc(sketch, "E91.9.86", {"start": v(13.72, -1.45) * mm, "mid": v(13.74, -1.6) * mm, "end": v(13.86, -1.7) * mm});
            skArc(sketch, "E91.9.87", {"start": v(22.36, -3.98) * mm, "mid": v(22.5, -3.96) * mm, "end": v(22.6, -3.84) * mm});
            skArc(sketch, "E91.9.88", {"start": v(20.28, 3.22) * mm, "mid": v(20.19, 3.34) * mm, "end": v(20.04, 3.36) * mm});
            skArc(sketch, "E91.9.89", {"start": v(11.42, -0.83) * mm, "mid": v(11.43, -0.99) * mm, "end": v(11.56, -1.09) * mm});
            skLineSegment(sketch, "E91.9.90", {"start": v(22.93, -4.14) * mm, "end": v(22.55, -4.03) * mm});
            skLineSegment(sketch, "E91.9.91", {"start": v(20.61, 3.51) * mm, "end": v(20.23, 3.41) * mm});
            skArc(sketch, "E91.9.92", {"start": v(15.4, -2.12) * mm, "mid": v(15.56, -2.1) * mm, "end": v(15.65, -1.98) * mm});
            skArc(sketch, "E91.9.93", {"start": v(13.33, 1.36) * mm, "mid": v(13.24, 1.48) * mm, "end": v(13.1, 1.5) * mm});
            skArc(sketch, "E91.9.94", {"start": v(24.92, 4.46) * mm, "mid": v(24.83, 4.58) * mm, "end": v(24.67, 4.6) * mm});
            skLineSegment(sketch, "E91.9.95", {"start": v(22.93, 4.14) * mm, "end": v(22.55, 4.03) * mm});
            skLineSegment(sketch, "E91.9.96", {"start": v(25.25, 4.76) * mm, "end": v(24.86, 4.65) * mm, "construction": true});
            skArc(sketch, "E91.9.97", {"start": v(16.04, -2.08) * mm, "mid": v(16.06, -2.23) * mm, "end": v(16.18, -2.33) * mm});
            skLineSegment(sketch, "E91.9.98", {"start": v(13.66, -1.65) * mm, "end": v(13.27, -1.55) * mm});
            skLineSegment(sketch, "E91.9.99", {"start": v(13.66, 1.65) * mm, "end": v(13.27, 1.55) * mm});
            skLineSegment(sketch, "E91.9.100", {"start": v(15.98, -2.27) * mm, "end": v(15.6, -2.17) * mm});
            skArc(sketch, "E91.9.101", {"start": v(22.6, 3.84) * mm, "mid": v(22.5, 3.96) * mm, "end": v(22.36, 3.98) * mm});
            skArc(sketch, "E91.9.102", {"start": v(10.79, -0.88) * mm, "mid": v(10.93, -0.86) * mm, "end": v(11.03, -0.75) * mm});
            skLineSegment(sketch, "E91.9.103", {"start": v(11.34, 1.03) * mm, "end": v(10.96, 0.93) * mm});
            skArc(sketch, "E91.9.104", {"start": v(11.56, 1.09) * mm, "mid": v(11.43, 0.99) * mm, "end": v(11.42, 0.83) * mm});
            skArc(sketch, "E91.9.105", {"start": v(11.03, 0.75) * mm, "mid": v(10.93, 0.86) * mm, "end": v(10.79, 0.88) * mm});
            skLineSegment(sketch, "E91.9.106", {"start": v(11.34, -1.03) * mm, "end": v(10.96, -0.93) * mm});
            skLineSegment(sketch, "E91.9.107", {"start": v(11.34, 1.03) * mm, "end": v(10.96, 0.93) * mm});
            skLineSegment(sketch, "E91.10.0", {"start": v(8.9, 6.15) * mm, "end": v(7.81, 5.07) * mm});
            skArc(sketch, "E91.10.1", {"start": v(10.87, 7.85) * mm, "mid": v(11.73, 6.77) * mm, "end": v(12.23, 5.49) * mm});
            skLineSegment(sketch, "E91.10.2", {"start": v(21.35, 7.73) * mm, "end": v(19.8, 7.32) * mm});
            skLineSegment(sketch, "E91.10.3", {"start": v(23.67, 8.35) * mm, "end": v(22.12, 7.94) * mm});
            skArc(sketch, "E91.10.4", {"start": v(16.24, 13.21) * mm, "mid": v(18.3, 10.57) * mm, "end": v(19.56, 7.46) * mm});
            skLineSegment(sketch, "E91.10.5", {"start": v(9.78, 4.63) * mm, "end": v(8.3, 4.23) * mm});
            skArc(sketch, "E91.10.6", {"start": v(17.65, 14.63) * mm, "mid": v(20.03, 11.57) * mm, "end": v(21.5, 7.97) * mm});
            skArc(sketch, "E91.10.7", {"start": v(11.16, 8.12) * mm, "mid": v(12.07, 6.97) * mm, "end": v(12.61, 5.6) * mm});
            skLineSegment(sketch, "E91.10.8", {"start": v(26.18, 9.02) * mm, "end": v(24.44, 8.56) * mm, "construction": true});
            skLineSegment(sketch, "E91.10.9", {"start": v(12.28, 9.54) * mm, "end": v(11.15, 8.4) * mm});
            skLineSegment(sketch, "E91.10.10", {"start": v(13.98, 11.23) * mm, "end": v(12.85, 10.1) * mm});
            skLineSegment(sketch, "E91.10.11", {"start": v(16.72, 6.49) * mm, "end": v(15.17, 6.08) * mm});
            skArc(sketch, "E91.10.12", {"start": v(14.55, 11.51) * mm, "mid": v(16.22, 9.37) * mm, "end": v(17.24, 6.84) * mm});
            skLineSegment(sketch, "E91.10.13", {"start": v(19.03, 7.1) * mm, "end": v(17.5, 6.7) * mm});
            skArc(sketch, "E91.10.14", {"start": v(15.96, 12.93) * mm, "mid": v(17.95, 10.37) * mm, "end": v(19.18, 7.35) * mm});
            skLineSegment(sketch, "E91.10.15", {"start": v(14.4, 5.87) * mm, "end": v(12.86, 5.46) * mm});
            skLineSegment(sketch, "E91.10.16", {"start": v(15.67, 12.93) * mm, "end": v(14.54, 11.8) * mm});
            skLineSegment(sketch, "E91.10.17", {"start": v(17.37, 14.63) * mm, "end": v(16.24, 13.5) * mm});
            skLineSegment(sketch, "E91.10.18", {"start": v(19.07, 16.32) * mm, "end": v(17.94, 15.2) * mm});
            skArc(sketch, "E91.10.19", {"start": v(19.63, 16.6) * mm, "mid": v(22.46, 12.97) * mm, "end": v(24.2, 8.7) * mm});
            skLineSegment(sketch, "E91.10.20", {"start": v(24.58, 14.2) * mm, "end": v(7.74, 4.47) * mm, "construction": true});
            skArc(sketch, "E91.10.21", {"start": v(12.56, 9.54) * mm, "mid": v(13.8, 7.97) * mm, "end": v(14.54, 6.1) * mm});
            skLineSegment(sketch, "E91.10.22", {"start": v(10.59, 7.84) * mm, "end": v(9.46, 6.72) * mm});
            skLineSegment(sketch, "E91.10.23", {"start": v(20.9, 18.16) * mm, "end": v(19.63, 16.89) * mm, "construction": true});
            skArc(sketch, "E91.10.24", {"start": v(14.26, 11.24) * mm, "mid": v(15.88, 9.17) * mm, "end": v(16.86, 6.73) * mm});
            skArc(sketch, "E91.10.25", {"start": v(19.35, 16.32) * mm, "mid": v(22.1, 12.77) * mm, "end": v(23.81, 8.6) * mm});
            skArc(sketch, "E91.10.26", {"start": v(17.94, 14.9) * mm, "mid": v(20.38, 11.77) * mm, "end": v(21.88, 8.08) * mm});
            skArc(sketch, "E91.10.27", {"start": v(12.85, 9.82) * mm, "mid": v(14.15, 8.17) * mm, "end": v(14.93, 6.22) * mm});
            skLineSegment(sketch, "E91.10.28", {"start": v(12.09, 5.25) * mm, "end": v(10.55, 4.84) * mm});
            skArc(sketch, "E91.10.29", {"start": v(9.17, 6.17) * mm, "mid": v(9.66, 5.58) * mm, "end": v(9.93, 4.86) * mm});
            skPoint(sketch, "E91.10.30", {"position": v(24.25, 8.5) * mm});
            skPoint(sketch, "E91.10.31", {"position": v(14.12, 11.37) * mm});
            skPoint(sketch, "E91.10.32", {"position": v(17.5, 14.76) * mm});
            skPoint(sketch, "E91.10.33", {"position": v(10.72, 7.98) * mm});
            skPoint(sketch, "E91.10.34", {"position": v(14.97, 6.02) * mm});
            skPoint(sketch, "E91.10.35", {"position": v(9.95, 4.68) * mm});
            skPoint(sketch, "E91.10.36", {"position": v(16.9, 6.54) * mm});
            skPoint(sketch, "E91.10.37", {"position": v(9.3, 6.56) * mm});
            skPoint(sketch, "E91.10.38", {"position": v(16.1, 13.35) * mm});
            skPoint(sketch, "E91.10.39", {"position": v(19.22, 7.16) * mm});
            skPoint(sketch, "E91.10.40", {"position": v(10.34, 4.78) * mm});
            skPoint(sketch, "E91.10.41", {"position": v(14.4, 11.65) * mm});
            skArc(sketch, "E91.10.42", {"start": v(9.47, 6.43) * mm, "mid": v(10, 5.78) * mm, "end": v(10.3, 4.99) * mm});
            skPoint(sketch, "E91.10.43", {"position": v(19.6, 7.26) * mm});
            skLineSegment(sketch, "E91.10.44", {"start": v(12.27, 5.3) * mm, "end": v(10.34, 4.78) * mm});
            skPoint(sketch, "E91.10.45", {"position": v(12.27, 5.3) * mm});
            skPoint(sketch, "E91.10.46", {"position": v(12.7, 9.96) * mm});
            skPoint(sketch, "E91.10.47", {"position": v(19.49, 16.74) * mm});
            skPoint(sketch, "E91.10.48", {"position": v(21.54, 7.78) * mm});
            skLineSegment(sketch, "E91.10.49", {"start": v(26.18, 9.02) * mm, "end": v(8.3, 4.23) * mm});
            skPoint(sketch, "E91.10.50", {"position": v(12.66, 5.4) * mm});
            skPoint(sketch, "E91.10.51", {"position": v(19.2, 16.46) * mm});
            skPoint(sketch, "E91.10.52", {"position": v(12.42, 9.67) * mm});
            skLineSegment(sketch, "E91.10.53", {"start": v(20.9, 18.16) * mm, "end": v(7.81, 5.07) * mm});
            skPoint(sketch, "E91.10.54", {"position": v(21.93, 7.89) * mm});
            skPoint(sketch, "E91.10.55", {"position": v(23.86, 8.4) * mm});
            skPoint(sketch, "E91.10.56", {"position": v(17.8, 15.05) * mm});
            skPoint(sketch, "E91.10.57", {"position": v(11, 8.26) * mm});
            skPoint(sketch, "E91.10.58", {"position": v(14.59, 5.92) * mm});
            skPoint(sketch, "E91.10.59", {"position": v(15.81, 13.07) * mm});
            skPoint(sketch, "E91.10.60", {"position": v(17.3, 6.64) * mm});
            skPoint(sketch, "E91.10.61", {"position": v(9.02, 6.28) * mm});
            skLineSegment(sketch, "E91.10.62", {"start": v(26.18, 9.02) * mm, "end": v(8.3, 4.23) * mm});
            skLineSegment(sketch, "E91.10.63", {"start": v(10.72, 7.98) * mm, "end": v(9.3, 6.56) * mm});
            skArc(sketch, "E91.10.64", {"start": v(19.56, 7.46) * mm, "mid": v(19.65, 7.34) * mm, "end": v(19.8, 7.32) * mm});
            skArc(sketch, "E91.10.65", {"start": v(14.54, 11.8) * mm, "mid": v(14.49, 11.66) * mm, "end": v(14.55, 11.51) * mm});
            skArc(sketch, "E91.10.66", {"start": v(19.63, 16.89) * mm, "mid": v(19.57, 16.75) * mm, "end": v(19.63, 16.6) * mm});
            skArc(sketch, "E91.10.67", {"start": v(14.26, 11.24) * mm, "mid": v(14.12, 11.3) * mm, "end": v(13.98, 11.23) * mm});
            skLineSegment(sketch, "E91.10.68", {"start": v(24.25, 8.5) * mm, "end": v(23.86, 8.4) * mm, "construction": true});
            skLineSegment(sketch, "E91.10.69", {"start": v(12.7, 9.96) * mm, "end": v(12.42, 9.67) * mm});
            skArc(sketch, "E91.10.70", {"start": v(23.67, 8.35) * mm, "mid": v(23.8, 8.44) * mm, "end": v(23.81, 8.6) * mm});
            skArc(sketch, "E91.10.71", {"start": v(24.2, 8.7) * mm, "mid": v(24.29, 8.58) * mm, "end": v(24.44, 8.56) * mm});
            skLineSegment(sketch, "E91.10.72", {"start": v(14.4, 11.65) * mm, "end": v(14.12, 11.37) * mm});
            skLineSegment(sketch, "E91.10.73", {"start": v(17.3, 6.64) * mm, "end": v(16.9, 6.54) * mm});
            skArc(sketch, "E91.10.74", {"start": v(12.85, 10.1) * mm, "mid": v(12.79, 9.96) * mm, "end": v(12.85, 9.82) * mm});
            skArc(sketch, "E91.10.75", {"start": v(17.94, 15.2) * mm, "mid": v(17.88, 15.05) * mm, "end": v(17.94, 14.9) * mm});
            skArc(sketch, "E91.10.76", {"start": v(17.24, 6.84) * mm, "mid": v(17.34, 6.72) * mm, "end": v(17.5, 6.7) * mm});
            skArc(sketch, "E91.10.77", {"start": v(12.56, 9.54) * mm, "mid": v(12.42, 9.6) * mm, "end": v(12.28, 9.54) * mm});
            skArc(sketch, "E91.10.78", {"start": v(16.24, 13.5) * mm, "mid": v(16.18, 13.35) * mm, "end": v(16.24, 13.21) * mm});
            skArc(sketch, "E91.10.79", {"start": v(16.72, 6.49) * mm, "mid": v(16.84, 6.58) * mm, "end": v(16.86, 6.73) * mm});
            skArc(sketch, "E91.10.80", {"start": v(11.15, 8.4) * mm, "mid": v(11.1, 8.26) * mm, "end": v(11.16, 8.12) * mm});
            skLineSegment(sketch, "E91.10.81", {"start": v(10.34, 4.78) * mm, "end": v(9.95, 4.68) * mm});
            skArc(sketch, "E91.10.82", {"start": v(21.88, 8.08) * mm, "mid": v(21.97, 7.96) * mm, "end": v(22.12, 7.94) * mm});
            skArc(sketch, "E91.10.83", {"start": v(12.09, 5.25) * mm, "mid": v(12.2, 5.34) * mm, "end": v(12.23, 5.49) * mm});
            skLineSegment(sketch, "E91.10.84", {"start": v(19.6, 7.26) * mm, "end": v(19.22, 7.16) * mm});
            skArc(sketch, "E91.10.85", {"start": v(19.03, 7.1) * mm, "mid": v(19.16, 7.2) * mm, "end": v(19.18, 7.35) * mm});
            skArc(sketch, "E91.10.86", {"start": v(12.61, 5.6) * mm, "mid": v(12.7, 5.48) * mm, "end": v(12.86, 5.46) * mm});
            skArc(sketch, "E91.10.87", {"start": v(21.35, 7.73) * mm, "mid": v(21.47, 7.82) * mm, "end": v(21.5, 7.97) * mm});
            skArc(sketch, "E91.10.88", {"start": v(15.96, 12.93) * mm, "mid": v(15.81, 12.99) * mm, "end": v(15.67, 12.93) * mm});
            skArc(sketch, "E91.10.89", {"start": v(10.3, 4.99) * mm, "mid": v(10.4, 4.86) * mm, "end": v(10.55, 4.84) * mm});
            skLineSegment(sketch, "E91.10.90", {"start": v(21.93, 7.89) * mm, "end": v(21.54, 7.78) * mm});
            skLineSegment(sketch, "E91.10.91", {"start": v(16.1, 13.35) * mm, "end": v(15.81, 13.07) * mm});
            skArc(sketch, "E91.10.92", {"start": v(14.4, 5.87) * mm, "mid": v(14.52, 5.96) * mm, "end": v(14.54, 6.1) * mm});
            skArc(sketch, "E91.10.93", {"start": v(10.87, 7.85) * mm, "mid": v(10.73, 7.9) * mm, "end": v(10.59, 7.84) * mm});
            skArc(sketch, "E91.10.94", {"start": v(19.35, 16.32) * mm, "mid": v(19.2, 16.38) * mm, "end": v(19.07, 16.32) * mm});
            skLineSegment(sketch, "E91.10.95", {"start": v(17.8, 15.05) * mm, "end": v(17.5, 14.76) * mm});
            skLineSegment(sketch, "E91.10.96", {"start": v(19.49, 16.74) * mm, "end": v(19.2, 16.46) * mm, "construction": true});
            skArc(sketch, "E91.10.97", {"start": v(14.93, 6.22) * mm, "mid": v(15.02, 6.1) * mm, "end": v(15.17, 6.08) * mm});
            skLineSegment(sketch, "E91.10.98", {"start": v(12.66, 5.4) * mm, "end": v(12.27, 5.3) * mm});
            skLineSegment(sketch, "E91.10.99", {"start": v(11, 8.26) * mm, "end": v(10.72, 7.98) * mm});
            skLineSegment(sketch, "E91.10.100", {"start": v(14.97, 6.02) * mm, "end": v(14.59, 5.92) * mm});
            skArc(sketch, "E91.10.101", {"start": v(17.65, 14.63) * mm, "mid": v(17.51, 14.68) * mm, "end": v(17.37, 14.63) * mm});
            skArc(sketch, "E91.10.102", {"start": v(9.78, 4.63) * mm, "mid": v(9.9, 4.72) * mm, "end": v(9.93, 4.86) * mm});
            skLineSegment(sketch, "E91.10.103", {"start": v(9.3, 6.56) * mm, "end": v(9.02, 6.28) * mm});
            skArc(sketch, "E91.10.104", {"start": v(9.46, 6.72) * mm, "mid": v(9.4, 6.57) * mm, "end": v(9.47, 6.43) * mm});
            skArc(sketch, "E91.10.105", {"start": v(9.17, 6.17) * mm, "mid": v(9.03, 6.21) * mm, "end": v(8.9, 6.15) * mm});
            skLineSegment(sketch, "E91.10.106", {"start": v(10.34, 4.78) * mm, "end": v(9.95, 4.68) * mm});
            skLineSegment(sketch, "E91.10.107", {"start": v(9.3, 6.56) * mm, "end": v(9.02, 6.28) * mm});
            skLineSegment(sketch, "E91.11.0", {"start": v(4.63, 9.78) * mm, "end": v(4.23, 8.3) * mm});
            skArc(sketch, "E91.11.1", {"start": v(5.49, 12.23) * mm, "mid": v(6.77, 11.73) * mm, "end": v(7.85, 10.87) * mm});
            skLineSegment(sketch, "E91.11.2", {"start": v(14.63, 17.37) * mm, "end": v(13.5, 16.24) * mm});
            skLineSegment(sketch, "E91.11.3", {"start": v(16.32, 19.07) * mm, "end": v(15.2, 17.94) * mm});
            skArc(sketch, "E91.11.4", {"start": v(7.46, 19.56) * mm, "mid": v(10.57, 18.3) * mm, "end": v(13.21, 16.24) * mm});
            skLineSegment(sketch, "E91.11.5", {"start": v(6.15, 8.9) * mm, "end": v(5.07, 7.81) * mm});
            skArc(sketch, "E91.11.6", {"start": v(7.97, 21.5) * mm, "mid": v(11.57, 20.03) * mm, "end": v(14.63, 17.65) * mm});
            skArc(sketch, "E91.11.7", {"start": v(5.6, 12.61) * mm, "mid": v(6.97, 12.07) * mm, "end": v(8.12, 11.16) * mm});
            skLineSegment(sketch, "E91.11.8", {"start": v(18.16, 20.9) * mm, "end": v(16.89, 19.63) * mm, "construction": true});
            skLineSegment(sketch, "E91.11.9", {"start": v(5.87, 14.4) * mm, "end": v(5.46, 12.86) * mm});
            skLineSegment(sketch, "E91.11.10", {"start": v(6.49, 16.72) * mm, "end": v(6.08, 15.17) * mm});
            skLineSegment(sketch, "E91.11.11", {"start": v(11.23, 13.98) * mm, "end": v(10.1, 12.85) * mm});
            skArc(sketch, "E91.11.12", {"start": v(6.84, 17.24) * mm, "mid": v(9.37, 16.22) * mm, "end": v(11.51, 14.55) * mm});
            skLineSegment(sketch, "E91.11.13", {"start": v(12.93, 15.67) * mm, "end": v(11.8, 14.54) * mm});
            skArc(sketch, "E91.11.14", {"start": v(7.35, 19.18) * mm, "mid": v(10.37, 17.95) * mm, "end": v(12.93, 15.96) * mm});
            skLineSegment(sketch, "E91.11.15", {"start": v(9.54, 12.28) * mm, "end": v(8.4, 11.15) * mm});
            skLineSegment(sketch, "E91.11.16", {"start": v(7.1, 19.03) * mm, "end": v(6.7, 17.5) * mm});
            skLineSegment(sketch, "E91.11.17", {"start": v(7.73, 21.35) * mm, "end": v(7.32, 19.8) * mm});
            skLineSegment(sketch, "E91.11.18", {"start": v(8.35, 23.67) * mm, "end": v(7.94, 22.12) * mm});
            skArc(sketch, "E91.11.19", {"start": v(8.7, 24.2) * mm, "mid": v(12.97, 22.46) * mm, "end": v(16.6, 19.63) * mm});
            skLineSegment(sketch, "E91.11.20", {"start": v(14.2, 24.58) * mm, "end": v(4.47, 7.74) * mm, "construction": true});
            skArc(sketch, "E91.11.21", {"start": v(6.1, 14.54) * mm, "mid": v(7.97, 13.8) * mm, "end": v(9.54, 12.56) * mm});
            skLineSegment(sketch, "E91.11.22", {"start": v(5.25, 12.09) * mm, "end": v(4.84, 10.55) * mm});
            skLineSegment(sketch, "E91.11.23", {"start": v(9.02, 26.18) * mm, "end": v(8.56, 24.44) * mm, "construction": true});
            skArc(sketch, "E91.11.24", {"start": v(6.73, 16.86) * mm, "mid": v(9.17, 15.88) * mm, "end": v(11.24, 14.26) * mm});
            skArc(sketch, "E91.11.25", {"start": v(8.6, 23.81) * mm, "mid": v(12.77, 22.1) * mm, "end": v(16.32, 19.35) * mm});
            skArc(sketch, "E91.11.26", {"start": v(8.08, 21.88) * mm, "mid": v(11.77, 20.38) * mm, "end": v(14.9, 17.94) * mm});
            skArc(sketch, "E91.11.27", {"start": v(6.22, 14.93) * mm, "mid": v(8.17, 14.15) * mm, "end": v(9.82, 12.85) * mm});
            skLineSegment(sketch, "E91.11.28", {"start": v(7.84, 10.59) * mm, "end": v(6.72, 9.46) * mm});
            skArc(sketch, "E91.11.29", {"start": v(4.86, 9.93) * mm, "mid": v(5.58, 9.66) * mm, "end": v(6.17, 9.17) * mm});
            skPoint(sketch, "E91.11.30", {"position": v(16.74, 19.49) * mm});
            skPoint(sketch, "E91.11.31", {"position": v(6.54, 16.9) * mm});
            skPoint(sketch, "E91.11.32", {"position": v(7.78, 21.54) * mm});
            skPoint(sketch, "E91.11.33", {"position": v(5.3, 12.27) * mm});
            skPoint(sketch, "E91.11.34", {"position": v(9.96, 12.7) * mm});
            skPoint(sketch, "E91.11.35", {"position": v(6.28, 9.02) * mm});
            skPoint(sketch, "E91.11.36", {"position": v(11.37, 14.12) * mm});
            skPoint(sketch, "E91.11.37", {"position": v(4.78, 10.34) * mm});
            skPoint(sketch, "E91.11.38", {"position": v(7.26, 19.6) * mm});
            skPoint(sketch, "E91.11.39", {"position": v(13.07, 15.81) * mm});
            skPoint(sketch, "E91.11.40", {"position": v(6.56, 9.3) * mm});
            skPoint(sketch, "E91.11.41", {"position": v(6.64, 17.3) * mm});
            skArc(sketch, "E91.11.42", {"start": v(4.99, 10.3) * mm, "mid": v(5.78, 10) * mm, "end": v(6.43, 9.47) * mm});
            skPoint(sketch, "E91.11.43", {"position": v(13.35, 16.1) * mm});
            skLineSegment(sketch, "E91.11.44", {"start": v(7.98, 10.72) * mm, "end": v(6.56, 9.3) * mm});
            skPoint(sketch, "E91.11.45", {"position": v(7.98, 10.72) * mm});
            skPoint(sketch, "E91.11.46", {"position": v(6.02, 14.97) * mm});
            skPoint(sketch, "E91.11.47", {"position": v(8.5, 24.25) * mm});
            skPoint(sketch, "E91.11.48", {"position": v(14.76, 17.5) * mm});
            skLineSegment(sketch, "E91.11.49", {"start": v(18.16, 20.9) * mm, "end": v(5.07, 7.81) * mm});
            skPoint(sketch, "E91.11.50", {"position": v(8.26, 11) * mm});
            skPoint(sketch, "E91.11.51", {"position": v(8.4, 23.86) * mm});
            skPoint(sketch, "E91.11.52", {"position": v(5.92, 14.59) * mm});
            skLineSegment(sketch, "E91.11.53", {"start": v(9.02, 26.18) * mm, "end": v(4.23, 8.3) * mm});
            skPoint(sketch, "E91.11.54", {"position": v(15.05, 17.8) * mm});
            skPoint(sketch, "E91.11.55", {"position": v(16.46, 19.2) * mm});
            skPoint(sketch, "E91.11.56", {"position": v(7.89, 21.93) * mm});
            skPoint(sketch, "E91.11.57", {"position": v(5.4, 12.66) * mm});
            skPoint(sketch, "E91.11.58", {"position": v(9.67, 12.42) * mm});
            skPoint(sketch, "E91.11.59", {"position": v(7.16, 19.22) * mm});
            skPoint(sketch, "E91.11.60", {"position": v(11.65, 14.4) * mm});
            skPoint(sketch, "E91.11.61", {"position": v(4.68, 9.95) * mm});
            skLineSegment(sketch, "E91.11.62", {"start": v(18.16, 20.9) * mm, "end": v(5.07, 7.81) * mm});
            skLineSegment(sketch, "E91.11.63", {"start": v(5.3, 12.27) * mm, "end": v(4.78, 10.34) * mm});
            skArc(sketch, "E91.11.64", {"start": v(13.21, 16.24) * mm, "mid": v(13.35, 16.18) * mm, "end": v(13.5, 16.24) * mm});
            skArc(sketch, "E91.11.65", {"start": v(6.7, 17.5) * mm, "mid": v(6.72, 17.34) * mm, "end": v(6.84, 17.24) * mm});
            skArc(sketch, "E91.11.66", {"start": v(8.56, 24.44) * mm, "mid": v(8.58, 24.29) * mm, "end": v(8.7, 24.2) * mm});
            skArc(sketch, "E91.11.67", {"start": v(6.73, 16.86) * mm, "mid": v(6.58, 16.84) * mm, "end": v(6.49, 16.72) * mm});
            skLineSegment(sketch, "E91.11.68", {"start": v(16.74, 19.49) * mm, "end": v(16.46, 19.2) * mm, "construction": true});
            skLineSegment(sketch, "E91.11.69", {"start": v(6.02, 14.97) * mm, "end": v(5.92, 14.59) * mm});
            skArc(sketch, "E91.11.70", {"start": v(16.32, 19.07) * mm, "mid": v(16.38, 19.2) * mm, "end": v(16.32, 19.35) * mm});
            skArc(sketch, "E91.11.71", {"start": v(16.6, 19.63) * mm, "mid": v(16.75, 19.57) * mm, "end": v(16.89, 19.63) * mm});
            skLineSegment(sketch, "E91.11.72", {"start": v(6.64, 17.3) * mm, "end": v(6.54, 16.9) * mm});
            skLineSegment(sketch, "E91.11.73", {"start": v(11.65, 14.4) * mm, "end": v(11.37, 14.12) * mm});
            skArc(sketch, "E91.11.74", {"start": v(6.08, 15.17) * mm, "mid": v(6.1, 15.02) * mm, "end": v(6.22, 14.93) * mm});
            skArc(sketch, "E91.11.75", {"start": v(7.94, 22.12) * mm, "mid": v(7.96, 21.97) * mm, "end": v(8.08, 21.88) * mm});
            skArc(sketch, "E91.11.76", {"start": v(11.51, 14.55) * mm, "mid": v(11.66, 14.49) * mm, "end": v(11.8, 14.54) * mm});
            skArc(sketch, "E91.11.77", {"start": v(6.1, 14.54) * mm, "mid": v(5.96, 14.52) * mm, "end": v(5.87, 14.4) * mm});
            skArc(sketch, "E91.11.78", {"start": v(7.32, 19.8) * mm, "mid": v(7.34, 19.65) * mm, "end": v(7.46, 19.56) * mm});
            skArc(sketch, "E91.11.79", {"start": v(11.23, 13.98) * mm, "mid": v(11.3, 14.12) * mm, "end": v(11.24, 14.26) * mm});
            skArc(sketch, "E91.11.80", {"start": v(5.46, 12.86) * mm, "mid": v(5.48, 12.7) * mm, "end": v(5.6, 12.61) * mm});
            skLineSegment(sketch, "E91.11.81", {"start": v(6.56, 9.3) * mm, "end": v(6.28, 9.02) * mm});
            skArc(sketch, "E91.11.82", {"start": v(14.9, 17.94) * mm, "mid": v(15.05, 17.88) * mm, "end": v(15.2, 17.94) * mm});
            skArc(sketch, "E91.11.83", {"start": v(7.84, 10.59) * mm, "mid": v(7.9, 10.73) * mm, "end": v(7.85, 10.87) * mm});
            skLineSegment(sketch, "E91.11.84", {"start": v(13.35, 16.1) * mm, "end": v(13.07, 15.81) * mm});
            skArc(sketch, "E91.11.85", {"start": v(12.93, 15.67) * mm, "mid": v(12.99, 15.81) * mm, "end": v(12.93, 15.96) * mm});
            skArc(sketch, "E91.11.86", {"start": v(8.12, 11.16) * mm, "mid": v(8.26, 11.1) * mm, "end": v(8.4, 11.15) * mm});
            skArc(sketch, "E91.11.87", {"start": v(14.63, 17.37) * mm, "mid": v(14.68, 17.51) * mm, "end": v(14.63, 17.65) * mm});
            skArc(sketch, "E91.11.88", {"start": v(7.35, 19.18) * mm, "mid": v(7.2, 19.16) * mm, "end": v(7.1, 19.03) * mm});
            skArc(sketch, "E91.11.89", {"start": v(6.43, 9.47) * mm, "mid": v(6.57, 9.4) * mm, "end": v(6.72, 9.46) * mm});
            skLineSegment(sketch, "E91.11.90", {"start": v(15.05, 17.8) * mm, "end": v(14.76, 17.5) * mm});
            skLineSegment(sketch, "E91.11.91", {"start": v(7.26, 19.6) * mm, "end": v(7.16, 19.22) * mm});
            skArc(sketch, "E91.11.92", {"start": v(9.54, 12.28) * mm, "mid": v(9.6, 12.42) * mm, "end": v(9.54, 12.56) * mm});
            skArc(sketch, "E91.11.93", {"start": v(5.49, 12.23) * mm, "mid": v(5.34, 12.2) * mm, "end": v(5.25, 12.09) * mm});
            skArc(sketch, "E91.11.94", {"start": v(8.6, 23.81) * mm, "mid": v(8.44, 23.8) * mm, "end": v(8.35, 23.67) * mm});
            skLineSegment(sketch, "E91.11.95", {"start": v(7.89, 21.93) * mm, "end": v(7.78, 21.54) * mm});
            skLineSegment(sketch, "E91.11.96", {"start": v(8.5, 24.25) * mm, "end": v(8.4, 23.86) * mm, "construction": true});
            skArc(sketch, "E91.11.97", {"start": v(9.82, 12.85) * mm, "mid": v(9.96, 12.79) * mm, "end": v(10.1, 12.85) * mm});
            skLineSegment(sketch, "E91.11.98", {"start": v(8.26, 11) * mm, "end": v(7.98, 10.72) * mm});
            skLineSegment(sketch, "E91.11.99", {"start": v(5.4, 12.66) * mm, "end": v(5.3, 12.27) * mm});
            skLineSegment(sketch, "E91.11.100", {"start": v(9.96, 12.7) * mm, "end": v(9.67, 12.42) * mm});
            skArc(sketch, "E91.11.101", {"start": v(7.97, 21.5) * mm, "mid": v(7.82, 21.47) * mm, "end": v(7.73, 21.35) * mm});
            skArc(sketch, "E91.11.102", {"start": v(6.15, 8.9) * mm, "mid": v(6.21, 9.03) * mm, "end": v(6.17, 9.17) * mm});
            skLineSegment(sketch, "E91.11.103", {"start": v(4.78, 10.34) * mm, "end": v(4.68, 9.95) * mm});
            skArc(sketch, "E91.11.104", {"start": v(4.84, 10.55) * mm, "mid": v(4.86, 10.4) * mm, "end": v(4.99, 10.3) * mm});
            skArc(sketch, "E91.11.105", {"start": v(4.86, 9.93) * mm, "mid": v(4.72, 9.9) * mm, "end": v(4.63, 9.78) * mm});
            skLineSegment(sketch, "E91.11.106", {"start": v(6.56, 9.3) * mm, "end": v(6.28, 9.02) * mm});
            skLineSegment(sketch, "E91.11.107", {"start": v(4.78, 10.34) * mm, "end": v(4.68, 9.95) * mm});
            skPoint(sketch, "E91.center", {"position": v(0, 0) * mm});
            skSolve(sketch);
        }
        {
            var Q0;
            Q0=makeQuery(id+"F8.imprint","IMPRINT",FACE,{"disambiguationData":[TD([[makeQuery(id+"F8.imprint","IMPRINT",EDGE,{"derivedFrom":sQuery(id+"F8.wireOp",EDGE,"E45")}),-1.0]])]});
            var Q1;
            {var subQ5=sQuery(id+"F8.wireOp",EDGE,"E19");Q1=makeQuery(id+"F8.imprint","IMPRINT",FACE,{"disambiguationData":[TD([[makeQuery(id+"F8.imprint","IMPRINT",EDGE,{"derivedFrom":subQ5}),-1.0]])]});}
            var Q2;
            {var subQ3=sQuery(id+"F8.wireOp",EDGE,"E21");Q2=makeQuery(id+"F8.imprint","IMPRINT",FACE,{"disambiguationData":[TD([[makeQuery(id+"F8.imprint","IMPRINT",EDGE,{"derivedFrom":subQ3}),-1.0]])]});}
            var Q3;
            {var subQ5=sQuery(id+"F8.wireOp",EDGE,"E23");Q3=makeQuery(id+"F8.imprint","IMPRINT",FACE,{"disambiguationData":[TD([[makeQuery(id+"F8.imprint","IMPRINT",EDGE,{"derivedFrom":subQ5}),-1.0]])]});}
            var Q4;
            {var subQ4=sQuery(id+"F8.wireOp",EDGE,"E25");Q4=makeQuery(id+"F8.imprint","IMPRINT",FACE,{"disambiguationData":[TD([[makeQuery(id+"F8.imprint","IMPRINT",EDGE,{"derivedFrom":subQ4}),-1.0]])]});}
            var Q5;
            {var subQ4=sQuery(id+"F8.wireOp",EDGE,"E27");Q5=makeQuery(id+"F8.imprint","IMPRINT",FACE,{"disambiguationData":[TD([[makeQuery(id+"F8.imprint","IMPRINT",EDGE,{"derivedFrom":subQ4}),-1.0]])]});}
            var Q6;
            Q6=makeQuery(id+"F8.imprint","IMPRINT",FACE,{"disambiguationData":[TD([[makeQuery(id+"F8.imprint","IMPRINT",EDGE,{"derivedFrom":sQuery(id+"F8.wireOp",EDGE,"E57")}),-1.0]])]});
            var Q7;
            Q7=makeQuery(id+"F8.imprint","IMPRINT",FACE,{"disambiguationData":[TD([[makeQuery(id+"F8.imprint","IMPRINT",EDGE,{"derivedFrom":sQuery(id+"F8.wireOp",EDGE,"E91.11.19")}),-1.0]])]});
            var Q8;
            Q8=makeQuery(id+"F8.imprint","IMPRINT",FACE,{"disambiguationData":[TD([[makeQuery(id+"F8.imprint","IMPRINT",EDGE,{"derivedFrom":sQuery(id+"F8.wireOp",EDGE,"E91.11.6")}),1.0]])]});
            var Q9;
            Q9=makeQuery(id+"F8.imprint","IMPRINT",FACE,{"disambiguationData":[TD([[makeQuery(id+"F8.imprint","IMPRINT",EDGE,{"derivedFrom":sQuery(id+"F8.wireOp",EDGE,"E91.11.4")}),-1.0]])]});
            var Q10;
            Q10=makeQuery(id+"F8.imprint","IMPRINT",FACE,{"disambiguationData":[TD([[makeQuery(id+"F8.imprint","IMPRINT",EDGE,{"derivedFrom":sQuery(id+"F8.wireOp",EDGE,"E91.11.12")}),-1.0]])]});
            var Q11;
            Q11=makeQuery(id+"F8.imprint","IMPRINT",FACE,{"disambiguationData":[TD([[makeQuery(id+"F8.imprint","IMPRINT",EDGE,{"derivedFrom":sQuery(id+"F8.wireOp",EDGE,"E91.11.21")}),1.0]])]});
            var Q12;
            Q12=makeQuery(id+"F8.imprint","IMPRINT",FACE,{"disambiguationData":[TD([[makeQuery(id+"F8.imprint","IMPRINT",EDGE,{"derivedFrom":sQuery(id+"F8.wireOp",EDGE,"E91.11.1")}),1.0]])]});
            var Q13;
            Q13=makeQuery(id+"F8.imprint","IMPRINT",FACE,{"disambiguationData":[TD([[makeQuery(id+"F8.imprint","IMPRINT",EDGE,{"derivedFrom":sQuery(id+"F8.wireOp",EDGE,"E91.11.29")}),1.0]])]});
            var Q14;
            Q14=makeQuery(id+"F8.imprint","IMPRINT",FACE,{"disambiguationData":[TD([[makeQuery(id+"F8.imprint","IMPRINT",EDGE,{"derivedFrom":sQuery(id+"F8.wireOp",EDGE,"E91.10.29")}),1.0]])]});
            var Q15;
            Q15=makeQuery(id+"F8.imprint","IMPRINT",FACE,{"disambiguationData":[TD([[makeQuery(id+"F8.imprint","IMPRINT",EDGE,{"derivedFrom":sQuery(id+"F8.wireOp",EDGE,"E91.10.1")}),1.0]])]});
            var Q16;
            Q16=makeQuery(id+"F8.imprint","IMPRINT",FACE,{"disambiguationData":[TD([[makeQuery(id+"F8.imprint","IMPRINT",EDGE,{"derivedFrom":sQuery(id+"F8.wireOp",EDGE,"E91.10.21")}),1.0]])]});
            var Q17;
            Q17=makeQuery(id+"F8.imprint","IMPRINT",FACE,{"disambiguationData":[TD([[makeQuery(id+"F8.imprint","IMPRINT",EDGE,{"derivedFrom":sQuery(id+"F8.wireOp",EDGE,"E91.10.12")}),-1.0]])]});
            var Q18;
            Q18=makeQuery(id+"F8.imprint","IMPRINT",FACE,{"disambiguationData":[TD([[makeQuery(id+"F8.imprint","IMPRINT",EDGE,{"derivedFrom":sQuery(id+"F8.wireOp",EDGE,"E91.10.4")}),-1.0]])]});
            var Q19;
            Q19=makeQuery(id+"F8.imprint","IMPRINT",FACE,{"disambiguationData":[TD([[makeQuery(id+"F8.imprint","IMPRINT",EDGE,{"derivedFrom":sQuery(id+"F8.wireOp",EDGE,"E91.10.6")}),1.0]])]});
            var Q20;
            Q20=makeQuery(id+"F8.imprint","IMPRINT",FACE,{"disambiguationData":[TD([[makeQuery(id+"F8.imprint","IMPRINT",EDGE,{"derivedFrom":sQuery(id+"F8.wireOp",EDGE,"E91.10.19")}),-1.0]])]});
            var Q21;
            Q21=makeQuery(id+"F8.imprint","IMPRINT",FACE,{"disambiguationData":[TD([[makeQuery(id+"F8.imprint","IMPRINT",EDGE,{"derivedFrom":sQuery(id+"F8.wireOp",EDGE,"E91.10.6")}),1.0]])]});
            var Q22;
            Q22=makeQuery(id+"F8.imprint","IMPRINT",FACE,{"disambiguationData":[TD([[makeQuery(id+"F8.imprint","IMPRINT",EDGE,{"derivedFrom":sQuery(id+"F8.wireOp",EDGE,"E91.9.29")}),1.0]])]});
            var Q23;
            Q23=makeQuery(id+"F8.imprint","IMPRINT",FACE,{"disambiguationData":[TD([[makeQuery(id+"F8.imprint","IMPRINT",EDGE,{"derivedFrom":sQuery(id+"F8.wireOp",EDGE,"E91.9.1")}),1.0]])]});
            var Q24;
            Q24=makeQuery(id+"F8.imprint","IMPRINT",FACE,{"disambiguationData":[TD([[makeQuery(id+"F8.imprint","IMPRINT",EDGE,{"derivedFrom":sQuery(id+"F8.wireOp",EDGE,"E91.9.21")}),1.0]])]});
            var Q25;
            Q25=makeQuery(id+"F8.imprint","IMPRINT",FACE,{"disambiguationData":[TD([[makeQuery(id+"F8.imprint","IMPRINT",EDGE,{"derivedFrom":sQuery(id+"F8.wireOp",EDGE,"E91.9.12")}),-1.0]])]});
            var Q26;
            Q26=makeQuery(id+"F8.imprint","IMPRINT",FACE,{"disambiguationData":[TD([[makeQuery(id+"F8.imprint","IMPRINT",EDGE,{"derivedFrom":sQuery(id+"F8.wireOp",EDGE,"E91.9.4")}),-1.0]])]});
            var Q27;
            Q27=makeQuery(id+"F8.imprint","IMPRINT",FACE,{"disambiguationData":[TD([[makeQuery(id+"F8.imprint","IMPRINT",EDGE,{"derivedFrom":sQuery(id+"F8.wireOp",EDGE,"E91.9.6")}),1.0]])]});
            var Q28;
            Q28=makeQuery(id+"F8.imprint","IMPRINT",FACE,{"disambiguationData":[TD([[makeQuery(id+"F8.imprint","IMPRINT",EDGE,{"derivedFrom":sQuery(id+"F8.wireOp",EDGE,"E91.9.19")}),-1.0]])]});
            var Q29;
            Q29=makeQuery(id+"F8.imprint","IMPRINT",FACE,{"disambiguationData":[TD([[makeQuery(id+"F8.imprint","IMPRINT",EDGE,{"derivedFrom":sQuery(id+"F8.wireOp",EDGE,"E91.8.29")}),1.0]])]});
            var Q30;
            Q30=makeQuery(id+"F8.imprint","IMPRINT",FACE,{"disambiguationData":[TD([[makeQuery(id+"F8.imprint","IMPRINT",EDGE,{"derivedFrom":sQuery(id+"F8.wireOp",EDGE,"E91.8.1")}),1.0]])]});
            var Q31;
            Q31=makeQuery(id+"F8.imprint","IMPRINT",FACE,{"disambiguationData":[TD([[makeQuery(id+"F8.imprint","IMPRINT",EDGE,{"derivedFrom":sQuery(id+"F8.wireOp",EDGE,"E91.8.21")}),1.0]])]});
            var Q32;
            Q32=makeQuery(id+"F8.imprint","IMPRINT",FACE,{"disambiguationData":[TD([[makeQuery(id+"F8.imprint","IMPRINT",EDGE,{"derivedFrom":sQuery(id+"F8.wireOp",EDGE,"E91.8.12")}),-1.0]])]});
            var Q33;
            Q33=makeQuery(id+"F8.imprint","IMPRINT",FACE,{"disambiguationData":[TD([[makeQuery(id+"F8.imprint","IMPRINT",EDGE,{"derivedFrom":sQuery(id+"F8.wireOp",EDGE,"E91.8.4")}),-1.0]])]});
            var Q34;
            Q34=makeQuery(id+"F8.imprint","IMPRINT",FACE,{"disambiguationData":[TD([[makeQuery(id+"F8.imprint","IMPRINT",EDGE,{"derivedFrom":sQuery(id+"F8.wireOp",EDGE,"E91.8.6")}),1.0]])]});
            var Q35;
            Q35=makeQuery(id+"F8.imprint","IMPRINT",FACE,{"disambiguationData":[TD([[makeQuery(id+"F8.imprint","IMPRINT",EDGE,{"derivedFrom":sQuery(id+"F8.wireOp",EDGE,"E91.8.19")}),-1.0]])]});
            var Q36;
            Q36=makeQuery(id+"F8.imprint","IMPRINT",FACE,{"disambiguationData":[TD([[makeQuery(id+"F8.imprint","IMPRINT",EDGE,{"derivedFrom":sQuery(id+"F8.wireOp",EDGE,"E91.7.29")}),1.0]])]});
            var Q37;
            Q37=makeQuery(id+"F8.imprint","IMPRINT",FACE,{"disambiguationData":[TD([[makeQuery(id+"F8.imprint","IMPRINT",EDGE,{"derivedFrom":sQuery(id+"F8.wireOp",EDGE,"E91.7.1")}),1.0]])]});
            var Q38;
            Q38=makeQuery(id+"F8.imprint","IMPRINT",FACE,{"disambiguationData":[TD([[makeQuery(id+"F8.imprint","IMPRINT",EDGE,{"derivedFrom":sQuery(id+"F8.wireOp",EDGE,"E91.7.21")}),1.0]])]});
            var Q39;
            Q39=makeQuery(id+"F8.imprint","IMPRINT",FACE,{"disambiguationData":[TD([[makeQuery(id+"F8.imprint","IMPRINT",EDGE,{"derivedFrom":sQuery(id+"F8.wireOp",EDGE,"E91.7.12")}),-1.0]])]});
            var Q40;
            Q40=makeQuery(id+"F8.imprint","IMPRINT",FACE,{"disambiguationData":[TD([[makeQuery(id+"F8.imprint","IMPRINT",EDGE,{"derivedFrom":sQuery(id+"F8.wireOp",EDGE,"E91.7.4")}),-1.0]])]});
            var Q41;
            Q41=makeQuery(id+"F8.imprint","IMPRINT",FACE,{"disambiguationData":[TD([[makeQuery(id+"F8.imprint","IMPRINT",EDGE,{"derivedFrom":sQuery(id+"F8.wireOp",EDGE,"E91.7.6")}),1.0]])]});
            var Q42;
            Q42=makeQuery(id+"F8.imprint","IMPRINT",FACE,{"disambiguationData":[TD([[makeQuery(id+"F8.imprint","IMPRINT",EDGE,{"derivedFrom":sQuery(id+"F8.wireOp",EDGE,"E91.7.19")}),-1.0]])]});
            var Q43;
            Q43=makeQuery(id+"F8.imprint","IMPRINT",FACE,{"disambiguationData":[TD([[makeQuery(id+"F8.imprint","IMPRINT",EDGE,{"derivedFrom":sQuery(id+"F8.wireOp",EDGE,"E91.6.29")}),1.0]])]});
            var Q44;
            Q44=makeQuery(id+"F8.imprint","IMPRINT",FACE,{"disambiguationData":[TD([[makeQuery(id+"F8.imprint","IMPRINT",EDGE,{"derivedFrom":sQuery(id+"F8.wireOp",EDGE,"E91.6.1")}),1.0]])]});
            var Q45;
            Q45=makeQuery(id+"F8.imprint","IMPRINT",FACE,{"disambiguationData":[TD([[makeQuery(id+"F8.imprint","IMPRINT",EDGE,{"derivedFrom":sQuery(id+"F8.wireOp",EDGE,"E91.6.21")}),1.0]])]});
            var Q46;
            Q46=makeQuery(id+"F8.imprint","IMPRINT",FACE,{"disambiguationData":[TD([[makeQuery(id+"F8.imprint","IMPRINT",EDGE,{"derivedFrom":sQuery(id+"F8.wireOp",EDGE,"E91.6.12")}),-1.0]])]});
            var Q47;
            Q47=makeQuery(id+"F8.imprint","IMPRINT",FACE,{"disambiguationData":[TD([[makeQuery(id+"F8.imprint","IMPRINT",EDGE,{"derivedFrom":sQuery(id+"F8.wireOp",EDGE,"E91.6.4")}),-1.0]])]});
            var Q48;
            Q48=makeQuery(id+"F8.imprint","IMPRINT",FACE,{"disambiguationData":[TD([[makeQuery(id+"F8.imprint","IMPRINT",EDGE,{"derivedFrom":sQuery(id+"F8.wireOp",EDGE,"E91.6.6")}),1.0]])]});
            var Q49;
            Q49=makeQuery(id+"F8.imprint","IMPRINT",FACE,{"disambiguationData":[TD([[makeQuery(id+"F8.imprint","IMPRINT",EDGE,{"derivedFrom":sQuery(id+"F8.wireOp",EDGE,"E91.6.19")}),-1.0]])]});
            var Q50;
            Q50=makeQuery(id+"F8.imprint","IMPRINT",FACE,{"disambiguationData":[TD([[makeQuery(id+"F8.imprint","IMPRINT",EDGE,{"derivedFrom":sQuery(id+"F8.wireOp",EDGE,"E91.5.19")}),-1.0]])]});
            var Q51;
            Q51=makeQuery(id+"F8.imprint","IMPRINT",FACE,{"disambiguationData":[TD([[makeQuery(id+"F8.imprint","IMPRINT",EDGE,{"derivedFrom":sQuery(id+"F8.wireOp",EDGE,"E91.5.6")}),1.0]])]});
            var Q52;
            Q52=makeQuery(id+"F8.imprint","IMPRINT",FACE,{"disambiguationData":[TD([[makeQuery(id+"F8.imprint","IMPRINT",EDGE,{"derivedFrom":sQuery(id+"F8.wireOp",EDGE,"E91.5.4")}),-1.0]])]});
            var Q53;
            Q53=makeQuery(id+"F8.imprint","IMPRINT",FACE,{"disambiguationData":[TD([[makeQuery(id+"F8.imprint","IMPRINT",EDGE,{"derivedFrom":sQuery(id+"F8.wireOp",EDGE,"E91.5.12")}),-1.0]])]});
            var Q54;
            Q54=makeQuery(id+"F8.imprint","IMPRINT",FACE,{"disambiguationData":[TD([[makeQuery(id+"F8.imprint","IMPRINT",EDGE,{"derivedFrom":sQuery(id+"F8.wireOp",EDGE,"E91.5.21")}),1.0]])]});
            var Q55;
            Q55=makeQuery(id+"F8.imprint","IMPRINT",FACE,{"disambiguationData":[TD([[makeQuery(id+"F8.imprint","IMPRINT",EDGE,{"derivedFrom":sQuery(id+"F8.wireOp",EDGE,"E91.5.1")}),1.0]])]});
            var Q56;
            Q56=makeQuery(id+"F8.imprint","IMPRINT",FACE,{"disambiguationData":[TD([[makeQuery(id+"F8.imprint","IMPRINT",EDGE,{"derivedFrom":sQuery(id+"F8.wireOp",EDGE,"E91.5.29")}),1.0]])]});
            var Q57;
            Q57=makeQuery(id+"F8.imprint","IMPRINT",FACE,{"disambiguationData":[TD([[makeQuery(id+"F8.imprint","IMPRINT",EDGE,{"derivedFrom":sQuery(id+"F8.wireOp",EDGE,"E91.4.19")}),-1.0]])]});
            var Q58;
            Q58=makeQuery(id+"F8.imprint","IMPRINT",FACE,{"disambiguationData":[TD([[makeQuery(id+"F8.imprint","IMPRINT",EDGE,{"derivedFrom":sQuery(id+"F8.wireOp",EDGE,"E91.4.6")}),1.0]])]});
            var Q59;
            Q59=makeQuery(id+"F8.imprint","IMPRINT",FACE,{"disambiguationData":[TD([[makeQuery(id+"F8.imprint","IMPRINT",EDGE,{"derivedFrom":sQuery(id+"F8.wireOp",EDGE,"E91.4.4")}),-1.0]])]});
            var Q60;
            Q60=makeQuery(id+"F8.imprint","IMPRINT",FACE,{"disambiguationData":[TD([[makeQuery(id+"F8.imprint","IMPRINT",EDGE,{"derivedFrom":sQuery(id+"F8.wireOp",EDGE,"E91.4.12")}),-1.0]])]});
            var Q61;
            Q61=makeQuery(id+"F8.imprint","IMPRINT",FACE,{"disambiguationData":[TD([[makeQuery(id+"F8.imprint","IMPRINT",EDGE,{"derivedFrom":sQuery(id+"F8.wireOp",EDGE,"E91.4.21")}),1.0]])]});
            var Q62;
            Q62=makeQuery(id+"F8.imprint","IMPRINT",FACE,{"disambiguationData":[TD([[makeQuery(id+"F8.imprint","IMPRINT",EDGE,{"derivedFrom":sQuery(id+"F8.wireOp",EDGE,"E91.4.1")}),1.0]])]});
            var Q63;
            Q63=makeQuery(id+"F8.imprint","IMPRINT",FACE,{"disambiguationData":[TD([[makeQuery(id+"F8.imprint","IMPRINT",EDGE,{"derivedFrom":sQuery(id+"F8.wireOp",EDGE,"E91.4.29")}),1.0]])]});
            var Q64;
            Q64=makeQuery(id+"F8.imprint","IMPRINT",FACE,{"disambiguationData":[TD([[makeQuery(id+"F8.imprint","IMPRINT",EDGE,{"derivedFrom":sQuery(id+"F8.wireOp",EDGE,"E91.3.19")}),-1.0]])]});
            var Q65;
            Q65=makeQuery(id+"F8.imprint","IMPRINT",FACE,{"disambiguationData":[TD([[makeQuery(id+"F8.imprint","IMPRINT",EDGE,{"derivedFrom":sQuery(id+"F8.wireOp",EDGE,"E91.3.6")}),1.0]])]});
            var Q66;
            Q66=makeQuery(id+"F8.imprint","IMPRINT",FACE,{"disambiguationData":[TD([[makeQuery(id+"F8.imprint","IMPRINT",EDGE,{"derivedFrom":sQuery(id+"F8.wireOp",EDGE,"E91.3.4")}),-1.0]])]});
            var Q67;
            Q67=makeQuery(id+"F8.imprint","IMPRINT",FACE,{"disambiguationData":[TD([[makeQuery(id+"F8.imprint","IMPRINT",EDGE,{"derivedFrom":sQuery(id+"F8.wireOp",EDGE,"E91.3.12")}),-1.0]])]});
            var Q68;
            Q68=makeQuery(id+"F8.imprint","IMPRINT",FACE,{"disambiguationData":[TD([[makeQuery(id+"F8.imprint","IMPRINT",EDGE,{"derivedFrom":sQuery(id+"F8.wireOp",EDGE,"E91.3.21")}),1.0]])]});
            var Q69;
            Q69=makeQuery(id+"F8.imprint","IMPRINT",FACE,{"disambiguationData":[TD([[makeQuery(id+"F8.imprint","IMPRINT",EDGE,{"derivedFrom":sQuery(id+"F8.wireOp",EDGE,"E91.3.1")}),1.0]])]});
            var Q70;
            Q70=makeQuery(id+"F8.imprint","IMPRINT",FACE,{"disambiguationData":[TD([[makeQuery(id+"F8.imprint","IMPRINT",EDGE,{"derivedFrom":sQuery(id+"F8.wireOp",EDGE,"E91.3.29")}),1.0]])]});
            var Q71;
            Q71=makeQuery(id+"F8.imprint","IMPRINT",FACE,{"disambiguationData":[TD([[makeQuery(id+"F8.imprint","IMPRINT",EDGE,{"derivedFrom":sQuery(id+"F8.wireOp",EDGE,"E91.2.19")}),-1.0]])]});
            var Q72;
            Q72=makeQuery(id+"F8.imprint","IMPRINT",FACE,{"disambiguationData":[TD([[makeQuery(id+"F8.imprint","IMPRINT",EDGE,{"derivedFrom":sQuery(id+"F8.wireOp",EDGE,"E91.2.6")}),1.0]])]});
            var Q73;
            Q73=makeQuery(id+"F8.imprint","IMPRINT",FACE,{"disambiguationData":[TD([[makeQuery(id+"F8.imprint","IMPRINT",EDGE,{"derivedFrom":sQuery(id+"F8.wireOp",EDGE,"E91.2.4")}),-1.0]])]});
            var Q74;
            Q74=makeQuery(id+"F8.imprint","IMPRINT",FACE,{"disambiguationData":[TD([[makeQuery(id+"F8.imprint","IMPRINT",EDGE,{"derivedFrom":sQuery(id+"F8.wireOp",EDGE,"E91.2.12")}),-1.0]])]});
            var Q75;
            Q75=makeQuery(id+"F8.imprint","IMPRINT",FACE,{"disambiguationData":[TD([[makeQuery(id+"F8.imprint","IMPRINT",EDGE,{"derivedFrom":sQuery(id+"F8.wireOp",EDGE,"E91.2.21")}),1.0]])]});
            var Q76;
            Q76=makeQuery(id+"F8.imprint","IMPRINT",FACE,{"disambiguationData":[TD([[makeQuery(id+"F8.imprint","IMPRINT",EDGE,{"derivedFrom":sQuery(id+"F8.wireOp",EDGE,"E91.2.1")}),1.0]])]});
            var Q77;
            Q77=makeQuery(id+"F8.imprint","IMPRINT",FACE,{"disambiguationData":[TD([[makeQuery(id+"F8.imprint","IMPRINT",EDGE,{"derivedFrom":sQuery(id+"F8.wireOp",EDGE,"E91.2.29")}),1.0]])]});
            var Q78;
            Q78=makeQuery(id+"F8.imprint","IMPRINT",FACE,{"disambiguationData":[TD([[makeQuery(id+"F8.imprint","IMPRINT",EDGE,{"derivedFrom":sQuery(id+"F8.wireOp",EDGE,"E91.1.19")}),-1.0]])]});
            var Q79;
            Q79=makeQuery(id+"F8.imprint","IMPRINT",FACE,{"disambiguationData":[TD([[makeQuery(id+"F8.imprint","IMPRINT",EDGE,{"derivedFrom":sQuery(id+"F8.wireOp",EDGE,"E91.1.6")}),1.0]])]});
            var Q80;
            Q80=makeQuery(id+"F8.imprint","IMPRINT",FACE,{"disambiguationData":[TD([[makeQuery(id+"F8.imprint","IMPRINT",EDGE,{"derivedFrom":sQuery(id+"F8.wireOp",EDGE,"E91.1.4")}),-1.0]])]});
            var Q81;
            Q81=makeQuery(id+"F8.imprint","IMPRINT",FACE,{"disambiguationData":[TD([[makeQuery(id+"F8.imprint","IMPRINT",EDGE,{"derivedFrom":sQuery(id+"F8.wireOp",EDGE,"E91.1.12")}),-1.0]])]});
            var Q82;
            Q82=makeQuery(id+"F8.imprint","IMPRINT",FACE,{"disambiguationData":[TD([[makeQuery(id+"F8.imprint","IMPRINT",EDGE,{"derivedFrom":sQuery(id+"F8.wireOp",EDGE,"E91.1.21")}),1.0]])]});
            var Q83;
            Q83=makeQuery(id+"F8.imprint","IMPRINT",FACE,{"disambiguationData":[TD([[makeQuery(id+"F8.imprint","IMPRINT",EDGE,{"derivedFrom":sQuery(id+"F8.wireOp",EDGE,"E91.1.1")}),1.0]])]});
            var Q84;
            Q84=makeQuery(id+"F8.imprint","IMPRINT",FACE,{"disambiguationData":[TD([[makeQuery(id+"F8.imprint","IMPRINT",EDGE,{"derivedFrom":sQuery(id+"F8.wireOp",EDGE,"E91.1.29")}),1.0]])]});
            extrude(context, id + "F9", {"entities" : qUnion([Q0, Q1, Q2, Q3, Q4, Q5, Q6, Q7, Q8, Q9, Q10, Q11, Q12, Q13, Q14, Q15, Q16, Q17, Q18, Q19, Q20, Q21, Q22, Q23, Q24, Q25, Q26, Q27, Q28, Q29, Q30, Q31, Q32, Q33, Q34, Q35, Q36, Q37, Q38, Q39, Q40, Q41, Q42, Q43, Q44, Q45, Q46, Q47, Q48, Q49, Q50, Q51, Q52, Q53, Q54, Q55, Q56, Q57, Q58, Q59, Q60, Q61, Q62, Q63, Q64, Q65, Q66, Q67, Q68, Q69, Q70, Q71, Q72, Q73, Q74, Q75, Q76, Q77, Q78, Q79, Q80, Q81, Q82, Q83, Q84]), "operationType" : NewBodyOperationType.ADD, "depth" : 2 * mm, "offsetDistance" : 25 * mm});
        }
    });
